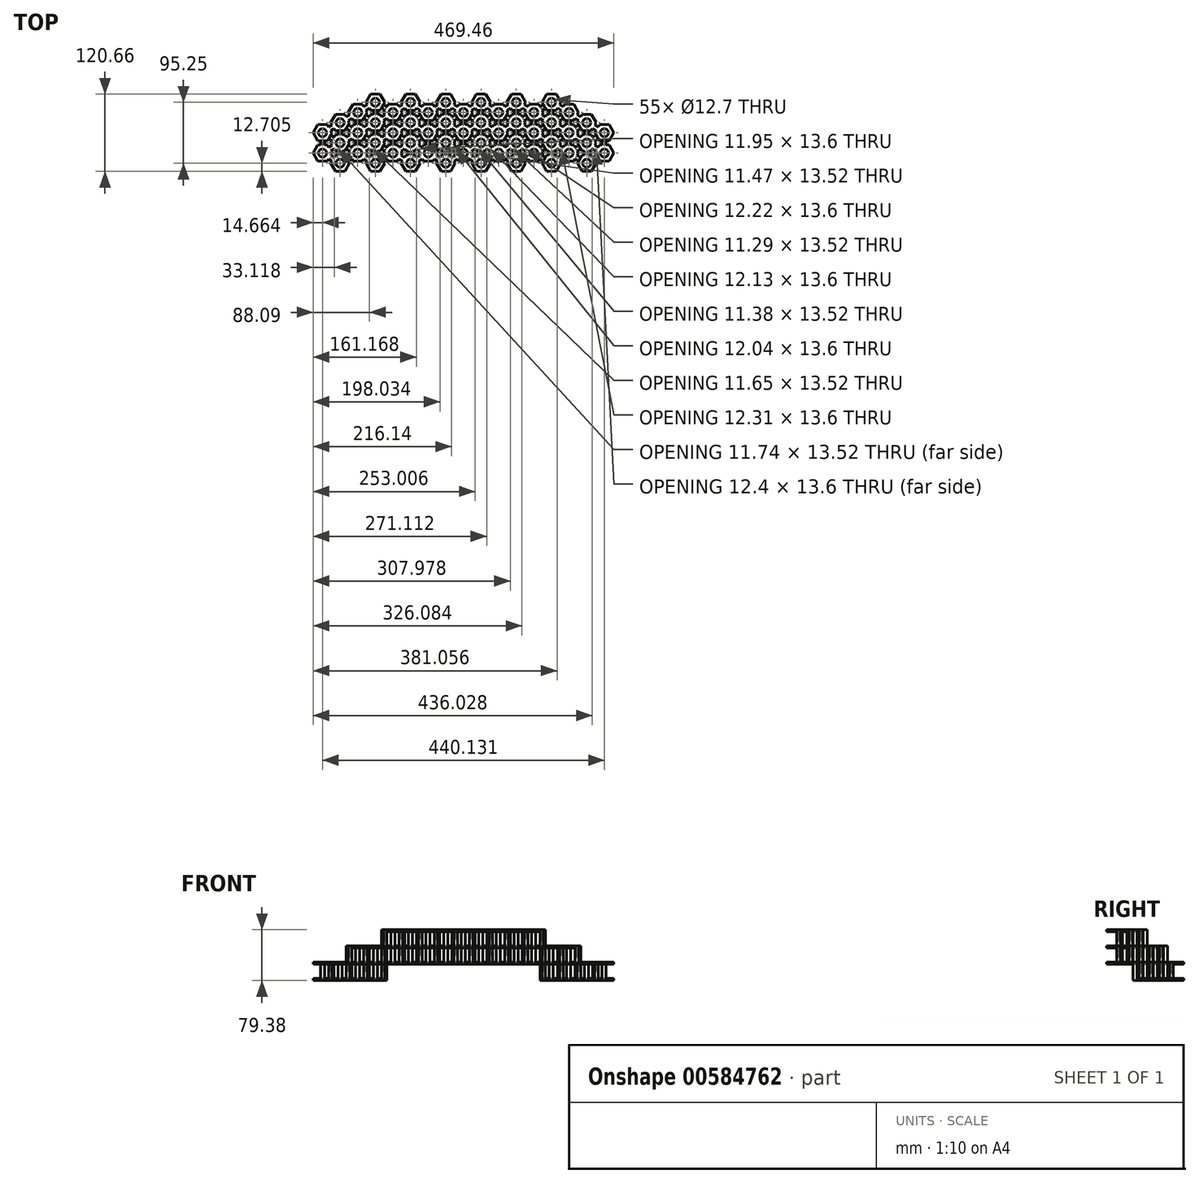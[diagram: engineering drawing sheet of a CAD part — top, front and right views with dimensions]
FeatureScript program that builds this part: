
annotation { "Feature Type Name" : "Feature", "Feature Type Description" : "" }
export const myFeature = defineFeature(function(context is Context, id is Id, definition is map)
    precondition{}
    {
        {
            var Q0;
            Q0=qCreatedBy(makeId("Top.planeOp"),FACE);
            var sketch = newSketch(context, id + "F0", { "sketchPlane" : qUnion([Q0])});
            skLineSegment(sketch, "E0", {"start": v(-220.07, 0) * mm, "end": v(-220.07, -12.7) * mm, "construction": true});
            skLineSegment(sketch, "E1", {"start": v(-234.73, 0) * mm, "end": v(-220.07, 0) * mm, "construction": true});
            skCircle(sketch, "E2.cCircle", {"center": v(-220.07, 0) * mm, "radius": 12.7 * mm, "construction": true});
            skLineSegment(sketch, "E2.0", {"start": v(-212.73, -12.7) * mm, "end": v(-227.4, -12.7) * mm});
            skLineSegment(sketch, "E2.1", {"start": v(-227.4, -12.7) * mm, "end": v(-234.73, 0) * mm});
            skLineSegment(sketch, "E2.2", {"start": v(-234.73, 0) * mm, "end": v(-227.4, 12.7) * mm});
            skLineSegment(sketch, "E2.3", {"start": v(-227.4, 12.7) * mm, "end": v(-212.73, 12.7) * mm});
            skLineSegment(sketch, "E2.4", {"start": v(-212.73, 12.7) * mm, "end": v(-205.4, 0) * mm});
            skLineSegment(sketch, "E2.5", {"start": v(-205.4, 0) * mm, "end": v(-212.73, -12.7) * mm});
            skPoint(sketch, "E2.0.midPoint", {"position": v(-220.07, -12.7) * mm});
            skCircle(sketch, "E3", {"center": v(-220.07, 0) * mm, "radius": 6.35 * mm});
            skLineSegment(sketch, "E4", {"start": v(-220.07, 0) * mm, "end": v(-192.57, -15.88) * mm, "construction": true});
            skCircle(sketch, "E5", {"center": v(-192.57, -15.88) * mm, "radius": 6.35 * mm});
            skCircle(sketch, "E6.cCircle", {"center": v(-192.57, -15.88) * mm, "radius": 12.7 * mm, "construction": true});
            skLineSegment(sketch, "E6.0", {"start": v(-199.9, -3.18) * mm, "end": v(-185.24, -3.18) * mm});
            skLineSegment(sketch, "E6.1", {"start": v(-185.24, -3.18) * mm, "end": v(-177.9, -15.88) * mm});
            skLineSegment(sketch, "E6.2", {"start": v(-177.9, -15.87) * mm, "end": v(-185.24, -28.57) * mm});
            skLineSegment(sketch, "E6.3", {"start": v(-185.24, -28.58) * mm, "end": v(-199.9, -28.58) * mm});
            skLineSegment(sketch, "E6.4", {"start": v(-199.9, -28.58) * mm, "end": v(-207.23, -15.88) * mm});
            skLineSegment(sketch, "E6.5", {"start": v(-207.23, -15.88) * mm, "end": v(-199.9, -3.18) * mm});
            skPoint(sketch, "E6.0.midPoint", {"position": v(-192.57, -3.18) * mm});
            skLineSegment(sketch, "E7", {"start": v(-192.57, -15.88) * mm, "end": v(-207.23, -15.88) * mm, "construction": true});
            skLineSegment(sketch, "E8", {"start": v(-192.57, -15.88) * mm, "end": v(-192.57, -28.58) * mm, "construction": true});
            skCircle(sketch, "E9.1.0.0", {"center": v(-137.55, -15.88) * mm, "radius": 6.35 * mm});
            skLineSegment(sketch, "E9.1.0.1", {"start": v(-172.38, 12.7) * mm, "end": v(-157.72, 12.7) * mm});
            skLineSegment(sketch, "E9.1.0.2", {"start": v(-144.89, -3.18) * mm, "end": v(-130.22, -3.18) * mm});
            skLineSegment(sketch, "E9.1.0.3", {"start": v(-152.22, -15.88) * mm, "end": v(-144.89, -3.18) * mm});
            skLineSegment(sketch, "E9.1.0.4", {"start": v(-179.71, 0) * mm, "end": v(-172.38, 12.7) * mm});
            skLineSegment(sketch, "E9.1.0.5", {"start": v(-144.89, -28.58) * mm, "end": v(-152.22, -15.88) * mm});
            skCircle(sketch, "E9.1.0.6", {"center": v(-165.05, 0) * mm, "radius": 6.35 * mm});
            skLineSegment(sketch, "E9.1.0.7", {"start": v(-172.38, -12.7) * mm, "end": v(-179.71, 0) * mm});
            skLineSegment(sketch, "E9.1.0.8", {"start": v(-130.22, -28.58) * mm, "end": v(-144.89, -28.58) * mm});
            skLineSegment(sketch, "E9.1.0.9", {"start": v(-157.72, -12.7) * mm, "end": v(-172.38, -12.7) * mm});
            skLineSegment(sketch, "E9.1.0.10", {"start": v(-150.38, 0) * mm, "end": v(-157.72, -12.7) * mm});
            skLineSegment(sketch, "E9.1.0.11", {"start": v(-122.89, -15.88) * mm, "end": v(-130.22, -28.58) * mm});
            skLineSegment(sketch, "E9.1.0.12", {"start": v(-157.72, 12.7) * mm, "end": v(-150.38, 0) * mm});
            skLineSegment(sketch, "E9.1.0.13", {"start": v(-130.22, -3.18) * mm, "end": v(-122.89, -15.88) * mm});
            skCircle(sketch, "E9.2.0.0", {"center": v(-82.54, -15.88) * mm, "radius": 6.35 * mm});
            skLineSegment(sketch, "E9.2.0.1", {"start": v(-117.37, 12.7) * mm, "end": v(-102.7, 12.7) * mm});
            skLineSegment(sketch, "E9.2.0.2", {"start": v(-89.87, -3.18) * mm, "end": v(-75.2, -3.18) * mm});
            skLineSegment(sketch, "E9.2.0.3", {"start": v(-97.2, -15.88) * mm, "end": v(-89.87, -3.18) * mm});
            skLineSegment(sketch, "E9.2.0.4", {"start": v(-124.7, 0) * mm, "end": v(-117.37, 12.7) * mm});
            skLineSegment(sketch, "E9.2.0.5", {"start": v(-89.87, -28.58) * mm, "end": v(-97.2, -15.88) * mm});
            skCircle(sketch, "E9.2.0.6", {"center": v(-110.03, 0) * mm, "radius": 6.35 * mm});
            skLineSegment(sketch, "E9.2.0.7", {"start": v(-117.37, -12.7) * mm, "end": v(-124.7, 0) * mm});
            skLineSegment(sketch, "E9.2.0.8", {"start": v(-75.2, -28.58) * mm, "end": v(-89.87, -28.58) * mm});
            skLineSegment(sketch, "E9.2.0.9", {"start": v(-102.7, -12.7) * mm, "end": v(-117.37, -12.7) * mm});
            skLineSegment(sketch, "E9.2.0.10", {"start": v(-95.37, 0) * mm, "end": v(-102.7, -12.7) * mm});
            skLineSegment(sketch, "E9.2.0.11", {"start": v(-67.87, -15.88) * mm, "end": v(-75.2, -28.58) * mm});
            skLineSegment(sketch, "E9.2.0.12", {"start": v(-102.7, 12.7) * mm, "end": v(-95.37, 0) * mm});
            skLineSegment(sketch, "E9.2.0.13", {"start": v(-75.2, -3.18) * mm, "end": v(-67.87, -15.88) * mm});
            skCircle(sketch, "E9.3.0.0", {"center": v(-27.52, -15.88) * mm, "radius": 6.35 * mm});
            skLineSegment(sketch, "E9.3.0.1", {"start": v(-62.35, 12.7) * mm, "end": v(-47.68, 12.7) * mm});
            skLineSegment(sketch, "E9.3.0.2", {"start": v(-34.85, -3.18) * mm, "end": v(-20.19, -3.18) * mm});
            skLineSegment(sketch, "E9.3.0.3", {"start": v(-42.18, -15.88) * mm, "end": v(-34.85, -3.18) * mm});
            skLineSegment(sketch, "E9.3.0.4", {"start": v(-69.68, 0) * mm, "end": v(-62.35, 12.7) * mm});
            skLineSegment(sketch, "E9.3.0.5", {"start": v(-34.85, -28.58) * mm, "end": v(-42.18, -15.88) * mm});
            skCircle(sketch, "E9.3.0.6", {"center": v(-55.02, 0) * mm, "radius": 6.35 * mm});
            skLineSegment(sketch, "E9.3.0.7", {"start": v(-62.35, -12.7) * mm, "end": v(-69.68, 0) * mm});
            skLineSegment(sketch, "E9.3.0.8", {"start": v(-20.19, -28.58) * mm, "end": v(-34.85, -28.58) * mm});
            skLineSegment(sketch, "E9.3.0.9", {"start": v(-47.68, -12.7) * mm, "end": v(-62.35, -12.7) * mm});
            skLineSegment(sketch, "E9.3.0.10", {"start": v(-40.35, 0) * mm, "end": v(-47.68, -12.7) * mm});
            skLineSegment(sketch, "E9.3.0.11", {"start": v(-12.86, -15.88) * mm, "end": v(-20.19, -28.58) * mm});
            skLineSegment(sketch, "E9.3.0.12", {"start": v(-47.68, 12.7) * mm, "end": v(-40.35, 0) * mm});
            skLineSegment(sketch, "E9.3.0.13", {"start": v(-20.19, -3.18) * mm, "end": v(-12.86, -15.88) * mm});
            skCircle(sketch, "E9.4.0.0", {"center": v(27.5, -15.88) * mm, "radius": 6.35 * mm});
            skLineSegment(sketch, "E9.4.0.1", {"start": v(-7.33, 12.7) * mm, "end": v(7.33, 12.7) * mm});
            skLineSegment(sketch, "E9.4.0.2", {"start": v(20.16, -3.18) * mm, "end": v(34.83, -3.18) * mm});
            skLineSegment(sketch, "E9.4.0.3", {"start": v(12.83, -15.88) * mm, "end": v(20.16, -3.18) * mm});
            skLineSegment(sketch, "E9.4.0.4", {"start": v(-14.66, 0) * mm, "end": v(-7.33, 12.7) * mm});
            skLineSegment(sketch, "E9.4.0.5", {"start": v(20.16, -28.58) * mm, "end": v(12.83, -15.88) * mm});
            skCircle(sketch, "E9.4.0.6", {"center": v(0, 0) * mm, "radius": 6.35 * mm});
            skLineSegment(sketch, "E9.4.0.7", {"start": v(-7.33, -12.7) * mm, "end": v(-14.66, 0) * mm});
            skLineSegment(sketch, "E9.4.0.8", {"start": v(34.83, -28.57) * mm, "end": v(20.16, -28.57) * mm});
            skLineSegment(sketch, "E9.4.0.9", {"start": v(7.33, -12.7) * mm, "end": v(-7.33, -12.7) * mm});
            skLineSegment(sketch, "E9.4.0.10", {"start": v(14.66, 0) * mm, "end": v(7.33, -12.7) * mm});
            skLineSegment(sketch, "E9.4.0.11", {"start": v(42.16, -15.87) * mm, "end": v(34.83, -28.57) * mm});
            skLineSegment(sketch, "E9.4.0.12", {"start": v(7.33, 12.7) * mm, "end": v(14.66, 0) * mm});
            skLineSegment(sketch, "E9.4.0.13", {"start": v(34.83, -3.18) * mm, "end": v(42.16, -15.88) * mm});
            skCircle(sketch, "E9.5.0.0", {"center": v(82.51, -15.87) * mm, "radius": 6.35 * mm});
            skLineSegment(sketch, "E9.5.0.1", {"start": v(47.68, 12.7) * mm, "end": v(62.35, 12.7) * mm});
            skLineSegment(sketch, "E9.5.0.2", {"start": v(75.18, -3.18) * mm, "end": v(89.85, -3.17) * mm});
            skLineSegment(sketch, "E9.5.0.3", {"start": v(67.85, -15.88) * mm, "end": v(75.18, -3.18) * mm});
            skLineSegment(sketch, "E9.5.0.4", {"start": v(40.35, 0) * mm, "end": v(47.68, 12.7) * mm});
            skLineSegment(sketch, "E9.5.0.5", {"start": v(75.18, -28.57) * mm, "end": v(67.85, -15.87) * mm});
            skCircle(sketch, "E9.5.0.6", {"center": v(55.02, 0) * mm, "radius": 6.35 * mm});
            skLineSegment(sketch, "E9.5.0.7", {"start": v(47.68, -12.7) * mm, "end": v(40.35, 0) * mm});
            skLineSegment(sketch, "E9.5.0.8", {"start": v(89.85, -28.57) * mm, "end": v(75.18, -28.57) * mm});
            skLineSegment(sketch, "E9.5.0.9", {"start": v(62.35, -12.7) * mm, "end": v(47.68, -12.7) * mm});
            skLineSegment(sketch, "E9.5.0.10", {"start": v(69.68, 0) * mm, "end": v(62.35, -12.7) * mm});
            skLineSegment(sketch, "E9.5.0.11", {"start": v(97.18, -15.87) * mm, "end": v(89.85, -28.57) * mm});
            skLineSegment(sketch, "E9.5.0.12", {"start": v(62.35, 12.7) * mm, "end": v(69.68, 0) * mm});
            skLineSegment(sketch, "E9.5.0.13", {"start": v(89.85, -3.17) * mm, "end": v(97.18, -15.87) * mm});
            skCircle(sketch, "E9.6.0.0", {"center": v(137.53, -15.87) * mm, "radius": 6.35 * mm});
            skLineSegment(sketch, "E9.6.0.1", {"start": v(102.7, 12.7) * mm, "end": v(117.37, 12.7) * mm});
            skLineSegment(sketch, "E9.6.0.2", {"start": v(130.2, -3.17) * mm, "end": v(144.86, -3.17) * mm});
            skLineSegment(sketch, "E9.6.0.3", {"start": v(122.86, -15.87) * mm, "end": v(130.2, -3.17) * mm});
            skLineSegment(sketch, "E9.6.0.4", {"start": v(95.37, 0) * mm, "end": v(102.7, 12.7) * mm});
            skLineSegment(sketch, "E9.6.0.5", {"start": v(130.2, -28.57) * mm, "end": v(122.86, -15.87) * mm});
            skCircle(sketch, "E9.6.0.6", {"center": v(110.03, 0) * mm, "radius": 6.35 * mm});
            skLineSegment(sketch, "E9.6.0.7", {"start": v(102.7, -12.7) * mm, "end": v(95.37, 0) * mm});
            skLineSegment(sketch, "E9.6.0.8", {"start": v(144.86, -28.57) * mm, "end": v(130.2, -28.57) * mm});
            skLineSegment(sketch, "E9.6.0.9", {"start": v(117.37, -12.7) * mm, "end": v(102.7, -12.7) * mm});
            skLineSegment(sketch, "E9.6.0.10", {"start": v(124.7, 0) * mm, "end": v(117.37, -12.7) * mm});
            skLineSegment(sketch, "E9.6.0.11", {"start": v(152.2, -15.87) * mm, "end": v(144.86, -28.57) * mm});
            skLineSegment(sketch, "E9.6.0.12", {"start": v(117.37, 12.7) * mm, "end": v(124.7, 0) * mm});
            skLineSegment(sketch, "E9.6.0.13", {"start": v(144.86, -3.17) * mm, "end": v(152.2, -15.87) * mm});
            skCircle(sketch, "E9.7.0.0", {"center": v(192.55, -15.87) * mm, "radius": 6.35 * mm});
            skLineSegment(sketch, "E9.7.0.1", {"start": v(157.72, 12.7) * mm, "end": v(172.38, 12.7) * mm});
            skLineSegment(sketch, "E9.7.0.2", {"start": v(185.21, -3.17) * mm, "end": v(199.88, -3.17) * mm});
            skLineSegment(sketch, "E9.7.0.3", {"start": v(177.88, -15.87) * mm, "end": v(185.21, -3.17) * mm});
            skLineSegment(sketch, "E9.7.0.4", {"start": v(150.38, 0) * mm, "end": v(157.72, 12.7) * mm});
            skLineSegment(sketch, "E9.7.0.5", {"start": v(185.21, -28.57) * mm, "end": v(177.88, -15.87) * mm});
            skCircle(sketch, "E9.7.0.6", {"center": v(165.05, 0) * mm, "radius": 6.35 * mm});
            skLineSegment(sketch, "E9.7.0.7", {"start": v(157.72, -12.7) * mm, "end": v(150.38, 0) * mm});
            skLineSegment(sketch, "E9.7.0.8", {"start": v(199.88, -28.57) * mm, "end": v(185.21, -28.57) * mm});
            skLineSegment(sketch, "E9.7.0.9", {"start": v(172.38, -12.7) * mm, "end": v(157.72, -12.7) * mm});
            skLineSegment(sketch, "E9.7.0.10", {"start": v(179.71, 0) * mm, "end": v(172.38, -12.7) * mm});
            skLineSegment(sketch, "E9.7.0.11", {"start": v(207.21, -15.87) * mm, "end": v(199.88, -28.57) * mm});
            skLineSegment(sketch, "E9.7.0.12", {"start": v(172.38, 12.7) * mm, "end": v(179.71, 0) * mm});
            skLineSegment(sketch, "E9.7.0.13", {"start": v(199.88, -3.17) * mm, "end": v(207.21, -15.87) * mm});
            skLineSegment(sketch, "E9.8.0.1", {"start": v(212.73, 12.7) * mm, "end": v(227.4, 12.7) * mm});
            skLineSegment(sketch, "E9.8.0.4", {"start": v(205.4, 0) * mm, "end": v(212.73, 12.7) * mm});
            skCircle(sketch, "E9.8.0.6", {"center": v(220.07, 0) * mm, "radius": 6.35 * mm});
            skLineSegment(sketch, "E9.8.0.7", {"start": v(212.73, -12.7) * mm, "end": v(205.4, 0) * mm});
            skLineSegment(sketch, "E9.8.0.9", {"start": v(227.4, -12.7) * mm, "end": v(212.73, -12.7) * mm});
            skLineSegment(sketch, "E9.8.0.10", {"start": v(234.73, 0) * mm, "end": v(227.4, -12.7) * mm});
            skLineSegment(sketch, "E9.8.0.12", {"start": v(227.4, 12.7) * mm, "end": v(234.73, 0) * mm});
            skLineSegment(sketch, "E9.direction1", {"start": v(-192.57, -15.88) * mm, "end": v(-137.55, -15.88) * mm, "construction": true});
            skLineSegment(sketch, "E10.0.1.0", {"start": v(14.66, 31.75) * mm, "end": v(7.33, 19.05) * mm});
            skLineSegment(sketch, "E10.0.1.1", {"start": v(40.35, 31.75) * mm, "end": v(47.68, 44.45) * mm});
            skCircle(sketch, "E10.0.1.2", {"center": v(165.05, 31.75) * mm, "radius": 6.35 * mm});
            skLineSegment(sketch, "E10.0.1.3", {"start": v(-172.38, 44.45) * mm, "end": v(-157.72, 44.45) * mm});
            skLineSegment(sketch, "E10.0.1.4", {"start": v(212.73, 44.45) * mm, "end": v(227.4, 44.45) * mm});
            skLineSegment(sketch, "E10.0.1.5", {"start": v(-75.2, 3.18) * mm, "end": v(-89.87, 3.18) * mm});
            skLineSegment(sketch, "E10.0.1.6", {"start": v(199.88, 28.57) * mm, "end": v(207.21, 15.88) * mm});
            skLineSegment(sketch, "E10.0.1.7", {"start": v(-42.18, 15.88) * mm, "end": v(-34.85, 28.57) * mm});
            skLineSegment(sketch, "E10.0.1.8", {"start": v(227.4, 44.45) * mm, "end": v(234.73, 31.75) * mm});
            skLineSegment(sketch, "E10.0.1.9", {"start": v(75.18, 3.18) * mm, "end": v(67.85, 15.88) * mm});
            skCircle(sketch, "E10.0.1.10", {"center": v(137.53, 15.88) * mm, "radius": 6.35 * mm});
            skLineSegment(sketch, "E10.0.1.11", {"start": v(157.72, 19.05) * mm, "end": v(150.38, 31.75) * mm});
            skLineSegment(sketch, "E10.0.1.12", {"start": v(-144.89, 28.57) * mm, "end": v(-130.22, 28.57) * mm});
            skLineSegment(sketch, "E10.0.1.13", {"start": v(-75.2, 28.57) * mm, "end": v(-67.87, 15.88) * mm});
            skLineSegment(sketch, "E10.0.1.14", {"start": v(-102.7, 19.05) * mm, "end": v(-117.37, 19.05) * mm});
            skCircle(sketch, "E10.0.1.15", {"center": v(-192.57, 15.88) * mm, "radius": 6.35 * mm});
            skLineSegment(sketch, "E10.0.1.16", {"start": v(-69.68, 31.75) * mm, "end": v(-62.35, 44.45) * mm});
            skLineSegment(sketch, "E10.0.1.17", {"start": v(-47.68, 44.45) * mm, "end": v(-40.35, 31.75) * mm});
            skLineSegment(sketch, "E10.0.1.18", {"start": v(42.16, 15.88) * mm, "end": v(34.83, 3.18) * mm});
            skCircle(sketch, "E10.0.1.19", {"center": v(55.02, 31.75) * mm, "radius": 6.35 * mm});
            skLineSegment(sketch, "E10.0.1.20", {"start": v(102.7, 44.45) * mm, "end": v(117.37, 44.45) * mm});
            skLineSegment(sketch, "E10.0.1.21", {"start": v(69.68, 31.75) * mm, "end": v(62.35, 19.05) * mm});
            skLineSegment(sketch, "E10.0.1.22", {"start": v(-152.22, 15.88) * mm, "end": v(-144.89, 28.57) * mm});
            skLineSegment(sketch, "E10.0.1.23", {"start": v(-234.73, 31.75) * mm, "end": v(-227.4, 44.45) * mm});
            skLineSegment(sketch, "E10.0.1.24", {"start": v(199.88, 3.18) * mm, "end": v(185.21, 3.18) * mm});
            skLineSegment(sketch, "E10.0.1.25", {"start": v(-199.9, 28.57) * mm, "end": v(-185.24, 28.57) * mm});
            skLineSegment(sketch, "E10.0.1.26", {"start": v(-34.85, 3.18) * mm, "end": v(-42.18, 15.88) * mm});
            skCircle(sketch, "E10.0.1.27", {"center": v(27.5, 15.88) * mm, "radius": 6.35 * mm});
            skLineSegment(sketch, "E10.0.1.28", {"start": v(-199.9, 3.18) * mm, "end": v(-207.23, 15.88) * mm});
            skLineSegment(sketch, "E10.0.1.29", {"start": v(47.68, 19.05) * mm, "end": v(40.35, 31.75) * mm});
            skLineSegment(sketch, "E10.0.1.30", {"start": v(130.2, 28.57) * mm, "end": v(144.86, 28.57) * mm});
            skLineSegment(sketch, "E10.0.1.31", {"start": v(172.38, 19.05) * mm, "end": v(157.72, 19.05) * mm});
            skLineSegment(sketch, "E10.0.1.32", {"start": v(-179.71, 31.75) * mm, "end": v(-172.38, 44.45) * mm});
            skLineSegment(sketch, "E10.0.1.33", {"start": v(205.4, 31.75) * mm, "end": v(212.73, 44.45) * mm});
            skLineSegment(sketch, "E10.0.1.34", {"start": v(-20.19, 28.57) * mm, "end": v(-12.86, 15.88) * mm});
            skCircle(sketch, "E10.0.1.35", {"center": v(-55.02, 31.75) * mm, "radius": 6.35 * mm});
            skLineSegment(sketch, "E10.0.1.36", {"start": v(-7.33, 44.45) * mm, "end": v(7.33, 44.45) * mm});
            skLineSegment(sketch, "E10.0.1.37", {"start": v(7.33, 44.45) * mm, "end": v(14.66, 31.75) * mm});
            skLineSegment(sketch, "E10.0.1.38", {"start": v(89.85, 3.18) * mm, "end": v(75.18, 3.18) * mm});
            skLineSegment(sketch, "E10.0.1.39", {"start": v(97.18, 15.88) * mm, "end": v(89.85, 3.18) * mm});
            skLineSegment(sketch, "E10.0.1.40", {"start": v(122.86, 15.88) * mm, "end": v(130.2, 28.57) * mm});
            skLineSegment(sketch, "E10.0.1.41", {"start": v(-144.89, 3.18) * mm, "end": v(-152.22, 15.88) * mm});
            skCircle(sketch, "E10.0.1.42", {"center": v(-220.07, 31.75) * mm, "radius": 6.35 * mm});
            skLineSegment(sketch, "E10.0.1.43", {"start": v(124.7, 31.75) * mm, "end": v(117.37, 19.05) * mm});
            skCircle(sketch, "E10.0.1.44", {"center": v(-82.54, 15.88) * mm, "radius": 6.35 * mm});
            skLineSegment(sketch, "E10.0.1.45", {"start": v(-62.35, 19.05) * mm, "end": v(-69.68, 31.75) * mm});
            skLineSegment(sketch, "E10.0.1.46", {"start": v(20.16, 28.57) * mm, "end": v(34.83, 28.57) * mm});
            skLineSegment(sketch, "E10.0.1.47", {"start": v(62.35, 19.05) * mm, "end": v(47.68, 19.05) * mm});
            skLineSegment(sketch, "E10.0.1.48", {"start": v(95.37, 31.75) * mm, "end": v(102.7, 44.45) * mm});
            skCircle(sketch, "E10.0.1.49", {"center": v(-165.05, 31.75) * mm, "radius": 6.35 * mm});
            skLineSegment(sketch, "E10.0.1.50", {"start": v(-150.38, 31.75) * mm, "end": v(-157.72, 19.05) * mm});
            skCircle(sketch, "E10.0.1.51", {"center": v(220.07, 31.75) * mm, "radius": 6.35 * mm});
            skLineSegment(sketch, "E10.0.1.52", {"start": v(-185.24, 28.57) * mm, "end": v(-177.9, 15.88) * mm});
            skLineSegment(sketch, "E10.0.1.53", {"start": v(-117.37, 44.45) * mm, "end": v(-102.7, 44.45) * mm});
            skLineSegment(sketch, "E10.0.1.54", {"start": v(-227.4, 44.45) * mm, "end": v(-212.73, 44.45) * mm});
            skLineSegment(sketch, "E10.0.1.55", {"start": v(-20.19, 3.18) * mm, "end": v(-34.85, 3.18) * mm});
            skLineSegment(sketch, "E10.0.1.56", {"start": v(12.83, 15.88) * mm, "end": v(20.16, 28.57) * mm});
            skLineSegment(sketch, "E10.0.1.57", {"start": v(34.83, 28.57) * mm, "end": v(42.16, 15.88) * mm});
            skLineSegment(sketch, "E10.0.1.58", {"start": v(-207.23, 15.88) * mm, "end": v(-199.9, 28.57) * mm});
            skLineSegment(sketch, "E10.0.1.59", {"start": v(62.35, 44.45) * mm, "end": v(69.68, 31.75) * mm});
            skLineSegment(sketch, "E10.0.1.60", {"start": v(130.2, 3.18) * mm, "end": v(122.86, 15.88) * mm});
            skCircle(sketch, "E10.0.1.61", {"center": v(192.55, 15.88) * mm, "radius": 6.35 * mm});
            skLineSegment(sketch, "E10.0.1.62", {"start": v(-172.38, 19.05) * mm, "end": v(-179.71, 31.75) * mm});
            skLineSegment(sketch, "E10.0.1.63", {"start": v(152.2, 15.88) * mm, "end": v(144.86, 3.18) * mm});
            skLineSegment(sketch, "E10.0.1.64", {"start": v(212.73, 19.05) * mm, "end": v(205.4, 31.75) * mm});
            skLineSegment(sketch, "E10.0.1.65", {"start": v(-89.87, 28.57) * mm, "end": v(-75.2, 28.57) * mm});
            skLineSegment(sketch, "E10.0.1.66", {"start": v(179.71, 31.75) * mm, "end": v(172.38, 19.05) * mm});
            skLineSegment(sketch, "E10.0.1.67", {"start": v(-47.68, 19.05) * mm, "end": v(-62.35, 19.05) * mm});
            skLineSegment(sketch, "E10.0.1.68", {"start": v(-14.66, 31.75) * mm, "end": v(-7.33, 44.45) * mm});
            skCircle(sketch, "E10.0.1.69", {"center": v(110.03, 31.75) * mm, "radius": 6.35 * mm});
            skLineSegment(sketch, "E10.0.1.70", {"start": v(157.72, 44.45) * mm, "end": v(172.38, 44.45) * mm});
            skLineSegment(sketch, "E10.0.1.71", {"start": v(-122.89, 15.88) * mm, "end": v(-130.22, 3.18) * mm});
            skLineSegment(sketch, "E10.0.1.72", {"start": v(-130.22, 3.18) * mm, "end": v(-144.89, 3.18) * mm});
            skLineSegment(sketch, "E10.0.1.73", {"start": v(-97.2, 15.88) * mm, "end": v(-89.87, 28.57) * mm});
            skLineSegment(sketch, "E10.0.1.74", {"start": v(-95.37, 31.75) * mm, "end": v(-102.7, 19.05) * mm});
            skLineSegment(sketch, "E10.0.1.75", {"start": v(20.16, 3.18) * mm, "end": v(12.83, 15.88) * mm});
            skCircle(sketch, "E10.0.1.76", {"center": v(82.51, 15.88) * mm, "radius": 6.35 * mm});
            skLineSegment(sketch, "E10.0.1.77", {"start": v(89.85, 28.57) * mm, "end": v(97.18, 15.88) * mm});
            skLineSegment(sketch, "E10.0.1.78", {"start": v(102.7, 19.05) * mm, "end": v(95.37, 31.75) * mm});
            skLineSegment(sketch, "E10.0.1.79", {"start": v(-212.73, 19.05) * mm, "end": v(-227.4, 19.05) * mm});
            skLineSegment(sketch, "E10.0.1.80", {"start": v(185.21, 28.57) * mm, "end": v(199.88, 28.57) * mm});
            skLineSegment(sketch, "E10.0.1.81", {"start": v(-157.72, 19.05) * mm, "end": v(-172.38, 19.05) * mm});
            skLineSegment(sketch, "E10.0.1.82", {"start": v(117.37, 44.45) * mm, "end": v(124.7, 31.75) * mm});
            skLineSegment(sketch, "E10.0.1.83", {"start": v(227.4, 19.05) * mm, "end": v(212.73, 19.05) * mm});
            skLineSegment(sketch, "E10.0.1.84", {"start": v(-124.7, 31.75) * mm, "end": v(-117.37, 44.45) * mm});
            skLineSegment(sketch, "E10.0.1.85", {"start": v(207.21, 15.88) * mm, "end": v(199.88, 3.18) * mm});
            skLineSegment(sketch, "E10.0.1.86", {"start": v(-177.9, 15.88) * mm, "end": v(-185.24, 3.18) * mm});
            skLineSegment(sketch, "E10.0.1.87", {"start": v(-212.73, 44.45) * mm, "end": v(-205.4, 31.75) * mm});
            skLineSegment(sketch, "E10.0.1.88", {"start": v(234.73, 31.75) * mm, "end": v(227.4, 19.05) * mm});
            skCircle(sketch, "E10.0.1.89", {"center": v(0, 31.75) * mm, "radius": 6.35 * mm});
            skLineSegment(sketch, "E10.0.1.90", {"start": v(47.68, 44.45) * mm, "end": v(62.35, 44.45) * mm});
            skLineSegment(sketch, "E10.0.1.91", {"start": v(144.86, 3.18) * mm, "end": v(130.2, 3.18) * mm});
            skLineSegment(sketch, "E10.0.1.92", {"start": v(177.88, 15.88) * mm, "end": v(185.21, 28.57) * mm});
            skLineSegment(sketch, "E10.0.1.93", {"start": v(-157.72, 44.45) * mm, "end": v(-150.38, 31.75) * mm});
            skLineSegment(sketch, "E10.0.1.94", {"start": v(-89.87, 3.18) * mm, "end": v(-97.2, 15.88) * mm});
            skLineSegment(sketch, "E10.0.1.95", {"start": v(-67.87, 15.88) * mm, "end": v(-75.2, 3.18) * mm});
            skCircle(sketch, "E10.0.1.96", {"center": v(-27.52, 15.88) * mm, "radius": 6.35 * mm});
            skLineSegment(sketch, "E10.0.1.97", {"start": v(-40.35, 31.75) * mm, "end": v(-47.68, 19.05) * mm});
            skLineSegment(sketch, "E10.0.1.98", {"start": v(-7.33, 19.05) * mm, "end": v(-14.66, 31.75) * mm});
            skLineSegment(sketch, "E10.0.1.99", {"start": v(75.18, 28.57) * mm, "end": v(89.85, 28.57) * mm});
            skLineSegment(sketch, "E10.0.1.100", {"start": v(117.37, 19.05) * mm, "end": v(102.7, 19.05) * mm});
            skLineSegment(sketch, "E10.0.1.101", {"start": v(144.86, 28.57) * mm, "end": v(152.2, 15.88) * mm});
            skLineSegment(sketch, "E10.0.1.102", {"start": v(150.38, 31.75) * mm, "end": v(157.72, 44.45) * mm});
            skLineSegment(sketch, "E10.0.1.103", {"start": v(172.38, 44.45) * mm, "end": v(179.71, 31.75) * mm});
            skCircle(sketch, "E10.0.1.104", {"center": v(-110.03, 31.75) * mm, "radius": 6.35 * mm});
            skLineSegment(sketch, "E10.0.1.105", {"start": v(-62.35, 44.45) * mm, "end": v(-47.68, 44.45) * mm});
            skLineSegment(sketch, "E10.0.1.106", {"start": v(34.83, 3.18) * mm, "end": v(20.16, 3.18) * mm});
            skLineSegment(sketch, "E10.0.1.107", {"start": v(67.85, 15.88) * mm, "end": v(75.18, 28.57) * mm});
            skLineSegment(sketch, "E10.0.1.108", {"start": v(-130.22, 28.57) * mm, "end": v(-122.89, 15.88) * mm});
            skLineSegment(sketch, "E10.0.1.109", {"start": v(-227.4, 19.05) * mm, "end": v(-234.73, 31.75) * mm});
            skLineSegment(sketch, "E10.0.1.110", {"start": v(185.21, 3.18) * mm, "end": v(177.88, 15.88) * mm});
            skCircle(sketch, "E10.0.1.111", {"center": v(-137.55, 15.88) * mm, "radius": 6.35 * mm});
            skLineSegment(sketch, "E10.0.1.112", {"start": v(-102.7, 44.45) * mm, "end": v(-95.37, 31.75) * mm});
            skLineSegment(sketch, "E10.0.1.113", {"start": v(-117.37, 19.05) * mm, "end": v(-124.7, 31.75) * mm});
            skLineSegment(sketch, "E10.0.1.114", {"start": v(-34.85, 28.57) * mm, "end": v(-20.19, 28.57) * mm});
            skLineSegment(sketch, "E10.0.1.115", {"start": v(-205.4, 31.75) * mm, "end": v(-212.73, 19.05) * mm});
            skLineSegment(sketch, "E10.0.1.116", {"start": v(-185.24, 3.18) * mm, "end": v(-199.9, 3.18) * mm});
            skLineSegment(sketch, "E10.0.1.117", {"start": v(-12.86, 15.88) * mm, "end": v(-20.19, 3.18) * mm});
            skLineSegment(sketch, "E10.0.1.118", {"start": v(7.33, 19.05) * mm, "end": v(-7.33, 19.05) * mm});
            skLineSegment(sketch, "E10.0.2.0", {"start": v(14.66, 63.5) * mm, "end": v(7.33, 50.8) * mm});
            skLineSegment(sketch, "E10.0.2.1", {"start": v(40.35, 63.5) * mm, "end": v(47.68, 76.2) * mm});
            skCircle(sketch, "E10.0.2.2", {"center": v(165.05, 63.5) * mm, "radius": 6.35 * mm});
            skLineSegment(sketch, "E10.0.2.3", {"start": v(-172.38, 76.2) * mm, "end": v(-157.72, 76.2) * mm});
            skLineSegment(sketch, "E10.0.2.4", {"start": v(212.73, 76.2) * mm, "end": v(227.4, 76.2) * mm});
            skLineSegment(sketch, "E10.0.2.5", {"start": v(-75.2, 34.93) * mm, "end": v(-89.87, 34.93) * mm});
            skLineSegment(sketch, "E10.0.2.6", {"start": v(199.88, 60.32) * mm, "end": v(207.21, 47.63) * mm});
            skLineSegment(sketch, "E10.0.2.7", {"start": v(-42.18, 47.63) * mm, "end": v(-34.85, 60.32) * mm});
            skLineSegment(sketch, "E10.0.2.8", {"start": v(227.4, 76.2) * mm, "end": v(234.73, 63.5) * mm});
            skLineSegment(sketch, "E10.0.2.9", {"start": v(75.18, 34.93) * mm, "end": v(67.85, 47.63) * mm});
            skCircle(sketch, "E10.0.2.10", {"center": v(137.53, 47.63) * mm, "radius": 6.35 * mm});
            skLineSegment(sketch, "E10.0.2.11", {"start": v(157.72, 50.8) * mm, "end": v(150.38, 63.5) * mm});
            skLineSegment(sketch, "E10.0.2.12", {"start": v(-144.89, 60.32) * mm, "end": v(-130.22, 60.32) * mm});
            skLineSegment(sketch, "E10.0.2.13", {"start": v(-75.2, 60.32) * mm, "end": v(-67.87, 47.63) * mm});
            skLineSegment(sketch, "E10.0.2.14", {"start": v(-102.7, 50.8) * mm, "end": v(-117.37, 50.8) * mm});
            skCircle(sketch, "E10.0.2.15", {"center": v(-192.57, 47.63) * mm, "radius": 6.35 * mm});
            skLineSegment(sketch, "E10.0.2.16", {"start": v(-69.68, 63.5) * mm, "end": v(-62.35, 76.2) * mm});
            skLineSegment(sketch, "E10.0.2.17", {"start": v(-47.68, 76.2) * mm, "end": v(-40.35, 63.5) * mm});
            skLineSegment(sketch, "E10.0.2.18", {"start": v(42.16, 47.63) * mm, "end": v(34.83, 34.93) * mm});
            skCircle(sketch, "E10.0.2.19", {"center": v(55.02, 63.5) * mm, "radius": 6.35 * mm});
            skLineSegment(sketch, "E10.0.2.20", {"start": v(102.7, 76.2) * mm, "end": v(117.37, 76.2) * mm});
            skLineSegment(sketch, "E10.0.2.21", {"start": v(69.68, 63.5) * mm, "end": v(62.35, 50.8) * mm});
            skLineSegment(sketch, "E10.0.2.22", {"start": v(-152.22, 47.63) * mm, "end": v(-144.89, 60.32) * mm});
            skLineSegment(sketch, "E10.0.2.23", {"start": v(-234.73, 63.5) * mm, "end": v(-227.4, 76.2) * mm});
            skLineSegment(sketch, "E10.0.2.24", {"start": v(199.88, 34.93) * mm, "end": v(185.21, 34.93) * mm});
            skLineSegment(sketch, "E10.0.2.25", {"start": v(-199.9, 60.32) * mm, "end": v(-185.24, 60.32) * mm});
            skLineSegment(sketch, "E10.0.2.26", {"start": v(-34.85, 34.93) * mm, "end": v(-42.18, 47.63) * mm});
            skCircle(sketch, "E10.0.2.27", {"center": v(27.5, 47.63) * mm, "radius": 6.35 * mm});
            skLineSegment(sketch, "E10.0.2.28", {"start": v(-199.9, 34.93) * mm, "end": v(-207.23, 47.63) * mm});
            skLineSegment(sketch, "E10.0.2.29", {"start": v(47.68, 50.8) * mm, "end": v(40.35, 63.5) * mm});
            skLineSegment(sketch, "E10.0.2.30", {"start": v(130.2, 60.32) * mm, "end": v(144.86, 60.32) * mm});
            skLineSegment(sketch, "E10.0.2.31", {"start": v(172.38, 50.8) * mm, "end": v(157.72, 50.8) * mm});
            skLineSegment(sketch, "E10.0.2.32", {"start": v(-179.71, 63.5) * mm, "end": v(-172.38, 76.2) * mm});
            skLineSegment(sketch, "E10.0.2.33", {"start": v(205.4, 63.5) * mm, "end": v(212.73, 76.2) * mm});
            skLineSegment(sketch, "E10.0.2.34", {"start": v(-20.19, 60.32) * mm, "end": v(-12.86, 47.63) * mm});
            skCircle(sketch, "E10.0.2.35", {"center": v(-55.02, 63.5) * mm, "radius": 6.35 * mm});
            skLineSegment(sketch, "E10.0.2.36", {"start": v(-7.33, 76.2) * mm, "end": v(7.33, 76.2) * mm});
            skLineSegment(sketch, "E10.0.2.37", {"start": v(7.33, 76.2) * mm, "end": v(14.66, 63.5) * mm});
            skLineSegment(sketch, "E10.0.2.38", {"start": v(89.85, 34.93) * mm, "end": v(75.18, 34.93) * mm});
            skLineSegment(sketch, "E10.0.2.39", {"start": v(97.18, 47.63) * mm, "end": v(89.85, 34.93) * mm});
            skLineSegment(sketch, "E10.0.2.40", {"start": v(122.86, 47.63) * mm, "end": v(130.2, 60.32) * mm});
            skLineSegment(sketch, "E10.0.2.41", {"start": v(-144.89, 34.93) * mm, "end": v(-152.22, 47.63) * mm});
            skCircle(sketch, "E10.0.2.42", {"center": v(-220.07, 63.5) * mm, "radius": 6.35 * mm});
            skLineSegment(sketch, "E10.0.2.43", {"start": v(124.7, 63.5) * mm, "end": v(117.37, 50.8) * mm});
            skCircle(sketch, "E10.0.2.44", {"center": v(-82.54, 47.63) * mm, "radius": 6.35 * mm});
            skLineSegment(sketch, "E10.0.2.45", {"start": v(-62.35, 50.8) * mm, "end": v(-69.68, 63.5) * mm});
            skLineSegment(sketch, "E10.0.2.46", {"start": v(20.16, 60.32) * mm, "end": v(34.83, 60.32) * mm});
            skLineSegment(sketch, "E10.0.2.47", {"start": v(62.35, 50.8) * mm, "end": v(47.68, 50.8) * mm});
            skLineSegment(sketch, "E10.0.2.48", {"start": v(95.37, 63.5) * mm, "end": v(102.7, 76.2) * mm});
            skCircle(sketch, "E10.0.2.49", {"center": v(-165.05, 63.5) * mm, "radius": 6.35 * mm});
            skLineSegment(sketch, "E10.0.2.50", {"start": v(-150.38, 63.5) * mm, "end": v(-157.72, 50.8) * mm});
            skCircle(sketch, "E10.0.2.51", {"center": v(220.07, 63.5) * mm, "radius": 6.35 * mm});
            skLineSegment(sketch, "E10.0.2.52", {"start": v(-185.24, 60.32) * mm, "end": v(-177.9, 47.63) * mm});
            skLineSegment(sketch, "E10.0.2.53", {"start": v(-117.37, 76.2) * mm, "end": v(-102.7, 76.2) * mm});
            skLineSegment(sketch, "E10.0.2.54", {"start": v(-227.4, 76.2) * mm, "end": v(-212.73, 76.2) * mm});
            skLineSegment(sketch, "E10.0.2.55", {"start": v(-20.19, 34.93) * mm, "end": v(-34.85, 34.93) * mm});
            skLineSegment(sketch, "E10.0.2.56", {"start": v(12.83, 47.63) * mm, "end": v(20.16, 60.32) * mm});
            skLineSegment(sketch, "E10.0.2.57", {"start": v(34.83, 60.32) * mm, "end": v(42.16, 47.63) * mm});
            skLineSegment(sketch, "E10.0.2.58", {"start": v(-207.23, 47.63) * mm, "end": v(-199.9, 60.32) * mm});
            skLineSegment(sketch, "E10.0.2.59", {"start": v(62.35, 76.2) * mm, "end": v(69.68, 63.5) * mm});
            skLineSegment(sketch, "E10.0.2.60", {"start": v(130.2, 34.93) * mm, "end": v(122.86, 47.63) * mm});
            skCircle(sketch, "E10.0.2.61", {"center": v(192.55, 47.63) * mm, "radius": 6.35 * mm});
            skLineSegment(sketch, "E10.0.2.62", {"start": v(-172.38, 50.8) * mm, "end": v(-179.71, 63.5) * mm});
            skLineSegment(sketch, "E10.0.2.63", {"start": v(152.2, 47.63) * mm, "end": v(144.86, 34.93) * mm});
            skLineSegment(sketch, "E10.0.2.64", {"start": v(212.73, 50.8) * mm, "end": v(205.4, 63.5) * mm});
            skLineSegment(sketch, "E10.0.2.65", {"start": v(-89.87, 60.32) * mm, "end": v(-75.2, 60.32) * mm});
            skLineSegment(sketch, "E10.0.2.66", {"start": v(179.71, 63.5) * mm, "end": v(172.38, 50.8) * mm});
            skLineSegment(sketch, "E10.0.2.67", {"start": v(-47.68, 50.8) * mm, "end": v(-62.35, 50.8) * mm});
            skLineSegment(sketch, "E10.0.2.68", {"start": v(-14.66, 63.5) * mm, "end": v(-7.33, 76.2) * mm});
            skCircle(sketch, "E10.0.2.69", {"center": v(110.03, 63.5) * mm, "radius": 6.35 * mm});
            skLineSegment(sketch, "E10.0.2.70", {"start": v(157.72, 76.2) * mm, "end": v(172.38, 76.2) * mm});
            skLineSegment(sketch, "E10.0.2.71", {"start": v(-122.89, 47.63) * mm, "end": v(-130.22, 34.93) * mm});
            skLineSegment(sketch, "E10.0.2.72", {"start": v(-130.22, 34.93) * mm, "end": v(-144.89, 34.93) * mm});
            skLineSegment(sketch, "E10.0.2.73", {"start": v(-97.2, 47.63) * mm, "end": v(-89.87, 60.32) * mm});
            skLineSegment(sketch, "E10.0.2.74", {"start": v(-95.37, 63.5) * mm, "end": v(-102.7, 50.8) * mm});
            skLineSegment(sketch, "E10.0.2.75", {"start": v(20.16, 34.93) * mm, "end": v(12.83, 47.63) * mm});
            skCircle(sketch, "E10.0.2.76", {"center": v(82.51, 47.63) * mm, "radius": 6.35 * mm});
            skLineSegment(sketch, "E10.0.2.77", {"start": v(89.85, 60.32) * mm, "end": v(97.18, 47.63) * mm});
            skLineSegment(sketch, "E10.0.2.78", {"start": v(102.7, 50.8) * mm, "end": v(95.37, 63.5) * mm});
            skLineSegment(sketch, "E10.0.2.79", {"start": v(-212.73, 50.8) * mm, "end": v(-227.4, 50.8) * mm});
            skLineSegment(sketch, "E10.0.2.80", {"start": v(185.21, 60.32) * mm, "end": v(199.88, 60.32) * mm});
            skLineSegment(sketch, "E10.0.2.81", {"start": v(-157.72, 50.8) * mm, "end": v(-172.38, 50.8) * mm});
            skLineSegment(sketch, "E10.0.2.82", {"start": v(117.37, 76.2) * mm, "end": v(124.7, 63.5) * mm});
            skLineSegment(sketch, "E10.0.2.83", {"start": v(227.4, 50.8) * mm, "end": v(212.73, 50.8) * mm});
            skLineSegment(sketch, "E10.0.2.84", {"start": v(-124.7, 63.5) * mm, "end": v(-117.37, 76.2) * mm});
            skLineSegment(sketch, "E10.0.2.85", {"start": v(207.21, 47.63) * mm, "end": v(199.88, 34.93) * mm});
            skLineSegment(sketch, "E10.0.2.86", {"start": v(-177.9, 47.63) * mm, "end": v(-185.24, 34.93) * mm});
            skLineSegment(sketch, "E10.0.2.87", {"start": v(-212.73, 76.2) * mm, "end": v(-205.4, 63.5) * mm});
            skLineSegment(sketch, "E10.0.2.88", {"start": v(234.73, 63.5) * mm, "end": v(227.4, 50.8) * mm});
            skCircle(sketch, "E10.0.2.89", {"center": v(0, 63.5) * mm, "radius": 6.35 * mm});
            skLineSegment(sketch, "E10.0.2.90", {"start": v(47.68, 76.2) * mm, "end": v(62.35, 76.2) * mm});
            skLineSegment(sketch, "E10.0.2.91", {"start": v(144.86, 34.93) * mm, "end": v(130.2, 34.93) * mm});
            skLineSegment(sketch, "E10.0.2.92", {"start": v(177.88, 47.63) * mm, "end": v(185.21, 60.32) * mm});
            skLineSegment(sketch, "E10.0.2.93", {"start": v(-157.72, 76.2) * mm, "end": v(-150.38, 63.5) * mm});
            skLineSegment(sketch, "E10.0.2.94", {"start": v(-89.87, 34.93) * mm, "end": v(-97.2, 47.63) * mm});
            skLineSegment(sketch, "E10.0.2.95", {"start": v(-67.87, 47.63) * mm, "end": v(-75.2, 34.93) * mm});
            skCircle(sketch, "E10.0.2.96", {"center": v(-27.52, 47.63) * mm, "radius": 6.35 * mm});
            skLineSegment(sketch, "E10.0.2.97", {"start": v(-40.35, 63.5) * mm, "end": v(-47.68, 50.8) * mm});
            skLineSegment(sketch, "E10.0.2.98", {"start": v(-7.33, 50.8) * mm, "end": v(-14.66, 63.5) * mm});
            skLineSegment(sketch, "E10.0.2.99", {"start": v(75.18, 60.32) * mm, "end": v(89.85, 60.32) * mm});
            skLineSegment(sketch, "E10.0.2.100", {"start": v(117.37, 50.8) * mm, "end": v(102.7, 50.8) * mm});
            skLineSegment(sketch, "E10.0.2.101", {"start": v(144.86, 60.32) * mm, "end": v(152.2, 47.63) * mm});
            skLineSegment(sketch, "E10.0.2.102", {"start": v(150.38, 63.5) * mm, "end": v(157.72, 76.2) * mm});
            skLineSegment(sketch, "E10.0.2.103", {"start": v(172.38, 76.2) * mm, "end": v(179.71, 63.5) * mm});
            skCircle(sketch, "E10.0.2.104", {"center": v(-110.03, 63.5) * mm, "radius": 6.35 * mm});
            skLineSegment(sketch, "E10.0.2.105", {"start": v(-62.35, 76.2) * mm, "end": v(-47.68, 76.2) * mm});
            skLineSegment(sketch, "E10.0.2.106", {"start": v(34.83, 34.93) * mm, "end": v(20.16, 34.93) * mm});
            skLineSegment(sketch, "E10.0.2.107", {"start": v(67.85, 47.63) * mm, "end": v(75.18, 60.32) * mm});
            skLineSegment(sketch, "E10.0.2.108", {"start": v(-130.22, 60.32) * mm, "end": v(-122.89, 47.63) * mm});
            skLineSegment(sketch, "E10.0.2.109", {"start": v(-227.4, 50.8) * mm, "end": v(-234.73, 63.5) * mm});
            skLineSegment(sketch, "E10.0.2.110", {"start": v(185.21, 34.93) * mm, "end": v(177.88, 47.63) * mm});
            skCircle(sketch, "E10.0.2.111", {"center": v(-137.55, 47.63) * mm, "radius": 6.35 * mm});
            skLineSegment(sketch, "E10.0.2.112", {"start": v(-102.7, 76.2) * mm, "end": v(-95.37, 63.5) * mm});
            skLineSegment(sketch, "E10.0.2.113", {"start": v(-117.37, 50.8) * mm, "end": v(-124.7, 63.5) * mm});
            skLineSegment(sketch, "E10.0.2.114", {"start": v(-34.85, 60.32) * mm, "end": v(-20.19, 60.32) * mm});
            skLineSegment(sketch, "E10.0.2.115", {"start": v(-205.4, 63.5) * mm, "end": v(-212.73, 50.8) * mm});
            skLineSegment(sketch, "E10.0.2.116", {"start": v(-185.24, 34.93) * mm, "end": v(-199.9, 34.93) * mm});
            skLineSegment(sketch, "E10.0.2.117", {"start": v(-12.86, 47.63) * mm, "end": v(-20.19, 34.93) * mm});
            skLineSegment(sketch, "E10.0.2.118", {"start": v(7.33, 50.8) * mm, "end": v(-7.33, 50.8) * mm});
            skLineSegment(sketch, "E10.0.3.0", {"start": v(14.66, 95.25) * mm, "end": v(7.33, 82.55) * mm});
            skLineSegment(sketch, "E10.0.3.1", {"start": v(40.35, 95.25) * mm, "end": v(47.68, 107.95) * mm});
            skCircle(sketch, "E10.0.3.2", {"center": v(165.05, 95.25) * mm, "radius": 6.35 * mm});
            skLineSegment(sketch, "E10.0.3.3", {"start": v(-172.38, 107.95) * mm, "end": v(-157.72, 107.95) * mm});
            skLineSegment(sketch, "E10.0.3.4", {"start": v(212.73, 107.95) * mm, "end": v(227.4, 107.95) * mm});
            skLineSegment(sketch, "E10.0.3.5", {"start": v(-75.2, 66.68) * mm, "end": v(-89.87, 66.68) * mm});
            skLineSegment(sketch, "E10.0.3.6", {"start": v(199.88, 92.07) * mm, "end": v(207.21, 79.38) * mm});
            skLineSegment(sketch, "E10.0.3.7", {"start": v(-42.18, 79.38) * mm, "end": v(-34.85, 92.07) * mm});
            skLineSegment(sketch, "E10.0.3.8", {"start": v(227.4, 107.95) * mm, "end": v(234.73, 95.25) * mm});
            skLineSegment(sketch, "E10.0.3.9", {"start": v(75.18, 66.68) * mm, "end": v(67.85, 79.38) * mm});
            skCircle(sketch, "E10.0.3.10", {"center": v(137.53, 79.38) * mm, "radius": 6.35 * mm});
            skLineSegment(sketch, "E10.0.3.11", {"start": v(157.72, 82.55) * mm, "end": v(150.38, 95.25) * mm});
            skLineSegment(sketch, "E10.0.3.12", {"start": v(-144.89, 92.07) * mm, "end": v(-130.22, 92.07) * mm});
            skLineSegment(sketch, "E10.0.3.13", {"start": v(-75.2, 92.07) * mm, "end": v(-67.87, 79.38) * mm});
            skLineSegment(sketch, "E10.0.3.14", {"start": v(-102.7, 82.55) * mm, "end": v(-117.37, 82.55) * mm});
            skCircle(sketch, "E10.0.3.15", {"center": v(-192.57, 79.38) * mm, "radius": 6.35 * mm});
            skLineSegment(sketch, "E10.0.3.16", {"start": v(-69.68, 95.25) * mm, "end": v(-62.35, 107.95) * mm});
            skLineSegment(sketch, "E10.0.3.17", {"start": v(-47.68, 107.95) * mm, "end": v(-40.35, 95.25) * mm});
            skLineSegment(sketch, "E10.0.3.18", {"start": v(42.16, 79.38) * mm, "end": v(34.83, 66.68) * mm});
            skCircle(sketch, "E10.0.3.19", {"center": v(55.02, 95.25) * mm, "radius": 6.35 * mm});
            skLineSegment(sketch, "E10.0.3.20", {"start": v(102.7, 107.95) * mm, "end": v(117.37, 107.95) * mm});
            skLineSegment(sketch, "E10.0.3.21", {"start": v(69.68, 95.25) * mm, "end": v(62.35, 82.55) * mm});
            skLineSegment(sketch, "E10.0.3.22", {"start": v(-152.22, 79.38) * mm, "end": v(-144.89, 92.07) * mm});
            skLineSegment(sketch, "E10.0.3.23", {"start": v(-234.73, 95.25) * mm, "end": v(-227.4, 107.95) * mm});
            skLineSegment(sketch, "E10.0.3.24", {"start": v(199.88, 66.68) * mm, "end": v(185.21, 66.68) * mm});
            skLineSegment(sketch, "E10.0.3.25", {"start": v(-199.9, 92.07) * mm, "end": v(-185.24, 92.07) * mm});
            skLineSegment(sketch, "E10.0.3.26", {"start": v(-34.85, 66.68) * mm, "end": v(-42.18, 79.38) * mm});
            skCircle(sketch, "E10.0.3.27", {"center": v(27.5, 79.38) * mm, "radius": 6.35 * mm});
            skLineSegment(sketch, "E10.0.3.28", {"start": v(-199.9, 66.68) * mm, "end": v(-207.23, 79.38) * mm});
            skLineSegment(sketch, "E10.0.3.29", {"start": v(47.68, 82.55) * mm, "end": v(40.35, 95.25) * mm});
            skLineSegment(sketch, "E10.0.3.30", {"start": v(130.2, 92.07) * mm, "end": v(144.86, 92.07) * mm});
            skLineSegment(sketch, "E10.0.3.31", {"start": v(172.38, 82.55) * mm, "end": v(157.72, 82.55) * mm});
            skLineSegment(sketch, "E10.0.3.32", {"start": v(-179.71, 95.25) * mm, "end": v(-172.38, 107.95) * mm});
            skLineSegment(sketch, "E10.0.3.33", {"start": v(205.4, 95.25) * mm, "end": v(212.73, 107.95) * mm});
            skLineSegment(sketch, "E10.0.3.34", {"start": v(-20.19, 92.07) * mm, "end": v(-12.86, 79.38) * mm});
            skCircle(sketch, "E10.0.3.35", {"center": v(-55.02, 95.25) * mm, "radius": 6.35 * mm});
            skLineSegment(sketch, "E10.0.3.36", {"start": v(-7.33, 107.95) * mm, "end": v(7.33, 107.95) * mm});
            skLineSegment(sketch, "E10.0.3.37", {"start": v(7.33, 107.95) * mm, "end": v(14.66, 95.25) * mm});
            skLineSegment(sketch, "E10.0.3.38", {"start": v(89.85, 66.68) * mm, "end": v(75.18, 66.68) * mm});
            skLineSegment(sketch, "E10.0.3.39", {"start": v(97.18, 79.38) * mm, "end": v(89.85, 66.68) * mm});
            skLineSegment(sketch, "E10.0.3.40", {"start": v(122.86, 79.38) * mm, "end": v(130.2, 92.07) * mm});
            skLineSegment(sketch, "E10.0.3.41", {"start": v(-144.89, 66.68) * mm, "end": v(-152.22, 79.38) * mm});
            skCircle(sketch, "E10.0.3.42", {"center": v(-220.07, 95.25) * mm, "radius": 6.35 * mm});
            skLineSegment(sketch, "E10.0.3.43", {"start": v(124.7, 95.25) * mm, "end": v(117.37, 82.55) * mm});
            skCircle(sketch, "E10.0.3.44", {"center": v(-82.54, 79.38) * mm, "radius": 6.35 * mm});
            skLineSegment(sketch, "E10.0.3.45", {"start": v(-62.35, 82.55) * mm, "end": v(-69.68, 95.25) * mm});
            skLineSegment(sketch, "E10.0.3.46", {"start": v(20.16, 92.07) * mm, "end": v(34.83, 92.07) * mm});
            skLineSegment(sketch, "E10.0.3.47", {"start": v(62.35, 82.55) * mm, "end": v(47.68, 82.55) * mm});
            skLineSegment(sketch, "E10.0.3.48", {"start": v(95.37, 95.25) * mm, "end": v(102.7, 107.95) * mm});
            skCircle(sketch, "E10.0.3.49", {"center": v(-165.05, 95.25) * mm, "radius": 6.35 * mm});
            skLineSegment(sketch, "E10.0.3.50", {"start": v(-150.38, 95.25) * mm, "end": v(-157.72, 82.55) * mm});
            skCircle(sketch, "E10.0.3.51", {"center": v(220.07, 95.25) * mm, "radius": 6.35 * mm});
            skLineSegment(sketch, "E10.0.3.52", {"start": v(-185.24, 92.07) * mm, "end": v(-177.9, 79.38) * mm});
            skLineSegment(sketch, "E10.0.3.53", {"start": v(-117.37, 107.95) * mm, "end": v(-102.7, 107.95) * mm});
            skLineSegment(sketch, "E10.0.3.54", {"start": v(-227.4, 107.95) * mm, "end": v(-212.73, 107.95) * mm});
            skLineSegment(sketch, "E10.0.3.55", {"start": v(-20.19, 66.68) * mm, "end": v(-34.85, 66.68) * mm});
            skLineSegment(sketch, "E10.0.3.56", {"start": v(12.83, 79.38) * mm, "end": v(20.16, 92.07) * mm});
            skLineSegment(sketch, "E10.0.3.57", {"start": v(34.83, 92.07) * mm, "end": v(42.16, 79.38) * mm});
            skLineSegment(sketch, "E10.0.3.58", {"start": v(-207.23, 79.38) * mm, "end": v(-199.9, 92.07) * mm});
            skLineSegment(sketch, "E10.0.3.59", {"start": v(62.35, 107.95) * mm, "end": v(69.68, 95.25) * mm});
            skLineSegment(sketch, "E10.0.3.60", {"start": v(130.2, 66.68) * mm, "end": v(122.86, 79.38) * mm});
            skCircle(sketch, "E10.0.3.61", {"center": v(192.55, 79.38) * mm, "radius": 6.35 * mm});
            skLineSegment(sketch, "E10.0.3.62", {"start": v(-172.38, 82.55) * mm, "end": v(-179.71, 95.25) * mm});
            skLineSegment(sketch, "E10.0.3.63", {"start": v(152.2, 79.38) * mm, "end": v(144.86, 66.68) * mm});
            skLineSegment(sketch, "E10.0.3.64", {"start": v(212.73, 82.55) * mm, "end": v(205.4, 95.25) * mm});
            skLineSegment(sketch, "E10.0.3.65", {"start": v(-89.87, 92.07) * mm, "end": v(-75.2, 92.07) * mm});
            skLineSegment(sketch, "E10.0.3.66", {"start": v(179.71, 95.25) * mm, "end": v(172.38, 82.55) * mm});
            skLineSegment(sketch, "E10.0.3.67", {"start": v(-47.68, 82.55) * mm, "end": v(-62.35, 82.55) * mm});
            skLineSegment(sketch, "E10.0.3.68", {"start": v(-14.66, 95.25) * mm, "end": v(-7.33, 107.95) * mm});
            skCircle(sketch, "E10.0.3.69", {"center": v(110.03, 95.25) * mm, "radius": 6.35 * mm});
            skLineSegment(sketch, "E10.0.3.70", {"start": v(157.72, 107.95) * mm, "end": v(172.38, 107.95) * mm});
            skLineSegment(sketch, "E10.0.3.71", {"start": v(-122.89, 79.38) * mm, "end": v(-130.22, 66.68) * mm});
            skLineSegment(sketch, "E10.0.3.72", {"start": v(-130.22, 66.68) * mm, "end": v(-144.89, 66.68) * mm});
            skLineSegment(sketch, "E10.0.3.73", {"start": v(-97.2, 79.38) * mm, "end": v(-89.87, 92.07) * mm});
            skLineSegment(sketch, "E10.0.3.74", {"start": v(-95.37, 95.25) * mm, "end": v(-102.7, 82.55) * mm});
            skLineSegment(sketch, "E10.0.3.75", {"start": v(20.16, 66.68) * mm, "end": v(12.83, 79.38) * mm});
            skCircle(sketch, "E10.0.3.76", {"center": v(82.51, 79.38) * mm, "radius": 6.35 * mm});
            skLineSegment(sketch, "E10.0.3.77", {"start": v(89.85, 92.07) * mm, "end": v(97.18, 79.38) * mm});
            skLineSegment(sketch, "E10.0.3.78", {"start": v(102.7, 82.55) * mm, "end": v(95.37, 95.25) * mm});
            skLineSegment(sketch, "E10.0.3.79", {"start": v(-212.73, 82.55) * mm, "end": v(-227.4, 82.55) * mm});
            skLineSegment(sketch, "E10.0.3.80", {"start": v(185.21, 92.07) * mm, "end": v(199.88, 92.07) * mm});
            skLineSegment(sketch, "E10.0.3.81", {"start": v(-157.72, 82.55) * mm, "end": v(-172.38, 82.55) * mm});
            skLineSegment(sketch, "E10.0.3.82", {"start": v(117.37, 107.95) * mm, "end": v(124.7, 95.25) * mm});
            skLineSegment(sketch, "E10.0.3.83", {"start": v(227.4, 82.55) * mm, "end": v(212.73, 82.55) * mm});
            skLineSegment(sketch, "E10.0.3.84", {"start": v(-124.7, 95.25) * mm, "end": v(-117.37, 107.95) * mm});
            skLineSegment(sketch, "E10.0.3.85", {"start": v(207.21, 79.38) * mm, "end": v(199.88, 66.68) * mm});
            skLineSegment(sketch, "E10.0.3.86", {"start": v(-177.9, 79.38) * mm, "end": v(-185.24, 66.68) * mm});
            skLineSegment(sketch, "E10.0.3.87", {"start": v(-212.73, 107.95) * mm, "end": v(-205.4, 95.25) * mm});
            skLineSegment(sketch, "E10.0.3.88", {"start": v(234.73, 95.25) * mm, "end": v(227.4, 82.55) * mm});
            skCircle(sketch, "E10.0.3.89", {"center": v(0, 95.25) * mm, "radius": 6.35 * mm});
            skLineSegment(sketch, "E10.0.3.90", {"start": v(47.68, 107.95) * mm, "end": v(62.35, 107.95) * mm});
            skLineSegment(sketch, "E10.0.3.91", {"start": v(144.86, 66.68) * mm, "end": v(130.2, 66.68) * mm});
            skLineSegment(sketch, "E10.0.3.92", {"start": v(177.88, 79.38) * mm, "end": v(185.21, 92.07) * mm});
            skLineSegment(sketch, "E10.0.3.93", {"start": v(-157.72, 107.95) * mm, "end": v(-150.38, 95.25) * mm});
            skLineSegment(sketch, "E10.0.3.94", {"start": v(-89.87, 66.68) * mm, "end": v(-97.2, 79.38) * mm});
            skLineSegment(sketch, "E10.0.3.95", {"start": v(-67.87, 79.38) * mm, "end": v(-75.2, 66.68) * mm});
            skCircle(sketch, "E10.0.3.96", {"center": v(-27.52, 79.38) * mm, "radius": 6.35 * mm});
            skLineSegment(sketch, "E10.0.3.97", {"start": v(-40.35, 95.25) * mm, "end": v(-47.68, 82.55) * mm});
            skLineSegment(sketch, "E10.0.3.98", {"start": v(-7.33, 82.55) * mm, "end": v(-14.66, 95.25) * mm});
            skLineSegment(sketch, "E10.0.3.99", {"start": v(75.18, 92.07) * mm, "end": v(89.85, 92.07) * mm});
            skLineSegment(sketch, "E10.0.3.100", {"start": v(117.37, 82.55) * mm, "end": v(102.7, 82.55) * mm});
            skLineSegment(sketch, "E10.0.3.101", {"start": v(144.86, 92.07) * mm, "end": v(152.2, 79.38) * mm});
            skLineSegment(sketch, "E10.0.3.102", {"start": v(150.38, 95.25) * mm, "end": v(157.72, 107.95) * mm});
            skLineSegment(sketch, "E10.0.3.103", {"start": v(172.38, 107.95) * mm, "end": v(179.71, 95.25) * mm});
            skCircle(sketch, "E10.0.3.104", {"center": v(-110.03, 95.25) * mm, "radius": 6.35 * mm});
            skLineSegment(sketch, "E10.0.3.105", {"start": v(-62.35, 107.95) * mm, "end": v(-47.68, 107.95) * mm});
            skLineSegment(sketch, "E10.0.3.106", {"start": v(34.83, 66.68) * mm, "end": v(20.16, 66.68) * mm});
            skLineSegment(sketch, "E10.0.3.107", {"start": v(67.85, 79.38) * mm, "end": v(75.18, 92.07) * mm});
            skLineSegment(sketch, "E10.0.3.108", {"start": v(-130.22, 92.07) * mm, "end": v(-122.89, 79.38) * mm});
            skLineSegment(sketch, "E10.0.3.109", {"start": v(-227.4, 82.55) * mm, "end": v(-234.73, 95.25) * mm});
            skLineSegment(sketch, "E10.0.3.110", {"start": v(185.21, 66.68) * mm, "end": v(177.88, 79.38) * mm});
            skCircle(sketch, "E10.0.3.111", {"center": v(-137.55, 79.38) * mm, "radius": 6.35 * mm});
            skLineSegment(sketch, "E10.0.3.112", {"start": v(-102.7, 107.95) * mm, "end": v(-95.37, 95.25) * mm});
            skLineSegment(sketch, "E10.0.3.113", {"start": v(-117.37, 82.55) * mm, "end": v(-124.7, 95.25) * mm});
            skLineSegment(sketch, "E10.0.3.114", {"start": v(-34.85, 92.07) * mm, "end": v(-20.19, 92.07) * mm});
            skLineSegment(sketch, "E10.0.3.115", {"start": v(-205.4, 95.25) * mm, "end": v(-212.73, 82.55) * mm});
            skLineSegment(sketch, "E10.0.3.116", {"start": v(-185.24, 66.68) * mm, "end": v(-199.9, 66.68) * mm});
            skLineSegment(sketch, "E10.0.3.117", {"start": v(-12.86, 79.38) * mm, "end": v(-20.19, 66.68) * mm});
            skLineSegment(sketch, "E10.0.3.118", {"start": v(7.33, 82.55) * mm, "end": v(-7.33, 82.55) * mm});
            skLineSegment(sketch, "E10.direction1", {"start": v(-220.07, 0) * mm, "end": v(-205.4, 0) * mm, "construction": true});
            skLineSegment(sketch, "E10.direction2", {"start": v(-220.07, 0) * mm, "end": v(-220.07, 31.75) * mm, "construction": true});
            skLineSegment(sketch, "E11", {"start": v(-223.24, 12.7) * mm, "end": v(-223.24, 19.05) * mm});
            skLineSegment(sketch, "E12", {"start": v(-216.9, 82.55) * mm, "end": v(-216.9, 76.2) * mm});
            skLineSegment(sketch, "E13.trimOffspring", {"start": v(-223.24, 76.2) * mm, "end": v(-223.24, 82.55) * mm});
            skLineSegment(sketch, "E14.trimOffspring", {"start": v(-216.9, 50.8) * mm, "end": v(-216.9, 44.45) * mm});
            skLineSegment(sketch, "E15.trimOffspring", {"start": v(-223.24, 44.45) * mm, "end": v(-223.24, 50.8) * mm});
            skLineSegment(sketch, "E16.trimOffspring", {"start": v(-216.9, 19.05) * mm, "end": v(-216.9, 12.7) * mm});
            skLineSegment(sketch, "E17", {"start": v(-210.64, 86.18) * mm, "end": v(-205.14, 83) * mm});
            skLineSegment(sketch, "E18.trimOffspring", {"start": v(-36.93, -6.78) * mm, "end": v(-42.43, -3.6) * mm});
            skLineSegment(sketch, "E19.trimOffspring", {"start": v(-201.96, 88.5) * mm, "end": v(-207.46, 91.68) * mm});
            skLineSegment(sketch, "E20.trimOffspring", {"start": v(-183.14, 70.3) * mm, "end": v(-177.62, 67.12) * mm});
            skLineSegment(sketch, "E21.trimOffspring", {"start": v(-174.45, 72.62) * mm, "end": v(-179.97, 75.8) * mm});
            skLineSegment(sketch, "E22.trimOffspring", {"start": v(-155.63, 54.42) * mm, "end": v(-150.13, 51.25) * mm});
            skLineSegment(sketch, "E23.trimOffspring", {"start": v(-146.95, 56.75) * mm, "end": v(-152.45, 59.92) * mm});
            skLineSegment(sketch, "E24.trimOffspring", {"start": v(-128.13, 38.55) * mm, "end": v(-122.61, 35.36) * mm});
            skLineSegment(sketch, "E25.trimOffspring", {"start": v(-119.44, 40.86) * mm, "end": v(-124.95, 44.05) * mm});
            skLineSegment(sketch, "E26.trimOffspring", {"start": v(-100.62, 22.66) * mm, "end": v(-95.12, 19.49) * mm});
            skLineSegment(sketch, "E27.trimOffspring", {"start": v(-91.94, 24.98) * mm, "end": v(-97.44, 28.16) * mm});
            skLineSegment(sketch, "E28.trimOffspring", {"start": v(-73.12, 6.79) * mm, "end": v(-67.6, 3.6) * mm});
            skLineSegment(sketch, "E29.trimOffspring", {"start": v(-64.43, 9.1) * mm, "end": v(-69.94, 12.28) * mm});
            skLineSegment(sketch, "E30.trimOffspring", {"start": v(-45.6, -9.1) * mm, "end": v(-40.1, -12.27) * mm});
            skLineSegment(sketch, "E31.1.0.0", {"start": v(-161.96, 82.55) * mm, "end": v(-161.96, 76.2) * mm});
            skLineSegment(sketch, "E31.1.0.1", {"start": v(-168.31, 76.2) * mm, "end": v(-168.31, 82.55) * mm});
            skLineSegment(sketch, "E31.1.0.2", {"start": v(-161.96, 50.8) * mm, "end": v(-161.96, 44.45) * mm});
            skLineSegment(sketch, "E31.1.0.3", {"start": v(-168.31, 44.45) * mm, "end": v(-168.31, 50.8) * mm});
            skLineSegment(sketch, "E31.1.0.4", {"start": v(-168.31, 12.7) * mm, "end": v(-168.31, 19.05) * mm});
            skLineSegment(sketch, "E31.1.0.5", {"start": v(-161.96, 19.05) * mm, "end": v(-161.96, 12.7) * mm});
            skLineSegment(sketch, "E31.2.0.0", {"start": v(-107.04, 82.55) * mm, "end": v(-107.04, 76.2) * mm});
            skLineSegment(sketch, "E31.2.0.1", {"start": v(-113.39, 76.2) * mm, "end": v(-113.39, 82.55) * mm});
            skLineSegment(sketch, "E31.2.0.2", {"start": v(-107.04, 50.8) * mm, "end": v(-107.04, 44.45) * mm});
            skLineSegment(sketch, "E31.2.0.3", {"start": v(-113.39, 44.45) * mm, "end": v(-113.39, 50.8) * mm});
            skLineSegment(sketch, "E31.2.0.4", {"start": v(-113.39, 12.7) * mm, "end": v(-113.39, 19.05) * mm});
            skLineSegment(sketch, "E31.2.0.5", {"start": v(-107.04, 19.05) * mm, "end": v(-107.04, 12.7) * mm});
            skLineSegment(sketch, "E31.3.0.0", {"start": v(-52.1, 82.55) * mm, "end": v(-52.1, 76.2) * mm});
            skLineSegment(sketch, "E31.3.0.1", {"start": v(-58.46, 76.2) * mm, "end": v(-58.46, 82.55) * mm});
            skLineSegment(sketch, "E31.3.0.2", {"start": v(-52.1, 50.8) * mm, "end": v(-52.1, 44.45) * mm});
            skLineSegment(sketch, "E31.3.0.3", {"start": v(-58.46, 44.45) * mm, "end": v(-58.46, 50.8) * mm});
            skLineSegment(sketch, "E31.3.0.4", {"start": v(-58.46, 12.7) * mm, "end": v(-58.46, 19.05) * mm});
            skLineSegment(sketch, "E31.3.0.5", {"start": v(-52.1, 19.05) * mm, "end": v(-52.1, 12.7) * mm});
            skLineSegment(sketch, "E31.4.0.0", {"start": v(2.82, 82.55) * mm, "end": v(2.82, 76.2) * mm});
            skLineSegment(sketch, "E31.4.0.1", {"start": v(-3.53, 76.2) * mm, "end": v(-3.53, 82.55) * mm});
            skLineSegment(sketch, "E31.4.0.2", {"start": v(2.82, 50.8) * mm, "end": v(2.82, 44.45) * mm});
            skLineSegment(sketch, "E31.4.0.3", {"start": v(-3.53, 44.45) * mm, "end": v(-3.53, 50.8) * mm});
            skLineSegment(sketch, "E31.4.0.4", {"start": v(-3.53, 12.7) * mm, "end": v(-3.53, 19.05) * mm});
            skLineSegment(sketch, "E31.4.0.5", {"start": v(2.82, 19.05) * mm, "end": v(2.82, 12.7) * mm});
            skLineSegment(sketch, "E31.5.0.0", {"start": v(57.75, 82.55) * mm, "end": v(57.75, 76.2) * mm});
            skLineSegment(sketch, "E31.5.0.1", {"start": v(51.4, 76.2) * mm, "end": v(51.4, 82.55) * mm});
            skLineSegment(sketch, "E31.5.0.2", {"start": v(57.75, 50.8) * mm, "end": v(57.75, 44.45) * mm});
            skLineSegment(sketch, "E31.5.0.3", {"start": v(51.4, 44.45) * mm, "end": v(51.4, 50.8) * mm});
            skLineSegment(sketch, "E31.5.0.4", {"start": v(51.4, 12.7) * mm, "end": v(51.4, 19.05) * mm});
            skLineSegment(sketch, "E31.5.0.5", {"start": v(57.75, 19.05) * mm, "end": v(57.75, 12.7) * mm});
            skLineSegment(sketch, "E31.6.0.0", {"start": v(112.67, 82.55) * mm, "end": v(112.67, 76.2) * mm});
            skLineSegment(sketch, "E31.6.0.1", {"start": v(106.32, 76.2) * mm, "end": v(106.32, 82.55) * mm});
            skLineSegment(sketch, "E31.6.0.2", {"start": v(112.67, 50.8) * mm, "end": v(112.67, 44.45) * mm});
            skLineSegment(sketch, "E31.6.0.3", {"start": v(106.32, 44.45) * mm, "end": v(106.32, 50.8) * mm});
            skLineSegment(sketch, "E31.6.0.4", {"start": v(106.32, 12.7) * mm, "end": v(106.32, 19.05) * mm});
            skLineSegment(sketch, "E31.6.0.5", {"start": v(112.67, 19.05) * mm, "end": v(112.67, 12.7) * mm});
            skLineSegment(sketch, "E31.7.0.0", {"start": v(167.6, 82.55) * mm, "end": v(167.6, 76.2) * mm});
            skLineSegment(sketch, "E31.7.0.1", {"start": v(161.25, 76.2) * mm, "end": v(161.25, 82.55) * mm});
            skLineSegment(sketch, "E31.7.0.2", {"start": v(167.6, 50.8) * mm, "end": v(167.6, 44.45) * mm});
            skLineSegment(sketch, "E31.7.0.3", {"start": v(161.25, 44.45) * mm, "end": v(161.25, 50.8) * mm});
            skLineSegment(sketch, "E31.7.0.4", {"start": v(161.25, 12.7) * mm, "end": v(161.25, 19.05) * mm});
            skLineSegment(sketch, "E31.7.0.5", {"start": v(167.6, 19.05) * mm, "end": v(167.6, 12.7) * mm});
            skLineSegment(sketch, "E31.8.0.0", {"start": v(222.53, 82.55) * mm, "end": v(222.53, 76.2) * mm});
            skLineSegment(sketch, "E31.8.0.1", {"start": v(216.18, 76.2) * mm, "end": v(216.18, 82.55) * mm});
            skLineSegment(sketch, "E31.8.0.2", {"start": v(222.53, 50.8) * mm, "end": v(222.53, 44.45) * mm});
            skLineSegment(sketch, "E31.8.0.3", {"start": v(216.18, 44.45) * mm, "end": v(216.18, 50.8) * mm});
            skLineSegment(sketch, "E31.8.0.4", {"start": v(216.18, 12.7) * mm, "end": v(216.18, 19.05) * mm});
            skLineSegment(sketch, "E31.8.0.5", {"start": v(222.53, 19.05) * mm, "end": v(222.53, 12.7) * mm});
            skLineSegment(sketch, "E31.direction1", {"start": v(-223.24, 12.7) * mm, "end": v(-168.31, 12.7) * mm, "construction": true});
            skLineSegment(sketch, "E32", {"start": v(-195.74, 66.68) * mm, "end": v(-195.74, 60.32) * mm});
            skLineSegment(sketch, "E33", {"start": v(-189.4, 66.68) * mm, "end": v(-189.4, 60.32) * mm});
            skLineSegment(sketch, "E34.trimOffspring", {"start": v(-195.74, 34.93) * mm, "end": v(-195.74, 28.57) * mm});
            skLineSegment(sketch, "E35.trimOffspring", {"start": v(-195.74, 3.18) * mm, "end": v(-195.74, -3.18) * mm});
            skLineSegment(sketch, "E36.trimOffspring", {"start": v(-189.4, 34.93) * mm, "end": v(-189.4, 28.57) * mm});
            skLineSegment(sketch, "E37.trimOffspring", {"start": v(-189.4, 3.18) * mm, "end": v(-189.4, -3.18) * mm});
            skLineSegment(sketch, "E38.1.0.0", {"start": v(-134.47, 34.93) * mm, "end": v(-134.47, 28.57) * mm});
            skLineSegment(sketch, "E38.1.0.1", {"start": v(-140.82, 66.68) * mm, "end": v(-140.82, 60.32) * mm});
            skLineSegment(sketch, "E38.1.0.2", {"start": v(-140.82, 3.18) * mm, "end": v(-140.82, -3.18) * mm});
            skLineSegment(sketch, "E38.1.0.3", {"start": v(-134.47, 3.18) * mm, "end": v(-134.47, -3.18) * mm});
            skLineSegment(sketch, "E38.1.0.4", {"start": v(-140.82, 34.93) * mm, "end": v(-140.82, 28.57) * mm});
            skLineSegment(sketch, "E38.1.0.5", {"start": v(-134.47, 66.68) * mm, "end": v(-134.47, 60.32) * mm});
            skLineSegment(sketch, "E38.2.0.0", {"start": v(-79.54, 34.93) * mm, "end": v(-79.54, 28.57) * mm});
            skLineSegment(sketch, "E38.2.0.1", {"start": v(-85.89, 66.68) * mm, "end": v(-85.89, 60.32) * mm});
            skLineSegment(sketch, "E38.2.0.2", {"start": v(-85.89, 3.18) * mm, "end": v(-85.89, -3.18) * mm});
            skLineSegment(sketch, "E38.2.0.3", {"start": v(-79.54, 3.18) * mm, "end": v(-79.54, -3.18) * mm});
            skLineSegment(sketch, "E38.2.0.4", {"start": v(-85.89, 34.93) * mm, "end": v(-85.89, 28.57) * mm});
            skLineSegment(sketch, "E38.2.0.5", {"start": v(-79.54, 66.68) * mm, "end": v(-79.54, 60.32) * mm});
            skLineSegment(sketch, "E38.3.0.0", {"start": v(-24.61, 34.93) * mm, "end": v(-24.61, 28.57) * mm});
            skLineSegment(sketch, "E38.3.0.1", {"start": v(-30.96, 66.68) * mm, "end": v(-30.96, 60.32) * mm});
            skLineSegment(sketch, "E38.3.0.2", {"start": v(-30.96, 3.18) * mm, "end": v(-30.96, -3.18) * mm});
            skLineSegment(sketch, "E38.3.0.3", {"start": v(-24.61, 3.18) * mm, "end": v(-24.61, -3.18) * mm});
            skLineSegment(sketch, "E38.3.0.4", {"start": v(-30.96, 34.93) * mm, "end": v(-30.96, 28.57) * mm});
            skLineSegment(sketch, "E38.3.0.5", {"start": v(-24.61, 66.68) * mm, "end": v(-24.61, 60.32) * mm});
            skLineSegment(sketch, "E38.4.0.0", {"start": v(30.32, 34.93) * mm, "end": v(30.32, 28.57) * mm});
            skLineSegment(sketch, "E38.4.0.1", {"start": v(23.97, 66.68) * mm, "end": v(23.97, 60.32) * mm});
            skLineSegment(sketch, "E38.4.0.2", {"start": v(23.97, 3.18) * mm, "end": v(23.97, -3.18) * mm});
            skLineSegment(sketch, "E38.4.0.3", {"start": v(30.32, 3.18) * mm, "end": v(30.32, -3.18) * mm});
            skLineSegment(sketch, "E38.4.0.4", {"start": v(23.97, 34.93) * mm, "end": v(23.97, 28.57) * mm});
            skLineSegment(sketch, "E38.4.0.5", {"start": v(30.32, 66.68) * mm, "end": v(30.32, 60.32) * mm});
            skLineSegment(sketch, "E38.5.0.0", {"start": v(85.24, 34.93) * mm, "end": v(85.24, 28.57) * mm});
            skLineSegment(sketch, "E38.5.0.1", {"start": v(78.9, 66.68) * mm, "end": v(78.9, 60.32) * mm});
            skLineSegment(sketch, "E38.5.0.2", {"start": v(78.9, 3.18) * mm, "end": v(78.9, -3.18) * mm});
            skLineSegment(sketch, "E38.5.0.3", {"start": v(85.24, 3.18) * mm, "end": v(85.24, -3.18) * mm});
            skLineSegment(sketch, "E38.5.0.4", {"start": v(78.9, 34.93) * mm, "end": v(78.9, 28.57) * mm});
            skLineSegment(sketch, "E38.5.0.5", {"start": v(85.24, 66.68) * mm, "end": v(85.24, 60.32) * mm});
            skLineSegment(sketch, "E38.6.0.0", {"start": v(140.17, 34.93) * mm, "end": v(140.17, 28.57) * mm});
            skLineSegment(sketch, "E38.6.0.1", {"start": v(133.82, 66.68) * mm, "end": v(133.82, 60.32) * mm});
            skLineSegment(sketch, "E38.6.0.2", {"start": v(133.82, 3.18) * mm, "end": v(133.82, -3.18) * mm});
            skLineSegment(sketch, "E38.6.0.3", {"start": v(140.17, 3.18) * mm, "end": v(140.17, -3.18) * mm});
            skLineSegment(sketch, "E38.6.0.4", {"start": v(133.82, 34.93) * mm, "end": v(133.82, 28.57) * mm});
            skLineSegment(sketch, "E38.6.0.5", {"start": v(140.17, 66.68) * mm, "end": v(140.17, 60.32) * mm});
            skLineSegment(sketch, "E38.7.0.0", {"start": v(195.1, 34.93) * mm, "end": v(195.1, 28.57) * mm});
            skLineSegment(sketch, "E38.7.0.1", {"start": v(188.75, 66.68) * mm, "end": v(188.75, 60.32) * mm});
            skLineSegment(sketch, "E38.7.0.2", {"start": v(188.75, 3.18) * mm, "end": v(188.75, -3.18) * mm});
            skLineSegment(sketch, "E38.7.0.3", {"start": v(195.1, 3.18) * mm, "end": v(195.1, -3.18) * mm});
            skLineSegment(sketch, "E38.7.0.4", {"start": v(188.75, 34.93) * mm, "end": v(188.75, 28.57) * mm});
            skLineSegment(sketch, "E38.7.0.5", {"start": v(195.1, 66.68) * mm, "end": v(195.1, 60.32) * mm});
            skLineSegment(sketch, "E38.direction1", {"start": v(-195.74, -3.18) * mm, "end": v(-140.82, -3.18) * mm, "construction": true});
            skLineSegment(sketch, "E39.1.0.0", {"start": v(-64.42, 40.86) * mm, "end": v(-69.94, 44.05) * mm});
            skLineSegment(sketch, "E39.1.0.1", {"start": v(-18.1, 6.79) * mm, "end": v(-12.59, 3.6) * mm});
            skLineSegment(sketch, "E39.1.0.2", {"start": v(-100.6, 54.42) * mm, "end": v(-95.11, 51.25) * mm});
            skLineSegment(sketch, "E39.1.0.3", {"start": v(-36.93, 24.98) * mm, "end": v(-42.42, 28.16) * mm});
            skLineSegment(sketch, "E39.1.0.4", {"start": v(-9.41, 9.1) * mm, "end": v(-14.93, 12.28) * mm});
            skLineSegment(sketch, "E39.1.0.5", {"start": v(-73.11, 38.55) * mm, "end": v(-67.6, 35.36) * mm});
            skLineSegment(sketch, "E39.1.0.6", {"start": v(-45.6, 22.66) * mm, "end": v(-40.1, 19.49) * mm});
            skLineSegment(sketch, "E39.1.0.7", {"start": v(-91.94, 56.75) * mm, "end": v(-97.43, 59.92) * mm});
            skLineSegment(sketch, "E39.1.0.8", {"start": v(-155.62, 86.18) * mm, "end": v(-150.12, 83) * mm});
            skLineSegment(sketch, "E39.1.0.9", {"start": v(-146.95, 88.5) * mm, "end": v(-152.45, 91.68) * mm});
            skLineSegment(sketch, "E39.1.0.10", {"start": v(18.09, -6.78) * mm, "end": v(12.59, -3.6) * mm});
            skLineSegment(sketch, "E39.1.0.11", {"start": v(-128.12, 70.3) * mm, "end": v(-122.6, 67.12) * mm});
            skLineSegment(sketch, "E39.1.0.12", {"start": v(9.41, -9.1) * mm, "end": v(14.91, -12.27) * mm});
            skLineSegment(sketch, "E39.1.0.13", {"start": v(-119.43, 72.62) * mm, "end": v(-124.95, 75.8) * mm});
            skLineSegment(sketch, "E39.2.0.0", {"start": v(-9.4, 40.86) * mm, "end": v(-14.92, 44.05) * mm});
            skLineSegment(sketch, "E39.2.0.1", {"start": v(36.91, 6.79) * mm, "end": v(42.43, 3.6) * mm});
            skLineSegment(sketch, "E39.2.0.2", {"start": v(-45.6, 54.42) * mm, "end": v(-40.1, 51.25) * mm});
            skLineSegment(sketch, "E39.2.0.3", {"start": v(18.1, 24.98) * mm, "end": v(12.6, 28.16) * mm});
            skLineSegment(sketch, "E39.2.0.4", {"start": v(45.6, 9.1) * mm, "end": v(40.09, 12.28) * mm});
            skLineSegment(sketch, "E39.2.0.5", {"start": v(-18.1, 38.55) * mm, "end": v(-12.58, 35.36) * mm});
            skLineSegment(sketch, "E39.2.0.6", {"start": v(9.42, 22.66) * mm, "end": v(14.92, 19.49) * mm});
            skLineSegment(sketch, "E39.2.0.7", {"start": v(-36.92, 56.75) * mm, "end": v(-42.42, 59.92) * mm});
            skLineSegment(sketch, "E39.2.0.8", {"start": v(-100.6, 86.18) * mm, "end": v(-95.1, 83) * mm});
            skLineSegment(sketch, "E39.2.0.9", {"start": v(-91.93, 88.5) * mm, "end": v(-97.43, 91.68) * mm});
            skLineSegment(sketch, "E39.2.0.10", {"start": v(73.1, -6.78) * mm, "end": v(67.6, -3.6) * mm});
            skLineSegment(sketch, "E39.2.0.11", {"start": v(-73.1, 70.3) * mm, "end": v(-67.6, 67.12) * mm});
            skLineSegment(sketch, "E39.2.0.12", {"start": v(64.43, -9.1) * mm, "end": v(69.93, -12.27) * mm});
            skLineSegment(sketch, "E39.2.0.13", {"start": v(-64.42, 72.62) * mm, "end": v(-69.93, 75.8) * mm});
            skLineSegment(sketch, "E39.3.0.0", {"start": v(45.61, 40.86) * mm, "end": v(40.1, 44.05) * mm});
            skLineSegment(sketch, "E39.3.0.1", {"start": v(91.93, 6.79) * mm, "end": v(97.45, 3.6) * mm});
            skLineSegment(sketch, "E39.3.0.2", {"start": v(9.42, 54.42) * mm, "end": v(14.92, 51.25) * mm});
            skLineSegment(sketch, "E39.3.0.3", {"start": v(73.1, 24.98) * mm, "end": v(67.6, 28.16) * mm});
            skLineSegment(sketch, "E39.3.0.4", {"start": v(100.62, 9.1) * mm, "end": v(95.1, 12.28) * mm});
            skLineSegment(sketch, "E39.3.0.5", {"start": v(36.92, 38.55) * mm, "end": v(42.44, 35.36) * mm});
            skLineSegment(sketch, "E39.3.0.6", {"start": v(64.43, 22.66) * mm, "end": v(69.93, 19.49) * mm});
            skLineSegment(sketch, "E39.3.0.7", {"start": v(18.1, 56.75) * mm, "end": v(12.6, 59.92) * mm});
            skLineSegment(sketch, "E39.3.0.8", {"start": v(-45.59, 86.18) * mm, "end": v(-40.09, 83) * mm});
            skLineSegment(sketch, "E39.3.0.9", {"start": v(-36.91, 88.5) * mm, "end": v(-42.41, 91.68) * mm});
            skLineSegment(sketch, "E39.3.0.10", {"start": v(128.12, -6.78) * mm, "end": v(122.62, -3.6) * mm});
            skLineSegment(sketch, "E39.3.0.11", {"start": v(-18.1, 70.3) * mm, "end": v(-12.57, 67.12) * mm});
            skLineSegment(sketch, "E39.3.0.12", {"start": v(119.44, -9.1) * mm, "end": v(124.94, -12.27) * mm});
            skLineSegment(sketch, "E39.3.0.13", {"start": v(-9.4, 72.62) * mm, "end": v(-14.92, 75.8) * mm});
            skLineSegment(sketch, "E39.4.0.0", {"start": v(100.63, 40.86) * mm, "end": v(95.11, 44.05) * mm});
            skLineSegment(sketch, "E39.4.0.1", {"start": v(146.95, 6.79) * mm, "end": v(152.46, 3.6) * mm});
            skLineSegment(sketch, "E39.4.0.2", {"start": v(64.44, 54.42) * mm, "end": v(69.94, 51.25) * mm});
            skLineSegment(sketch, "E39.4.0.3", {"start": v(128.12, 24.98) * mm, "end": v(122.62, 28.16) * mm});
            skLineSegment(sketch, "E39.4.0.4", {"start": v(155.64, 9.1) * mm, "end": v(150.12, 12.28) * mm});
            skLineSegment(sketch, "E39.4.0.5", {"start": v(91.94, 38.55) * mm, "end": v(97.45, 35.36) * mm});
            skLineSegment(sketch, "E39.4.0.6", {"start": v(119.45, 22.66) * mm, "end": v(124.95, 19.49) * mm});
            skLineSegment(sketch, "E39.4.0.7", {"start": v(73.11, 56.75) * mm, "end": v(67.61, 59.92) * mm});
            skLineSegment(sketch, "E39.4.0.8", {"start": v(9.43, 86.18) * mm, "end": v(14.93, 83) * mm});
            skLineSegment(sketch, "E39.4.0.9", {"start": v(18.1, 88.5) * mm, "end": v(12.6, 91.68) * mm});
            skLineSegment(sketch, "E39.4.0.10", {"start": v(183.13, -6.78) * mm, "end": v(177.64, -3.6) * mm});
            skLineSegment(sketch, "E39.4.0.11", {"start": v(36.93, 70.3) * mm, "end": v(42.44, 67.12) * mm});
            skLineSegment(sketch, "E39.4.0.12", {"start": v(174.46, -9.1) * mm, "end": v(179.96, -12.27) * mm});
            skLineSegment(sketch, "E39.4.0.13", {"start": v(45.62, 72.62) * mm, "end": v(40.1, 75.8) * mm});
            skLineSegment(sketch, "E39.direction1", {"start": v(-36.93, -6.78) * mm, "end": v(18.09, -6.78) * mm, "construction": true});
            skLineSegment(sketch, "E40", {"start": v(-183.13, -6.82) * mm, "end": v(-177.62, -3.63) * mm});
            skLineSegment(sketch, "E41", {"start": v(-179.96, -12.32) * mm, "end": v(-174.44, -9.13) * mm});
            skLineSegment(sketch, "E42.trimOffspring", {"start": v(-155.62, 9.07) * mm, "end": v(-150.12, 12.24) * mm});
            skLineSegment(sketch, "E43.trimOffspring", {"start": v(-152.45, 3.57) * mm, "end": v(-146.95, 6.74) * mm});
            skLineSegment(sketch, "E44.trimOffspring", {"start": v(-124.95, 19.44) * mm, "end": v(-119.43, 22.63) * mm});
            skLineSegment(sketch, "E45.trimOffspring", {"start": v(-128.12, 24.94) * mm, "end": v(-122.6, 28.13) * mm});
            skLineSegment(sketch, "E46.trimOffspring", {"start": v(-100.6, 40.83) * mm, "end": v(-95.11, 44) * mm});
            skLineSegment(sketch, "E47.trimOffspring", {"start": v(-97.43, 35.33) * mm, "end": v(-91.94, 38.5) * mm});
            skLineSegment(sketch, "E48.trimOffspring", {"start": v(-69.94, 51.2) * mm, "end": v(-64.42, 54.4) * mm});
            skLineSegment(sketch, "E49.trimOffspring", {"start": v(-73.11, 56.7) * mm, "end": v(-67.6, 59.89) * mm});
            skLineSegment(sketch, "E50.trimOffspring", {"start": v(-42.42, 67.1) * mm, "end": v(-36.93, 70.27) * mm});
            skLineSegment(sketch, "E51.trimOffspring", {"start": v(-45.6, 72.59) * mm, "end": v(-40.1, 75.76) * mm});
            skLineSegment(sketch, "E52.trimOffspring", {"start": v(-14.93, 82.97) * mm, "end": v(-9.41, 86.15) * mm});
            skLineSegment(sketch, "E53.trimOffspring", {"start": v(-18.1, 88.46) * mm, "end": v(-12.59, 91.65) * mm});
            skLineSegment(sketch, "E54.1.0.0", {"start": v(-69.93, 19.44) * mm, "end": v(-64.42, 22.63) * mm});
            skLineSegment(sketch, "E54.1.0.1", {"start": v(-97.43, 3.57) * mm, "end": v(-91.93, 6.74) * mm});
            skLineSegment(sketch, "E54.1.0.2", {"start": v(-73.1, 24.94) * mm, "end": v(-67.6, 28.13) * mm});
            skLineSegment(sketch, "E54.1.0.3", {"start": v(12.6, 67.1) * mm, "end": v(18.1, 70.27) * mm});
            skLineSegment(sketch, "E54.1.0.4", {"start": v(40.09, 82.97) * mm, "end": v(45.6, 86.15) * mm});
            skLineSegment(sketch, "E54.1.0.5", {"start": v(-14.92, 51.2) * mm, "end": v(-9.4, 54.4) * mm});
            skLineSegment(sketch, "E54.1.0.6", {"start": v(-124.94, -12.32) * mm, "end": v(-119.43, -9.13) * mm});
            skLineSegment(sketch, "E54.1.0.7", {"start": v(-100.6, 9.07) * mm, "end": v(-95.1, 12.24) * mm});
            skLineSegment(sketch, "E54.1.0.8", {"start": v(-42.42, 35.33) * mm, "end": v(-36.92, 38.5) * mm});
            skLineSegment(sketch, "E54.1.0.9", {"start": v(-128.12, -6.82) * mm, "end": v(-122.6, -3.63) * mm});
            skLineSegment(sketch, "E54.1.0.10", {"start": v(-18.1, 56.7) * mm, "end": v(-12.58, 59.89) * mm});
            skLineSegment(sketch, "E54.1.0.11", {"start": v(9.42, 72.59) * mm, "end": v(14.92, 75.76) * mm});
            skLineSegment(sketch, "E54.1.0.12", {"start": v(-45.6, 40.83) * mm, "end": v(-40.1, 44) * mm});
            skLineSegment(sketch, "E54.1.0.13", {"start": v(36.91, 88.46) * mm, "end": v(42.43, 91.65) * mm});
            skLineSegment(sketch, "E54.2.0.0", {"start": v(-14.92, 19.44) * mm, "end": v(-9.4, 22.63) * mm});
            skLineSegment(sketch, "E54.2.0.1", {"start": v(-42.41, 3.57) * mm, "end": v(-36.91, 6.74) * mm});
            skLineSegment(sketch, "E54.2.0.2", {"start": v(-18.1, 24.94) * mm, "end": v(-12.57, 28.13) * mm});
            skLineSegment(sketch, "E54.2.0.3", {"start": v(67.6, 67.1) * mm, "end": v(73.1, 70.27) * mm});
            skLineSegment(sketch, "E54.2.0.4", {"start": v(95.1, 82.97) * mm, "end": v(100.62, 86.15) * mm});
            skLineSegment(sketch, "E54.2.0.5", {"start": v(40.1, 51.2) * mm, "end": v(45.61, 54.4) * mm});
            skLineSegment(sketch, "E54.2.0.6", {"start": v(-69.93, -12.32) * mm, "end": v(-64.4, -9.13) * mm});
            skLineSegment(sketch, "E54.2.0.7", {"start": v(-45.59, 9.07) * mm, "end": v(-40.09, 12.24) * mm});
            skLineSegment(sketch, "E54.2.0.8", {"start": v(12.6, 35.33) * mm, "end": v(18.1, 38.5) * mm});
            skLineSegment(sketch, "E54.2.0.9", {"start": v(-73.1, -6.82) * mm, "end": v(-67.58, -3.63) * mm});
            skLineSegment(sketch, "E54.2.0.10", {"start": v(36.92, 56.7) * mm, "end": v(42.44, 59.89) * mm});
            skLineSegment(sketch, "E54.2.0.11", {"start": v(64.43, 72.59) * mm, "end": v(69.93, 75.76) * mm});
            skLineSegment(sketch, "E54.2.0.12", {"start": v(9.42, 40.83) * mm, "end": v(14.92, 44) * mm});
            skLineSegment(sketch, "E54.2.0.13", {"start": v(91.93, 88.46) * mm, "end": v(97.45, 91.65) * mm});
            skLineSegment(sketch, "E54.3.0.0", {"start": v(40.1, 19.44) * mm, "end": v(45.62, 22.63) * mm});
            skLineSegment(sketch, "E54.3.0.1", {"start": v(12.6, 3.57) * mm, "end": v(18.1, 6.74) * mm});
            skLineSegment(sketch, "E54.3.0.2", {"start": v(36.93, 24.94) * mm, "end": v(42.44, 28.13) * mm});
            skLineSegment(sketch, "E54.3.0.3", {"start": v(122.62, 67.1) * mm, "end": v(128.12, 70.27) * mm});
            skLineSegment(sketch, "E54.3.0.4", {"start": v(150.12, 82.97) * mm, "end": v(155.64, 86.15) * mm});
            skLineSegment(sketch, "E54.3.0.5", {"start": v(95.11, 51.2) * mm, "end": v(100.63, 54.4) * mm});
            skLineSegment(sketch, "E54.3.0.6", {"start": v(-14.91, -12.32) * mm, "end": v(-9.4, -9.13) * mm});
            skLineSegment(sketch, "E54.3.0.7", {"start": v(9.43, 9.07) * mm, "end": v(14.93, 12.24) * mm});
            skLineSegment(sketch, "E54.3.0.8", {"start": v(67.61, 35.33) * mm, "end": v(73.11, 38.5) * mm});
            skLineSegment(sketch, "E54.3.0.9", {"start": v(-18.09, -6.82) * mm, "end": v(-12.57, -3.63) * mm});
            skLineSegment(sketch, "E54.3.0.10", {"start": v(91.94, 56.7) * mm, "end": v(97.45, 59.89) * mm});
            skLineSegment(sketch, "E54.3.0.11", {"start": v(119.45, 72.59) * mm, "end": v(124.95, 75.76) * mm});
            skLineSegment(sketch, "E54.3.0.12", {"start": v(64.44, 40.83) * mm, "end": v(69.94, 44) * mm});
            skLineSegment(sketch, "E54.3.0.13", {"start": v(146.95, 88.46) * mm, "end": v(152.46, 91.65) * mm});
            skLineSegment(sketch, "E54.4.0.0", {"start": v(95.12, 19.44) * mm, "end": v(100.63, 22.63) * mm});
            skLineSegment(sketch, "E54.4.0.1", {"start": v(67.62, 3.57) * mm, "end": v(73.12, 6.74) * mm});
            skLineSegment(sketch, "E54.4.0.2", {"start": v(91.94, 24.94) * mm, "end": v(97.46, 28.13) * mm});
            skLineSegment(sketch, "E54.4.0.3", {"start": v(177.64, 67.1) * mm, "end": v(183.14, 70.27) * mm});
            skLineSegment(sketch, "E54.4.0.4", {"start": v(205.14, 82.97) * mm, "end": v(210.65, 86.15) * mm});
            skLineSegment(sketch, "E54.4.0.5", {"start": v(150.13, 51.2) * mm, "end": v(155.64, 54.4) * mm});
            skLineSegment(sketch, "E54.4.0.6", {"start": v(40.1, -12.32) * mm, "end": v(45.62, -9.13) * mm});
            skLineSegment(sketch, "E54.4.0.7", {"start": v(64.45, 9.07) * mm, "end": v(69.94, 12.24) * mm});
            skLineSegment(sketch, "E54.4.0.8", {"start": v(122.63, 35.33) * mm, "end": v(128.13, 38.5) * mm});
            skLineSegment(sketch, "E54.4.0.9", {"start": v(36.93, -6.82) * mm, "end": v(42.45, -3.63) * mm});
            skLineSegment(sketch, "E54.4.0.10", {"start": v(146.95, 56.7) * mm, "end": v(152.47, 59.89) * mm});
            skLineSegment(sketch, "E54.4.0.11", {"start": v(174.47, 72.59) * mm, "end": v(179.97, 75.76) * mm});
            skLineSegment(sketch, "E54.4.0.12", {"start": v(119.46, 40.83) * mm, "end": v(124.95, 44) * mm});
            skLineSegment(sketch, "E54.4.0.13", {"start": v(201.96, 88.46) * mm, "end": v(207.48, 91.65) * mm});
            skLineSegment(sketch, "E54.direction1", {"start": v(-183.13, -6.82) * mm, "end": v(-128.12, -6.82) * mm, "construction": true});
            skLineSegment(sketch, "E55.1.0.0", {"start": v(201.96, 6.79) * mm, "end": v(207.48, 3.6) * mm});
            skLineSegment(sketch, "E55.1.0.1", {"start": v(91.94, 70.3) * mm, "end": v(97.46, 67.12) * mm});
            skLineSegment(sketch, "E55.1.0.2", {"start": v(183.14, 24.98) * mm, "end": v(177.64, 28.16) * mm});
            skLineSegment(sketch, "E55.1.0.3", {"start": v(100.63, 72.62) * mm, "end": v(95.12, 75.8) * mm});
            skLineSegment(sketch, "E55.1.0.4", {"start": v(146.95, 38.55) * mm, "end": v(152.47, 35.36) * mm});
            skLineSegment(sketch, "E55.1.0.5", {"start": v(128.13, 56.75) * mm, "end": v(122.63, 59.92) * mm});
            skLineSegment(sketch, "E55.1.0.6", {"start": v(155.64, 40.86) * mm, "end": v(150.13, 44.05) * mm});
            skLineSegment(sketch, "E55.1.0.7", {"start": v(73.12, 88.5) * mm, "end": v(67.62, 91.68) * mm});
            skLineSegment(sketch, "E55.1.0.8", {"start": v(119.46, 54.42) * mm, "end": v(124.95, 51.25) * mm});
            skLineSegment(sketch, "E55.1.0.9", {"start": v(210.65, 9.1) * mm, "end": v(205.14, 12.28) * mm});
            skLineSegment(sketch, "E55.1.0.10", {"start": v(174.47, 22.66) * mm, "end": v(179.97, 19.49) * mm});
            skLineSegment(sketch, "E55.1.0.11", {"start": v(64.45, 86.18) * mm, "end": v(69.94, 83) * mm});
            skLineSegment(sketch, "E55.direction1", {"start": v(150.12, 12.28) * mm, "end": v(205.14, 12.28) * mm, "construction": true});
            skLineSegment(sketch, "E56.1.0.0", {"start": v(119.46, 86.18) * mm, "end": v(124.96, 83) * mm});
            skLineSegment(sketch, "E56.1.0.1", {"start": v(174.47, 54.42) * mm, "end": v(179.97, 51.25) * mm});
            skLineSegment(sketch, "E56.1.0.2", {"start": v(146.96, 70.3) * mm, "end": v(152.48, 67.12) * mm});
            skLineSegment(sketch, "E56.1.0.3", {"start": v(128.14, 88.5) * mm, "end": v(122.64, 91.68) * mm});
            skLineSegment(sketch, "E56.1.0.4", {"start": v(210.66, 40.86) * mm, "end": v(205.14, 44.05) * mm});
            skLineSegment(sketch, "E56.1.0.5", {"start": v(183.15, 56.75) * mm, "end": v(177.65, 59.92) * mm});
            skLineSegment(sketch, "E56.1.0.6", {"start": v(201.97, 38.55) * mm, "end": v(207.49, 35.36) * mm});
            skLineSegment(sketch, "E56.1.0.7", {"start": v(155.65, 72.62) * mm, "end": v(150.13, 75.8) * mm});
            skLineSegment(sketch, "E56.direction1", {"start": v(155.64, 40.86) * mm, "end": v(210.66, 40.86) * mm, "construction": true});
            skLineSegment(sketch, "E57.1.0.0", {"start": v(210.67, 72.62) * mm, "end": v(205.15, 75.8) * mm});
            skLineSegment(sketch, "E57.1.0.1", {"start": v(183.15, 88.5) * mm, "end": v(177.65, 91.68) * mm});
            skLineSegment(sketch, "E57.1.0.2", {"start": v(201.97, 70.3) * mm, "end": v(207.5, 67.12) * mm});
            skLineSegment(sketch, "E57.1.0.3", {"start": v(174.48, 86.18) * mm, "end": v(179.98, 83) * mm});
            skLineSegment(sketch, "E57.direction1", {"start": v(122.64, 91.68) * mm, "end": v(177.65, 91.68) * mm, "construction": true});
            skLineSegment(sketch, "E58.1.0.0", {"start": v(205.14, 51.2) * mm, "end": v(210.66, 54.4) * mm});
            skLineSegment(sketch, "E58.1.0.1", {"start": v(201.97, 56.7) * mm, "end": v(207.49, 59.89) * mm});
            skLineSegment(sketch, "E58.1.0.2", {"start": v(91.95, -6.82) * mm, "end": v(97.46, -3.63) * mm});
            skLineSegment(sketch, "E58.1.0.3", {"start": v(146.96, 24.94) * mm, "end": v(152.48, 28.13) * mm});
            skLineSegment(sketch, "E58.1.0.4", {"start": v(177.65, 35.33) * mm, "end": v(183.15, 38.5) * mm});
            skLineSegment(sketch, "E58.1.0.5", {"start": v(122.64, 3.57) * mm, "end": v(128.14, 6.74) * mm});
            skLineSegment(sketch, "E58.1.0.6", {"start": v(119.46, 9.07) * mm, "end": v(124.96, 12.24) * mm});
            skLineSegment(sketch, "E58.1.0.7", {"start": v(174.47, 40.83) * mm, "end": v(179.97, 44) * mm});
            skLineSegment(sketch, "E58.1.0.8", {"start": v(95.12, -12.32) * mm, "end": v(100.64, -9.13) * mm});
            skLineSegment(sketch, "E58.1.0.9", {"start": v(150.13, 19.44) * mm, "end": v(155.65, 22.63) * mm});
            skLineSegment(sketch, "E58.direction1", {"start": v(36.93, -6.82) * mm, "end": v(91.95, -6.82) * mm, "construction": true});
            skLineSegment(sketch, "E59.1.0.0", {"start": v(146.96, -6.82) * mm, "end": v(152.48, -3.63) * mm});
            skLineSegment(sketch, "E59.1.0.1", {"start": v(205.15, 19.44) * mm, "end": v(210.67, 22.63) * mm});
            skLineSegment(sketch, "E59.1.0.2", {"start": v(177.65, 3.57) * mm, "end": v(183.15, 6.74) * mm});
            skLineSegment(sketch, "E59.1.0.3", {"start": v(201.97, 24.94) * mm, "end": v(207.5, 28.13) * mm});
            skLineSegment(sketch, "E59.1.0.4", {"start": v(150.14, -12.32) * mm, "end": v(155.66, -9.13) * mm});
            skLineSegment(sketch, "E59.1.0.5", {"start": v(174.48, 9.07) * mm, "end": v(179.98, 12.24) * mm});
            skLineSegment(sketch, "E59.direction1", {"start": v(91.95, -6.82) * mm, "end": v(146.96, -6.82) * mm, "construction": true});
            skLineSegment(sketch, "E60.1.0.0", {"start": v(205.16, -12.32) * mm, "end": v(210.67, -9.13) * mm});
            skLineSegment(sketch, "E60.1.0.1", {"start": v(201.98, -6.82) * mm, "end": v(207.5, -3.63) * mm});
            skLineSegment(sketch, "E60.direction1", {"start": v(150.14, -12.32) * mm, "end": v(205.16, -12.32) * mm, "construction": true});
            skLineSegment(sketch, "E61.1.0.0", {"start": v(-179.97, 19.44) * mm, "end": v(-174.45, 22.63) * mm});
            skLineSegment(sketch, "E61.1.0.1", {"start": v(-207.46, 3.57) * mm, "end": v(-201.96, 6.74) * mm});
            skLineSegment(sketch, "E61.1.0.2", {"start": v(-183.14, 24.94) * mm, "end": v(-177.62, 28.13) * mm});
            skLineSegment(sketch, "E61.1.0.3", {"start": v(-97.44, 67.1) * mm, "end": v(-91.94, 70.27) * mm});
            skLineSegment(sketch, "E61.1.0.4", {"start": v(-69.94, 82.97) * mm, "end": v(-64.43, 86.15) * mm});
            skLineSegment(sketch, "E61.1.0.5", {"start": v(-124.95, 51.2) * mm, "end": v(-119.44, 54.4) * mm});
            skLineSegment(sketch, "E61.1.0.6", {"start": v(-210.64, 9.07) * mm, "end": v(-205.14, 12.24) * mm});
            skLineSegment(sketch, "E61.1.0.7", {"start": v(-152.45, 35.33) * mm, "end": v(-146.95, 38.5) * mm});
            skLineSegment(sketch, "E61.1.0.8", {"start": v(-128.13, 56.7) * mm, "end": v(-122.61, 59.89) * mm});
            skLineSegment(sketch, "E61.1.0.9", {"start": v(-100.62, 72.59) * mm, "end": v(-95.12, 75.76) * mm});
            skLineSegment(sketch, "E61.1.0.10", {"start": v(-155.63, 40.83) * mm, "end": v(-150.13, 44) * mm});
            skLineSegment(sketch, "E61.1.0.11", {"start": v(-73.12, 88.46) * mm, "end": v(-67.6, 91.65) * mm});
            skLineSegment(sketch, "E61.direction1", {"start": v(-155.62, 9.07) * mm, "end": v(-210.64, 9.07) * mm, "construction": true});
            skLineSegment(sketch, "E62.1.0.0", {"start": v(-152.46, 67.1) * mm, "end": v(-146.96, 70.27) * mm});
            skLineSegment(sketch, "E62.1.0.1", {"start": v(-155.63, 72.59) * mm, "end": v(-150.13, 75.76) * mm});
            skLineSegment(sketch, "E62.1.0.2", {"start": v(-128.14, 88.46) * mm, "end": v(-122.62, 91.65) * mm});
            skLineSegment(sketch, "E62.1.0.3", {"start": v(-183.15, 56.7) * mm, "end": v(-177.63, 59.89) * mm});
            skLineSegment(sketch, "E62.1.0.4", {"start": v(-207.47, 35.33) * mm, "end": v(-201.97, 38.5) * mm});
            skLineSegment(sketch, "E62.1.0.5", {"start": v(-210.64, 40.83) * mm, "end": v(-205.14, 44) * mm});
            skLineSegment(sketch, "E62.1.0.6", {"start": v(-179.97, 51.2) * mm, "end": v(-174.45, 54.4) * mm});
            skLineSegment(sketch, "E62.1.0.7", {"start": v(-124.96, 82.97) * mm, "end": v(-119.44, 86.15) * mm});
            skLineSegment(sketch, "E62.direction1", {"start": v(-155.63, 40.83) * mm, "end": v(-210.64, 40.83) * mm, "construction": true});
            skLineSegment(sketch, "E63.1.0.0", {"start": v(-183.15, 88.46) * mm, "end": v(-177.64, 91.65) * mm});
            skLineSegment(sketch, "E63.1.0.1", {"start": v(-207.47, 67.1) * mm, "end": v(-201.97, 70.27) * mm});
            skLineSegment(sketch, "E63.1.0.2", {"start": v(-179.98, 82.97) * mm, "end": v(-174.46, 86.15) * mm});
            skLineSegment(sketch, "E63.1.0.3", {"start": v(-210.65, 72.59) * mm, "end": v(-205.15, 75.76) * mm});
            skLineSegment(sketch, "E63.direction1", {"start": v(-155.63, 72.59) * mm, "end": v(-210.65, 72.59) * mm, "construction": true});
            skLineSegment(sketch, "E64.1.0.0", {"start": v(-91.95, -6.78) * mm, "end": v(-97.45, -3.6) * mm});
            skLineSegment(sketch, "E64.1.0.1", {"start": v(-174.45, 40.86) * mm, "end": v(-179.97, 44.05) * mm});
            skLineSegment(sketch, "E64.1.0.2", {"start": v(-155.63, 22.66) * mm, "end": v(-150.13, 19.49) * mm});
            skLineSegment(sketch, "E64.1.0.3", {"start": v(-201.97, 56.75) * mm, "end": v(-207.47, 59.92) * mm});
            skLineSegment(sketch, "E64.1.0.4", {"start": v(-210.64, 54.42) * mm, "end": v(-205.14, 51.25) * mm});
            skLineSegment(sketch, "E64.1.0.5", {"start": v(-146.96, 24.98) * mm, "end": v(-152.46, 28.16) * mm});
            skLineSegment(sketch, "E64.1.0.6", {"start": v(-183.15, 38.55) * mm, "end": v(-177.63, 35.36) * mm});
            skLineSegment(sketch, "E64.1.0.7", {"start": v(-119.44, 9.1) * mm, "end": v(-124.96, 12.28) * mm});
            skLineSegment(sketch, "E64.1.0.8", {"start": v(-128.14, 6.79) * mm, "end": v(-122.62, 3.6) * mm});
            skLineSegment(sketch, "E64.1.0.9", {"start": v(-100.62, -9.1) * mm, "end": v(-95.12, -12.27) * mm});
            skLineSegment(sketch, "E64.direction1", {"start": v(-155.63, 54.42) * mm, "end": v(-210.64, 54.42) * mm, "construction": true});
            skLineSegment(sketch, "E65.1.0.0", {"start": v(-155.64, -9.1) * mm, "end": v(-150.14, -12.27) * mm});
            skLineSegment(sketch, "E65.1.0.1", {"start": v(-146.96, -6.78) * mm, "end": v(-152.46, -3.6) * mm});
            skLineSegment(sketch, "E65.1.0.2", {"start": v(-210.65, 22.66) * mm, "end": v(-205.15, 19.49) * mm});
            skLineSegment(sketch, "E65.1.0.3", {"start": v(-174.46, 9.1) * mm, "end": v(-179.98, 12.28) * mm});
            skLineSegment(sketch, "E65.1.0.4", {"start": v(-183.15, 6.79) * mm, "end": v(-177.64, 3.6) * mm});
            skLineSegment(sketch, "E65.1.0.5", {"start": v(-201.97, 24.98) * mm, "end": v(-207.47, 28.16) * mm});
            skLineSegment(sketch, "E65.direction1", {"start": v(-155.63, 22.66) * mm, "end": v(-210.65, 22.66) * mm, "construction": true});
            skLineSegment(sketch, "E66.1.0.0", {"start": v(-201.98, -6.78) * mm, "end": v(-207.48, -3.6) * mm});
            skLineSegment(sketch, "E66.1.0.1", {"start": v(-210.65, -9.1) * mm, "end": v(-205.16, -12.27) * mm});
            skLineSegment(sketch, "E66.direction1", {"start": v(-155.64, -9.1) * mm, "end": v(-210.65, -9.1) * mm, "construction": true});
            skSolve(sketch);
        }
        {
            var Q0;
            Q0=makeQuery(id+"F0.imprint","IMPRINT",FACE,{"disambiguationData":[TD([[makeQuery(id+"F0.imprint","IMPRINT",EDGE,{"derivedFrom":sQuery(id+"F0.wireOp",EDGE,"E9.4.0.6")}),-1.0]])]});
            var Q1;
            {var subQ0=sQuery(id+"F0.wireOp",EDGE,"E54.3.0.6");Q1=makeQuery(id+"F0.imprint","IMPRINT",FACE,{"disambiguationData":[TD([[makeQuery(id+"F0.imprint","IMPRINT",EDGE,{"derivedFrom":subQ0}),1.0]])]});}
            var Q2;
            {var subQ0=sQuery(id+"F0.wireOp",EDGE,"E39.1.0.10");Q2=makeQuery(id+"F0.imprint","IMPRINT",FACE,{"disambiguationData":[TD([[makeQuery(id+"F0.imprint","IMPRINT",EDGE,{"derivedFrom":subQ0}),1.0]])]});}
            var Q3;
            Q3=makeQuery(id+"F0.imprint","IMPRINT",FACE,{"disambiguationData":[TD([[makeQuery(id+"F0.imprint","IMPRINT",EDGE,{"derivedFrom":sQuery(id+"F0.wireOp",EDGE,"E9.3.0.0")}),-1.0]])]});
            var Q4;
            Q4=makeQuery(id+"F0.imprint","IMPRINT",FACE,{"disambiguationData":[TD([[makeQuery(id+"F0.imprint","IMPRINT",EDGE,{"derivedFrom":sQuery(id+"F0.wireOp",EDGE,"E9.4.0.0")}),-1.0]])]});
            var Q5;
            {var subQ0=sQuery(id+"F0.wireOp",EDGE,"E18.trimOffspring");Q5=makeQuery(id+"F0.imprint","IMPRINT",FACE,{"disambiguationData":[TD([[makeQuery(id+"F0.imprint","IMPRINT",EDGE,{"derivedFrom":subQ0}),1.0]])]});}
            var Q6;
            {var subQ0=sQuery(id+"F0.wireOp",EDGE,"E54.4.0.6");Q6=makeQuery(id+"F0.imprint","IMPRINT",FACE,{"disambiguationData":[TD([[makeQuery(id+"F0.imprint","IMPRINT",EDGE,{"derivedFrom":subQ0}),1.0]])]});}
            var Q7;
            Q7=makeQuery(id+"F0.imprint","IMPRINT",FACE,{"disambiguationData":[TD([[makeQuery(id+"F0.imprint","IMPRINT",EDGE,{"derivedFrom":sQuery(id+"F0.wireOp",EDGE,"E9.5.0.6")}),-1.0]])]});
            var Q8;
            Q8=makeQuery(id+"F0.imprint","IMPRINT",FACE,{"disambiguationData":[TD([[makeQuery(id+"F0.imprint","IMPRINT",EDGE,{"derivedFrom":sQuery(id+"F0.wireOp",EDGE,"E9.3.0.6")}),-1.0]])]});
            var Q9;
            {var subQ0=sQuery(id+"F0.wireOp",EDGE,"E54.2.0.6");Q9=makeQuery(id+"F0.imprint","IMPRINT",FACE,{"disambiguationData":[TD([[makeQuery(id+"F0.imprint","IMPRINT",EDGE,{"derivedFrom":subQ0}),1.0]])]});}
            var Q10;
            {var subQ0=sQuery(id+"F0.wireOp",EDGE,"E39.2.0.10");Q10=makeQuery(id+"F0.imprint","IMPRINT",FACE,{"disambiguationData":[TD([[makeQuery(id+"F0.imprint","IMPRINT",EDGE,{"derivedFrom":subQ0}),1.0]])]});}
            var Q11;
            Q11=makeQuery(id+"F0.imprint","IMPRINT",FACE,{"disambiguationData":[TD([[makeQuery(id+"F0.imprint","IMPRINT",EDGE,{"derivedFrom":sQuery(id+"F0.wireOp",EDGE,"E9.5.0.0")}),-1.0]])]});
            var Q12;
            Q12=makeQuery(id+"F0.imprint","IMPRINT",FACE,{"disambiguationData":[TD([[makeQuery(id+"F0.imprint","IMPRINT",EDGE,{"derivedFrom":sQuery(id+"F0.wireOp",EDGE,"E9.2.0.0")}),-1.0]])]});
            var Q13;
            {var subQ0=sQuery(id+"F0.wireOp",EDGE,"E64.1.0.0");Q13=makeQuery(id+"F0.imprint","IMPRINT",FACE,{"disambiguationData":[TD([[makeQuery(id+"F0.imprint","IMPRINT",EDGE,{"derivedFrom":subQ0}),1.0]])]});}
            var Q14;
            {var subQ0=sQuery(id+"F0.wireOp",EDGE,"E58.1.0.2");Q14=makeQuery(id+"F0.imprint","IMPRINT",FACE,{"disambiguationData":[TD([[makeQuery(id+"F0.imprint","IMPRINT",EDGE,{"derivedFrom":subQ0}),-1.0]])]});}
            var Q15;
            Q15=makeQuery(id+"F0.imprint","IMPRINT",FACE,{"disambiguationData":[TD([[makeQuery(id+"F0.imprint","IMPRINT",EDGE,{"derivedFrom":sQuery(id+"F0.wireOp",EDGE,"E9.2.0.6")}),-1.0]])]});
            var Q16;
            Q16=makeQuery(id+"F0.imprint","IMPRINT",FACE,{"disambiguationData":[TD([[makeQuery(id+"F0.imprint","IMPRINT",EDGE,{"derivedFrom":sQuery(id+"F0.wireOp",EDGE,"E9.6.0.6")}),-1.0]])]});
            var Q17;
            {var subQ0=sQuery(id+"F0.wireOp",EDGE,"E54.1.0.1");Q17=makeQuery(id+"F0.imprint","IMPRINT",FACE,{"disambiguationData":[TD([[makeQuery(id+"F0.imprint","IMPRINT",EDGE,{"derivedFrom":subQ0}),1.0]])]});}
            var Q18;
            Q18=makeQuery(id+"F0.imprint","IMPRINT",FACE,{"disambiguationData":[TD([[makeQuery(id+"F0.imprint","IMPRINT",EDGE,{"derivedFrom":sQuery(id+"F0.wireOp",EDGE,"E10.0.1.44")}),-1.0]])]});
            var Q19;
            {var subQ0=sQuery(id+"F0.wireOp",EDGE,"E28.trimOffspring");Q19=makeQuery(id+"F0.imprint","IMPRINT",FACE,{"disambiguationData":[TD([[makeQuery(id+"F0.imprint","IMPRINT",EDGE,{"derivedFrom":subQ0}),1.0]])]});}
            var Q20;
            {var subQ0=sQuery(id+"F0.wireOp",EDGE,"E54.2.0.1");Q20=makeQuery(id+"F0.imprint","IMPRINT",FACE,{"disambiguationData":[TD([[makeQuery(id+"F0.imprint","IMPRINT",EDGE,{"derivedFrom":subQ0}),1.0]])]});}
            var Q21;
            Q21=makeQuery(id+"F0.imprint","IMPRINT",FACE,{"disambiguationData":[TD([[makeQuery(id+"F0.imprint","IMPRINT",EDGE,{"derivedFrom":sQuery(id+"F0.wireOp",EDGE,"E10.0.1.96")}),-1.0]])]});
            var Q22;
            {var subQ0=sQuery(id+"F0.wireOp",EDGE,"E39.1.0.1");Q22=makeQuery(id+"F0.imprint","IMPRINT",FACE,{"disambiguationData":[TD([[makeQuery(id+"F0.imprint","IMPRINT",EDGE,{"derivedFrom":subQ0}),1.0]])]});}
            var Q23;
            {var subQ0=sQuery(id+"F0.wireOp",EDGE,"E54.3.0.1");Q23=makeQuery(id+"F0.imprint","IMPRINT",FACE,{"disambiguationData":[TD([[makeQuery(id+"F0.imprint","IMPRINT",EDGE,{"derivedFrom":subQ0}),1.0]])]});}
            var Q24;
            Q24=makeQuery(id+"F0.imprint","IMPRINT",FACE,{"disambiguationData":[TD([[makeQuery(id+"F0.imprint","IMPRINT",EDGE,{"derivedFrom":sQuery(id+"F0.wireOp",EDGE,"E10.0.1.27")}),-1.0]])]});
            var Q25;
            {var subQ0=sQuery(id+"F0.wireOp",EDGE,"E39.2.0.1");Q25=makeQuery(id+"F0.imprint","IMPRINT",FACE,{"disambiguationData":[TD([[makeQuery(id+"F0.imprint","IMPRINT",EDGE,{"derivedFrom":subQ0}),1.0]])]});}
            var Q26;
            {var subQ0=sQuery(id+"F0.wireOp",EDGE,"E54.4.0.1");Q26=makeQuery(id+"F0.imprint","IMPRINT",FACE,{"disambiguationData":[TD([[makeQuery(id+"F0.imprint","IMPRINT",EDGE,{"derivedFrom":subQ0}),1.0]])]});}
            var Q27;
            Q27=makeQuery(id+"F0.imprint","IMPRINT",FACE,{"disambiguationData":[TD([[makeQuery(id+"F0.imprint","IMPRINT",EDGE,{"derivedFrom":sQuery(id+"F0.wireOp",EDGE,"E10.0.1.76")}),-1.0]])]});
            var Q28;
            {var subQ0=sQuery(id+"F0.wireOp",EDGE,"E39.3.0.1");Q28=makeQuery(id+"F0.imprint","IMPRINT",FACE,{"disambiguationData":[TD([[makeQuery(id+"F0.imprint","IMPRINT",EDGE,{"derivedFrom":subQ0}),1.0]])]});}
            var Q29;
            {var subQ0=sQuery(id+"F0.wireOp",EDGE,"E54.1.0.6");Q29=makeQuery(id+"F0.imprint","IMPRINT",FACE,{"disambiguationData":[TD([[makeQuery(id+"F0.imprint","IMPRINT",EDGE,{"derivedFrom":subQ0}),1.0]])]});}
            var Q30;
            {var subQ0=sQuery(id+"F0.wireOp",EDGE,"E39.3.0.10");Q30=makeQuery(id+"F0.imprint","IMPRINT",FACE,{"disambiguationData":[TD([[makeQuery(id+"F0.imprint","IMPRINT",EDGE,{"derivedFrom":subQ0}),1.0]])]});}
            var Q31;
            {var subQ0=sQuery(id+"F0.wireOp",EDGE,"E58.1.0.5");Q31=makeQuery(id+"F0.imprint","IMPRINT",FACE,{"disambiguationData":[TD([[makeQuery(id+"F0.imprint","IMPRINT",EDGE,{"derivedFrom":subQ0}),1.0]])]});}
            var Q32;
            {var subQ0=sQuery(id+"F0.wireOp",EDGE,"E31.6.0.4");Q32=makeQuery(id+"F0.imprint","IMPRINT",FACE,{"disambiguationData":[TD([[makeQuery(id+"F0.imprint","IMPRINT",EDGE,{"derivedFrom":subQ0}),-1.0]])]});}
            var Q33;
            {var subQ0=sQuery(id+"F0.wireOp",EDGE,"E54.4.0.0");Q33=makeQuery(id+"F0.imprint","IMPRINT",FACE,{"disambiguationData":[TD([[makeQuery(id+"F0.imprint","IMPRINT",EDGE,{"derivedFrom":subQ0}),1.0]])]});}
            var Q34;
            {var subQ0=sQuery(id+"F0.wireOp",EDGE,"E38.5.0.0");Q34=makeQuery(id+"F0.imprint","IMPRINT",FACE,{"disambiguationData":[TD([[makeQuery(id+"F0.imprint","IMPRINT",EDGE,{"derivedFrom":subQ0}),-1.0]])]});}
            var Q35;
            {var subQ0=sQuery(id+"F0.wireOp",EDGE,"E39.3.0.3");Q35=makeQuery(id+"F0.imprint","IMPRINT",FACE,{"disambiguationData":[TD([[makeQuery(id+"F0.imprint","IMPRINT",EDGE,{"derivedFrom":subQ0}),1.0]])]});}
            var Q36;
            {var subQ0=sQuery(id+"F0.wireOp",EDGE,"E31.5.0.4");Q36=makeQuery(id+"F0.imprint","IMPRINT",FACE,{"disambiguationData":[TD([[makeQuery(id+"F0.imprint","IMPRINT",EDGE,{"derivedFrom":subQ0}),-1.0]])]});}
            var Q37;
            {var subQ0=sQuery(id+"F0.wireOp",EDGE,"E54.3.0.0");Q37=makeQuery(id+"F0.imprint","IMPRINT",FACE,{"disambiguationData":[TD([[makeQuery(id+"F0.imprint","IMPRINT",EDGE,{"derivedFrom":subQ0}),1.0]])]});}
            var Q38;
            {var subQ0=sQuery(id+"F0.wireOp",EDGE,"E38.4.0.0");Q38=makeQuery(id+"F0.imprint","IMPRINT",FACE,{"disambiguationData":[TD([[makeQuery(id+"F0.imprint","IMPRINT",EDGE,{"derivedFrom":subQ0}),-1.0]])]});}
            var Q39;
            {var subQ0=sQuery(id+"F0.wireOp",EDGE,"E39.2.0.3");Q39=makeQuery(id+"F0.imprint","IMPRINT",FACE,{"disambiguationData":[TD([[makeQuery(id+"F0.imprint","IMPRINT",EDGE,{"derivedFrom":subQ0}),1.0]])]});}
            var Q40;
            {var subQ0=sQuery(id+"F0.wireOp",EDGE,"E31.4.0.4");Q40=makeQuery(id+"F0.imprint","IMPRINT",FACE,{"disambiguationData":[TD([[makeQuery(id+"F0.imprint","IMPRINT",EDGE,{"derivedFrom":subQ0}),-1.0]])]});}
            var Q41;
            {var subQ0=sQuery(id+"F0.wireOp",EDGE,"E54.2.0.0");Q41=makeQuery(id+"F0.imprint","IMPRINT",FACE,{"disambiguationData":[TD([[makeQuery(id+"F0.imprint","IMPRINT",EDGE,{"derivedFrom":subQ0}),1.0]])]});}
            var Q42;
            {var subQ0=sQuery(id+"F0.wireOp",EDGE,"E38.3.0.0");Q42=makeQuery(id+"F0.imprint","IMPRINT",FACE,{"disambiguationData":[TD([[makeQuery(id+"F0.imprint","IMPRINT",EDGE,{"derivedFrom":subQ0}),-1.0]])]});}
            var Q43;
            {var subQ0=sQuery(id+"F0.wireOp",EDGE,"E39.1.0.3");Q43=makeQuery(id+"F0.imprint","IMPRINT",FACE,{"disambiguationData":[TD([[makeQuery(id+"F0.imprint","IMPRINT",EDGE,{"derivedFrom":subQ0}),1.0]])]});}
            var Q44;
            {var subQ0=sQuery(id+"F0.wireOp",EDGE,"E31.3.0.4");Q44=makeQuery(id+"F0.imprint","IMPRINT",FACE,{"disambiguationData":[TD([[makeQuery(id+"F0.imprint","IMPRINT",EDGE,{"derivedFrom":subQ0}),-1.0]])]});}
            var Q45;
            {var subQ0=sQuery(id+"F0.wireOp",EDGE,"E54.1.0.0");Q45=makeQuery(id+"F0.imprint","IMPRINT",FACE,{"disambiguationData":[TD([[makeQuery(id+"F0.imprint","IMPRINT",EDGE,{"derivedFrom":subQ0}),1.0]])]});}
            var Q46;
            {var subQ0=sQuery(id+"F0.wireOp",EDGE,"E38.2.0.0");Q46=makeQuery(id+"F0.imprint","IMPRINT",FACE,{"disambiguationData":[TD([[makeQuery(id+"F0.imprint","IMPRINT",EDGE,{"derivedFrom":subQ0}),-1.0]])]});}
            var Q47;
            {var subQ0=sQuery(id+"F0.wireOp",EDGE,"E26.trimOffspring");Q47=makeQuery(id+"F0.imprint","IMPRINT",FACE,{"disambiguationData":[TD([[makeQuery(id+"F0.imprint","IMPRINT",EDGE,{"derivedFrom":subQ0}),1.0]])]});}
            var Q48;
            {var subQ0=sQuery(id+"F0.wireOp",EDGE,"E31.2.0.4");Q48=makeQuery(id+"F0.imprint","IMPRINT",FACE,{"disambiguationData":[TD([[makeQuery(id+"F0.imprint","IMPRINT",EDGE,{"derivedFrom":subQ0}),-1.0]])]});}
            var Q49;
            {var subQ0=sQuery(id+"F0.wireOp",EDGE,"E64.1.0.7");Q49=makeQuery(id+"F0.imprint","IMPRINT",FACE,{"disambiguationData":[TD([[makeQuery(id+"F0.imprint","IMPRINT",EDGE,{"derivedFrom":subQ0}),1.0]])]});}
            var Q50;
            {var subQ0=sQuery(id+"F0.wireOp",EDGE,"E38.2.0.2");Q50=makeQuery(id+"F0.imprint","IMPRINT",FACE,{"disambiguationData":[TD([[makeQuery(id+"F0.imprint","IMPRINT",EDGE,{"derivedFrom":subQ0}),1.0]])]});}
            var Q51;
            {var subQ0=sQuery(id+"F0.wireOp",EDGE,"E38.3.0.2");Q51=makeQuery(id+"F0.imprint","IMPRINT",FACE,{"disambiguationData":[TD([[makeQuery(id+"F0.imprint","IMPRINT",EDGE,{"derivedFrom":subQ0}),1.0]])]});}
            var Q52;
            {var subQ0=sQuery(id+"F0.wireOp",EDGE,"E38.4.0.2");Q52=makeQuery(id+"F0.imprint","IMPRINT",FACE,{"disambiguationData":[TD([[makeQuery(id+"F0.imprint","IMPRINT",EDGE,{"derivedFrom":subQ0}),1.0]])]});}
            var Q53;
            {var subQ0=sQuery(id+"F0.wireOp",EDGE,"E38.5.0.2");Q53=makeQuery(id+"F0.imprint","IMPRINT",FACE,{"disambiguationData":[TD([[makeQuery(id+"F0.imprint","IMPRINT",EDGE,{"derivedFrom":subQ0}),1.0]])]});}
            extrude(context, id + "F1", {"entities" : qUnion([Q0, Q1, Q2, Q3, Q4, Q5, Q6, Q7, Q8, Q9, Q10, Q11, Q12, Q13, Q14, Q15, Q16, Q17, Q18, Q19, Q20, Q21, Q22, Q23, Q24, Q25, Q26, Q27, Q28, Q29, Q30, Q31, Q32, Q33, Q34, Q35, Q36, Q37, Q38, Q39, Q40, Q41, Q42, Q43, Q44, Q45, Q46, Q47, Q48, Q49, Q50, Q51, Q52, Q53]), "depth" : 104.77 * mm, "offsetDistance" : 25.4 * mm, "hasSecondDirection" : true, "secondDirectionOppositeDirection" : false, "secondDirectionDepth" : 101.6 * mm});
        }
        {
            var Q0;
            Q0=makeQuery(id+"F0.imprint","IMPRINT",FACE,{"disambiguationData":[TD([[makeQuery(id+"F0.imprint","IMPRINT",EDGE,{"derivedFrom":sQuery(id+"F0.wireOp",EDGE,"E9.1.0.0")}),-1.0]])]});
            var Q1;
            Q1=makeQuery(id+"F0.imprint","IMPRINT",FACE,{"disambiguationData":[TD([[makeQuery(id+"F0.imprint","IMPRINT",EDGE,{"derivedFrom":sQuery(id+"F0.wireOp",EDGE,"E9.1.0.6")}),-1.0]])]});
            var Q2;
            {var subQ0=sQuery(id+"F0.wireOp",EDGE,"E65.1.0.0");Q2=makeQuery(id+"F0.imprint","IMPRINT",FACE,{"disambiguationData":[TD([[makeQuery(id+"F0.imprint","IMPRINT",EDGE,{"derivedFrom":subQ0}),1.0]])]});}
            var Q3;
            {var subQ0=sQuery(id+"F0.wireOp",EDGE,"E40");Q3=makeQuery(id+"F0.imprint","IMPRINT",FACE,{"disambiguationData":[TD([[makeQuery(id+"F0.imprint","IMPRINT",EDGE,{"derivedFrom":subQ0}),-1.0]])]});}
            var Q4;
            {var subQ0=sQuery(id+"F0.wireOp",EDGE,"E65.1.0.3");Q4=makeQuery(id+"F0.imprint","IMPRINT",FACE,{"disambiguationData":[TD([[makeQuery(id+"F0.imprint","IMPRINT",EDGE,{"derivedFrom":subQ0}),1.0]])]});}
            var Q5;
            {var subQ0=sQuery(id+"F0.wireOp",EDGE,"E31.1.0.4");Q5=makeQuery(id+"F0.imprint","IMPRINT",FACE,{"disambiguationData":[TD([[makeQuery(id+"F0.imprint","IMPRINT",EDGE,{"derivedFrom":subQ0}),-1.0]])]});}
            var Q6;
            {var subQ0=sQuery(id+"F0.wireOp",EDGE,"E42.trimOffspring");Q6=makeQuery(id+"F0.imprint","IMPRINT",FACE,{"disambiguationData":[TD([[makeQuery(id+"F0.imprint","IMPRINT",EDGE,{"derivedFrom":subQ0}),-1.0]])]});}
            var Q7;
            {var subQ0=sQuery(id+"F0.wireOp",EDGE,"E38.1.0.2");Q7=makeQuery(id+"F0.imprint","IMPRINT",FACE,{"disambiguationData":[TD([[makeQuery(id+"F0.imprint","IMPRINT",EDGE,{"derivedFrom":subQ0}),1.0]])]});}
            var Q8;
            Q8=makeQuery(id+"F0.imprint","IMPRINT",FACE,{"disambiguationData":[TD([[makeQuery(id+"F0.imprint","IMPRINT",EDGE,{"derivedFrom":sQuery(id+"F0.wireOp",EDGE,"E10.0.1.111")}),-1.0]])]});
            var Q9;
            {var subQ0=sQuery(id+"F0.wireOp",EDGE,"E64.1.0.2");Q9=makeQuery(id+"F0.imprint","IMPRINT",FACE,{"disambiguationData":[TD([[makeQuery(id+"F0.imprint","IMPRINT",EDGE,{"derivedFrom":subQ0}),1.0]])]});}
            var Q10;
            {var subQ0=sQuery(id+"F0.wireOp",EDGE,"E38.1.0.0");Q10=makeQuery(id+"F0.imprint","IMPRINT",FACE,{"disambiguationData":[TD([[makeQuery(id+"F0.imprint","IMPRINT",EDGE,{"derivedFrom":subQ0}),-1.0]])]});}
            var Q11;
            {var subQ0=sQuery(id+"F0.wireOp",EDGE,"E44.trimOffspring");Q11=makeQuery(id+"F0.imprint","IMPRINT",FACE,{"disambiguationData":[TD([[makeQuery(id+"F0.imprint","IMPRINT",EDGE,{"derivedFrom":subQ0}),1.0]])]});}
            var Q12;
            Q12=makeQuery(id+"F0.imprint","IMPRINT",FACE,{"disambiguationData":[TD([[makeQuery(id+"F0.imprint","IMPRINT",EDGE,{"derivedFrom":sQuery(id+"F0.wireOp",EDGE,"E10.0.1.104")}),-1.0]])]});
            var Q13;
            {var subQ0=sQuery(id+"F0.wireOp",EDGE,"E24.trimOffspring");Q13=makeQuery(id+"F0.imprint","IMPRINT",FACE,{"disambiguationData":[TD([[makeQuery(id+"F0.imprint","IMPRINT",EDGE,{"derivedFrom":subQ0}),1.0]])]});}
            var Q14;
            {var subQ0=sQuery(id+"F0.wireOp",EDGE,"E31.2.0.2");Q14=makeQuery(id+"F0.imprint","IMPRINT",FACE,{"disambiguationData":[TD([[makeQuery(id+"F0.imprint","IMPRINT",EDGE,{"derivedFrom":subQ0}),-1.0]])]});}
            var Q15;
            {var subQ0=sQuery(id+"F0.wireOp",EDGE,"E46.trimOffspring");Q15=makeQuery(id+"F0.imprint","IMPRINT",FACE,{"disambiguationData":[TD([[makeQuery(id+"F0.imprint","IMPRINT",EDGE,{"derivedFrom":subQ0}),-1.0]])]});}
            var Q16;
            Q16=makeQuery(id+"F0.imprint","IMPRINT",FACE,{"disambiguationData":[TD([[makeQuery(id+"F0.imprint","IMPRINT",EDGE,{"derivedFrom":sQuery(id+"F0.wireOp",EDGE,"E10.0.2.44")}),-1.0]])]});
            var Q17;
            {var subQ0=sQuery(id+"F0.wireOp",EDGE,"E39.1.0.2");Q17=makeQuery(id+"F0.imprint","IMPRINT",FACE,{"disambiguationData":[TD([[makeQuery(id+"F0.imprint","IMPRINT",EDGE,{"derivedFrom":subQ0}),1.0]])]});}
            var Q18;
            {var subQ0=sQuery(id+"F0.wireOp",EDGE,"E38.2.0.1");Q18=makeQuery(id+"F0.imprint","IMPRINT",FACE,{"disambiguationData":[TD([[makeQuery(id+"F0.imprint","IMPRINT",EDGE,{"derivedFrom":subQ0}),1.0]])]});}
            var Q19;
            {var subQ0=sQuery(id+"F0.wireOp",EDGE,"E48.trimOffspring");Q19=makeQuery(id+"F0.imprint","IMPRINT",FACE,{"disambiguationData":[TD([[makeQuery(id+"F0.imprint","IMPRINT",EDGE,{"derivedFrom":subQ0}),1.0]])]});}
            var Q20;
            {var subQ0=sQuery(id+"F0.wireOp",EDGE,"E39.1.0.0");Q20=makeQuery(id+"F0.imprint","IMPRINT",FACE,{"disambiguationData":[TD([[makeQuery(id+"F0.imprint","IMPRINT",EDGE,{"derivedFrom":subQ0}),1.0]])]});}
            var Q21;
            Q21=makeQuery(id+"F0.imprint","IMPRINT",FACE,{"disambiguationData":[TD([[makeQuery(id+"F0.imprint","IMPRINT",EDGE,{"derivedFrom":sQuery(id+"F0.wireOp",EDGE,"E10.0.1.35")}),-1.0]])]});
            var Q22;
            {var subQ0=sQuery(id+"F0.wireOp",EDGE,"E31.3.0.2");Q22=makeQuery(id+"F0.imprint","IMPRINT",FACE,{"disambiguationData":[TD([[makeQuery(id+"F0.imprint","IMPRINT",EDGE,{"derivedFrom":subQ0}),-1.0]])]});}
            var Q23;
            {var subQ0=sQuery(id+"F0.wireOp",EDGE,"E54.1.0.8");Q23=makeQuery(id+"F0.imprint","IMPRINT",FACE,{"disambiguationData":[TD([[makeQuery(id+"F0.imprint","IMPRINT",EDGE,{"derivedFrom":subQ0}),1.0]])]});}
            var Q24;
            Q24=makeQuery(id+"F0.imprint","IMPRINT",FACE,{"disambiguationData":[TD([[makeQuery(id+"F0.imprint","IMPRINT",EDGE,{"derivedFrom":sQuery(id+"F0.wireOp",EDGE,"E10.0.2.96")}),-1.0]])]});
            var Q25;
            {var subQ0=sQuery(id+"F0.wireOp",EDGE,"E39.2.0.2");Q25=makeQuery(id+"F0.imprint","IMPRINT",FACE,{"disambiguationData":[TD([[makeQuery(id+"F0.imprint","IMPRINT",EDGE,{"derivedFrom":subQ0}),1.0]])]});}
            var Q26;
            {var subQ0=sQuery(id+"F0.wireOp",EDGE,"E38.3.0.1");Q26=makeQuery(id+"F0.imprint","IMPRINT",FACE,{"disambiguationData":[TD([[makeQuery(id+"F0.imprint","IMPRINT",EDGE,{"derivedFrom":subQ0}),1.0]])]});}
            var Q27;
            {var subQ0=sQuery(id+"F0.wireOp",EDGE,"E54.1.0.5");Q27=makeQuery(id+"F0.imprint","IMPRINT",FACE,{"disambiguationData":[TD([[makeQuery(id+"F0.imprint","IMPRINT",EDGE,{"derivedFrom":subQ0}),1.0]])]});}
            var Q28;
            {var subQ0=sQuery(id+"F0.wireOp",EDGE,"E39.2.0.0");Q28=makeQuery(id+"F0.imprint","IMPRINT",FACE,{"disambiguationData":[TD([[makeQuery(id+"F0.imprint","IMPRINT",EDGE,{"derivedFrom":subQ0}),1.0]])]});}
            var Q29;
            Q29=makeQuery(id+"F0.imprint","IMPRINT",FACE,{"disambiguationData":[TD([[makeQuery(id+"F0.imprint","IMPRINT",EDGE,{"derivedFrom":sQuery(id+"F0.wireOp",EDGE,"E10.0.1.89")}),-1.0]])]});
            var Q30;
            {var subQ0=sQuery(id+"F0.wireOp",EDGE,"E31.4.0.2");Q30=makeQuery(id+"F0.imprint","IMPRINT",FACE,{"disambiguationData":[TD([[makeQuery(id+"F0.imprint","IMPRINT",EDGE,{"derivedFrom":subQ0}),-1.0]])]});}
            var Q31;
            {var subQ0=sQuery(id+"F0.wireOp",EDGE,"E54.2.0.8");Q31=makeQuery(id+"F0.imprint","IMPRINT",FACE,{"disambiguationData":[TD([[makeQuery(id+"F0.imprint","IMPRINT",EDGE,{"derivedFrom":subQ0}),1.0]])]});}
            var Q32;
            Q32=makeQuery(id+"F0.imprint","IMPRINT",FACE,{"disambiguationData":[TD([[makeQuery(id+"F0.imprint","IMPRINT",EDGE,{"derivedFrom":sQuery(id+"F0.wireOp",EDGE,"E10.0.2.27")}),-1.0]])]});
            var Q33;
            {var subQ0=sQuery(id+"F0.wireOp",EDGE,"E39.3.0.2");Q33=makeQuery(id+"F0.imprint","IMPRINT",FACE,{"disambiguationData":[TD([[makeQuery(id+"F0.imprint","IMPRINT",EDGE,{"derivedFrom":subQ0}),1.0]])]});}
            var Q34;
            {var subQ0=sQuery(id+"F0.wireOp",EDGE,"E38.4.0.1");Q34=makeQuery(id+"F0.imprint","IMPRINT",FACE,{"disambiguationData":[TD([[makeQuery(id+"F0.imprint","IMPRINT",EDGE,{"derivedFrom":subQ0}),1.0]])]});}
            var Q35;
            {var subQ0=sQuery(id+"F0.wireOp",EDGE,"E54.2.0.5");Q35=makeQuery(id+"F0.imprint","IMPRINT",FACE,{"disambiguationData":[TD([[makeQuery(id+"F0.imprint","IMPRINT",EDGE,{"derivedFrom":subQ0}),1.0]])]});}
            var Q36;
            {var subQ0=sQuery(id+"F0.wireOp",EDGE,"E39.3.0.0");Q36=makeQuery(id+"F0.imprint","IMPRINT",FACE,{"disambiguationData":[TD([[makeQuery(id+"F0.imprint","IMPRINT",EDGE,{"derivedFrom":subQ0}),1.0]])]});}
            var Q37;
            Q37=makeQuery(id+"F0.imprint","IMPRINT",FACE,{"disambiguationData":[TD([[makeQuery(id+"F0.imprint","IMPRINT",EDGE,{"derivedFrom":sQuery(id+"F0.wireOp",EDGE,"E10.0.1.19")}),-1.0]])]});
            var Q38;
            {var subQ0=sQuery(id+"F0.wireOp",EDGE,"E31.5.0.2");Q38=makeQuery(id+"F0.imprint","IMPRINT",FACE,{"disambiguationData":[TD([[makeQuery(id+"F0.imprint","IMPRINT",EDGE,{"derivedFrom":subQ0}),-1.0]])]});}
            var Q39;
            {var subQ0=sQuery(id+"F0.wireOp",EDGE,"E54.3.0.8");Q39=makeQuery(id+"F0.imprint","IMPRINT",FACE,{"disambiguationData":[TD([[makeQuery(id+"F0.imprint","IMPRINT",EDGE,{"derivedFrom":subQ0}),1.0]])]});}
            var Q40;
            Q40=makeQuery(id+"F0.imprint","IMPRINT",FACE,{"disambiguationData":[TD([[makeQuery(id+"F0.imprint","IMPRINT",EDGE,{"derivedFrom":sQuery(id+"F0.wireOp",EDGE,"E10.0.2.76")}),-1.0]])]});
            var Q41;
            {var subQ0=sQuery(id+"F0.wireOp",EDGE,"E39.4.0.2");Q41=makeQuery(id+"F0.imprint","IMPRINT",FACE,{"disambiguationData":[TD([[makeQuery(id+"F0.imprint","IMPRINT",EDGE,{"derivedFrom":subQ0}),1.0]])]});}
            var Q42;
            {var subQ0=sQuery(id+"F0.wireOp",EDGE,"E38.5.0.1");Q42=makeQuery(id+"F0.imprint","IMPRINT",FACE,{"disambiguationData":[TD([[makeQuery(id+"F0.imprint","IMPRINT",EDGE,{"derivedFrom":subQ0}),1.0]])]});}
            var Q43;
            {var subQ0=sQuery(id+"F0.wireOp",EDGE,"E54.3.0.5");Q43=makeQuery(id+"F0.imprint","IMPRINT",FACE,{"disambiguationData":[TD([[makeQuery(id+"F0.imprint","IMPRINT",EDGE,{"derivedFrom":subQ0}),1.0]])]});}
            var Q44;
            {var subQ0=sQuery(id+"F0.wireOp",EDGE,"E39.4.0.0");Q44=makeQuery(id+"F0.imprint","IMPRINT",FACE,{"disambiguationData":[TD([[makeQuery(id+"F0.imprint","IMPRINT",EDGE,{"derivedFrom":subQ0}),1.0]])]});}
            var Q45;
            Q45=makeQuery(id+"F0.imprint","IMPRINT",FACE,{"disambiguationData":[TD([[makeQuery(id+"F0.imprint","IMPRINT",EDGE,{"derivedFrom":sQuery(id+"F0.wireOp",EDGE,"E10.0.1.69")}),-1.0]])]});
            var Q46;
            {var subQ0=sQuery(id+"F0.wireOp",EDGE,"E39.4.0.3");Q46=makeQuery(id+"F0.imprint","IMPRINT",FACE,{"disambiguationData":[TD([[makeQuery(id+"F0.imprint","IMPRINT",EDGE,{"derivedFrom":subQ0}),1.0]])]});}
            var Q47;
            {var subQ0=sQuery(id+"F0.wireOp",EDGE,"E31.6.0.2");Q47=makeQuery(id+"F0.imprint","IMPRINT",FACE,{"disambiguationData":[TD([[makeQuery(id+"F0.imprint","IMPRINT",EDGE,{"derivedFrom":subQ0}),-1.0]])]});}
            var Q48;
            {var subQ0=sQuery(id+"F0.wireOp",EDGE,"E54.4.0.8");Q48=makeQuery(id+"F0.imprint","IMPRINT",FACE,{"disambiguationData":[TD([[makeQuery(id+"F0.imprint","IMPRINT",EDGE,{"derivedFrom":subQ0}),1.0]])]});}
            var Q49;
            Q49=makeQuery(id+"F0.imprint","IMPRINT",FACE,{"disambiguationData":[TD([[makeQuery(id+"F0.imprint","IMPRINT",EDGE,{"derivedFrom":sQuery(id+"F0.wireOp",EDGE,"E10.0.1.10")}),-1.0]])]});
            var Q50;
            {var subQ0=sQuery(id+"F0.wireOp",EDGE,"E38.6.0.0");Q50=makeQuery(id+"F0.imprint","IMPRINT",FACE,{"disambiguationData":[TD([[makeQuery(id+"F0.imprint","IMPRINT",EDGE,{"derivedFrom":subQ0}),-1.0]])]});}
            var Q51;
            {var subQ0=sQuery(id+"F0.wireOp",EDGE,"E58.1.0.3");Q51=makeQuery(id+"F0.imprint","IMPRINT",FACE,{"disambiguationData":[TD([[makeQuery(id+"F0.imprint","IMPRINT",EDGE,{"derivedFrom":subQ0}),-1.0]])]});}
            var Q52;
            {var subQ0=sQuery(id+"F0.wireOp",EDGE,"E39.4.0.1");Q52=makeQuery(id+"F0.imprint","IMPRINT",FACE,{"disambiguationData":[TD([[makeQuery(id+"F0.imprint","IMPRINT",EDGE,{"derivedFrom":subQ0}),1.0]])]});}
            var Q53;
            {var subQ0=sQuery(id+"F0.wireOp",EDGE,"E38.6.0.2");Q53=makeQuery(id+"F0.imprint","IMPRINT",FACE,{"disambiguationData":[TD([[makeQuery(id+"F0.imprint","IMPRINT",EDGE,{"derivedFrom":subQ0}),1.0]])]});}
            var Q54;
            Q54=makeQuery(id+"F0.imprint","IMPRINT",FACE,{"disambiguationData":[TD([[makeQuery(id+"F0.imprint","IMPRINT",EDGE,{"derivedFrom":sQuery(id+"F0.wireOp",EDGE,"E9.6.0.0")}),-1.0]])]});
            var Q55;
            {var subQ0=sQuery(id+"F0.wireOp",EDGE,"E59.1.0.0");Q55=makeQuery(id+"F0.imprint","IMPRINT",FACE,{"disambiguationData":[TD([[makeQuery(id+"F0.imprint","IMPRINT",EDGE,{"derivedFrom":subQ0}),-1.0]])]});}
            var Q56;
            Q56=makeQuery(id+"F0.imprint","IMPRINT",FACE,{"disambiguationData":[TD([[makeQuery(id+"F0.imprint","IMPRINT",EDGE,{"derivedFrom":sQuery(id+"F0.wireOp",EDGE,"E9.7.0.6")}),-1.0]])]});
            var Q57;
            {var subQ0=sQuery(id+"F0.wireOp",EDGE,"E31.7.0.4");Q57=makeQuery(id+"F0.imprint","IMPRINT",FACE,{"disambiguationData":[TD([[makeQuery(id+"F0.imprint","IMPRINT",EDGE,{"derivedFrom":subQ0}),-1.0]])]});}
            var Q58;
            {var subQ0=sQuery(id+"F0.wireOp",EDGE,"E59.1.0.2");Q58=makeQuery(id+"F0.imprint","IMPRINT",FACE,{"disambiguationData":[TD([[makeQuery(id+"F0.imprint","IMPRINT",EDGE,{"derivedFrom":subQ0}),1.0]])]});}
            var Q59;
            {var subQ0=sQuery(id+"F0.wireOp",EDGE,"E39.4.0.10");Q59=makeQuery(id+"F0.imprint","IMPRINT",FACE,{"disambiguationData":[TD([[makeQuery(id+"F0.imprint","IMPRINT",EDGE,{"derivedFrom":subQ0}),1.0]])]});}
            var Q60;
            {var subQ0=sQuery(id+"F0.wireOp",EDGE,"E54.1.0.6");Q60=makeQuery(id+"F0.imprint","IMPRINT",FACE,{"disambiguationData":[TD([[makeQuery(id+"F0.imprint","IMPRINT",EDGE,{"derivedFrom":subQ0}),1.0]])]});}
            var Q61;
            {var subQ0=sQuery(id+"F0.wireOp",EDGE,"E64.1.0.7");Q61=makeQuery(id+"F0.imprint","IMPRINT",FACE,{"disambiguationData":[TD([[makeQuery(id+"F0.imprint","IMPRINT",EDGE,{"derivedFrom":subQ0}),1.0]])]});}
            var Q62;
            {var subQ0=sQuery(id+"F0.wireOp",EDGE,"E31.2.0.4");Q62=makeQuery(id+"F0.imprint","IMPRINT",FACE,{"disambiguationData":[TD([[makeQuery(id+"F0.imprint","IMPRINT",EDGE,{"derivedFrom":subQ0}),-1.0]])]});}
            var Q63;
            {var subQ0=sQuery(id+"F0.wireOp",EDGE,"E26.trimOffspring");Q63=makeQuery(id+"F0.imprint","IMPRINT",FACE,{"disambiguationData":[TD([[makeQuery(id+"F0.imprint","IMPRINT",EDGE,{"derivedFrom":subQ0}),1.0]])]});}
            var Q64;
            {var subQ0=sQuery(id+"F0.wireOp",EDGE,"E38.2.0.0");Q64=makeQuery(id+"F0.imprint","IMPRINT",FACE,{"disambiguationData":[TD([[makeQuery(id+"F0.imprint","IMPRINT",EDGE,{"derivedFrom":subQ0}),-1.0]])]});}
            var Q65;
            {var subQ0=sQuery(id+"F0.wireOp",EDGE,"E54.1.0.0");Q65=makeQuery(id+"F0.imprint","IMPRINT",FACE,{"disambiguationData":[TD([[makeQuery(id+"F0.imprint","IMPRINT",EDGE,{"derivedFrom":subQ0}),1.0]])]});}
            var Q66;
            {var subQ0=sQuery(id+"F0.wireOp",EDGE,"E31.3.0.4");Q66=makeQuery(id+"F0.imprint","IMPRINT",FACE,{"disambiguationData":[TD([[makeQuery(id+"F0.imprint","IMPRINT",EDGE,{"derivedFrom":subQ0}),-1.0]])]});}
            var Q67;
            {var subQ0=sQuery(id+"F0.wireOp",EDGE,"E39.1.0.3");Q67=makeQuery(id+"F0.imprint","IMPRINT",FACE,{"disambiguationData":[TD([[makeQuery(id+"F0.imprint","IMPRINT",EDGE,{"derivedFrom":subQ0}),1.0]])]});}
            var Q68;
            {var subQ0=sQuery(id+"F0.wireOp",EDGE,"E38.3.0.0");Q68=makeQuery(id+"F0.imprint","IMPRINT",FACE,{"disambiguationData":[TD([[makeQuery(id+"F0.imprint","IMPRINT",EDGE,{"derivedFrom":subQ0}),-1.0]])]});}
            var Q69;
            {var subQ0=sQuery(id+"F0.wireOp",EDGE,"E54.2.0.0");Q69=makeQuery(id+"F0.imprint","IMPRINT",FACE,{"disambiguationData":[TD([[makeQuery(id+"F0.imprint","IMPRINT",EDGE,{"derivedFrom":subQ0}),1.0]])]});}
            var Q70;
            {var subQ0=sQuery(id+"F0.wireOp",EDGE,"E31.4.0.4");Q70=makeQuery(id+"F0.imprint","IMPRINT",FACE,{"disambiguationData":[TD([[makeQuery(id+"F0.imprint","IMPRINT",EDGE,{"derivedFrom":subQ0}),-1.0]])]});}
            var Q71;
            {var subQ0=sQuery(id+"F0.wireOp",EDGE,"E39.2.0.3");Q71=makeQuery(id+"F0.imprint","IMPRINT",FACE,{"disambiguationData":[TD([[makeQuery(id+"F0.imprint","IMPRINT",EDGE,{"derivedFrom":subQ0}),1.0]])]});}
            var Q72;
            {var subQ0=sQuery(id+"F0.wireOp",EDGE,"E38.4.0.0");Q72=makeQuery(id+"F0.imprint","IMPRINT",FACE,{"disambiguationData":[TD([[makeQuery(id+"F0.imprint","IMPRINT",EDGE,{"derivedFrom":subQ0}),-1.0]])]});}
            var Q73;
            {var subQ0=sQuery(id+"F0.wireOp",EDGE,"E54.3.0.0");Q73=makeQuery(id+"F0.imprint","IMPRINT",FACE,{"disambiguationData":[TD([[makeQuery(id+"F0.imprint","IMPRINT",EDGE,{"derivedFrom":subQ0}),1.0]])]});}
            var Q74;
            {var subQ0=sQuery(id+"F0.wireOp",EDGE,"E31.5.0.4");Q74=makeQuery(id+"F0.imprint","IMPRINT",FACE,{"disambiguationData":[TD([[makeQuery(id+"F0.imprint","IMPRINT",EDGE,{"derivedFrom":subQ0}),-1.0]])]});}
            var Q75;
            {var subQ0=sQuery(id+"F0.wireOp",EDGE,"E39.3.0.3");Q75=makeQuery(id+"F0.imprint","IMPRINT",FACE,{"disambiguationData":[TD([[makeQuery(id+"F0.imprint","IMPRINT",EDGE,{"derivedFrom":subQ0}),1.0]])]});}
            var Q76;
            {var subQ0=sQuery(id+"F0.wireOp",EDGE,"E38.5.0.0");Q76=makeQuery(id+"F0.imprint","IMPRINT",FACE,{"disambiguationData":[TD([[makeQuery(id+"F0.imprint","IMPRINT",EDGE,{"derivedFrom":subQ0}),-1.0]])]});}
            var Q77;
            {var subQ0=sQuery(id+"F0.wireOp",EDGE,"E54.4.0.0");Q77=makeQuery(id+"F0.imprint","IMPRINT",FACE,{"disambiguationData":[TD([[makeQuery(id+"F0.imprint","IMPRINT",EDGE,{"derivedFrom":subQ0}),1.0]])]});}
            var Q78;
            {var subQ0=sQuery(id+"F0.wireOp",EDGE,"E31.6.0.4");Q78=makeQuery(id+"F0.imprint","IMPRINT",FACE,{"disambiguationData":[TD([[makeQuery(id+"F0.imprint","IMPRINT",EDGE,{"derivedFrom":subQ0}),-1.0]])]});}
            var Q79;
            {var subQ0=sQuery(id+"F0.wireOp",EDGE,"E58.1.0.5");Q79=makeQuery(id+"F0.imprint","IMPRINT",FACE,{"disambiguationData":[TD([[makeQuery(id+"F0.imprint","IMPRINT",EDGE,{"derivedFrom":subQ0}),1.0]])]});}
            var Q80;
            {var subQ0=sQuery(id+"F0.wireOp",EDGE,"E39.3.0.10");Q80=makeQuery(id+"F0.imprint","IMPRINT",FACE,{"disambiguationData":[TD([[makeQuery(id+"F0.imprint","IMPRINT",EDGE,{"derivedFrom":subQ0}),1.0]])]});}
            extrude(context, id + "F2", {"entities" : qUnion([Q0, Q1, Q2, Q3, Q4, Q5, Q6, Q7, Q8, Q9, Q10, Q11, Q12, Q13, Q14, Q15, Q16, Q17, Q18, Q19, Q20, Q21, Q22, Q23, Q24, Q25, Q26, Q27, Q28, Q29, Q30, Q31, Q32, Q33, Q34, Q35, Q36, Q37, Q38, Q39, Q40, Q41, Q42, Q43, Q44, Q45, Q46, Q47, Q48, Q49, Q50, Q51, Q52, Q53, Q54, Q55, Q56, Q57, Q58, Q59, Q60, Q61, Q62, Q63, Q64, Q65, Q66, Q67, Q68, Q69, Q70, Q71, Q72, Q73, Q74, Q75, Q76, Q77, Q78, Q79, Q80]), "depth" : 79.38 * mm, "offsetDistance" : 25.4 * mm, "hasSecondDirection" : true, "secondDirectionOppositeDirection" : false, "secondDirectionDepth" : 76.2 * mm});
        }
        {
            var Q0;
            Q0=makeQuery(id+"F0.imprint","IMPRINT",FACE,{"disambiguationData":[TD([[makeQuery(id+"F0.imprint","IMPRINT",EDGE,{"derivedFrom":sQuery(id+"F0.wireOp",EDGE,"E5")}),-1.0]])]});
            var Q1;
            {var subQ10=sQuery(id+"F0.wireOp",EDGE,"E2.0");Q1=makeQuery(id+"F0.imprint","IMPRINT",FACE,{"disambiguationData":[TD([[makeQuery(id+"F0.imprint","IMPRINT",EDGE,{"derivedFrom":subQ10}),-1.0]])]});}
            var Q2;
            Q2=makeQuery(id+"F0.imprint","IMPRINT",FACE,{"disambiguationData":[TD([[makeQuery(id+"F0.imprint","IMPRINT",EDGE,{"derivedFrom":sQuery(id+"F0.wireOp",EDGE,"E10.0.1.15")}),-1.0]])]});
            var Q3;
            {var subQ0=sQuery(id+"F0.wireOp",EDGE,"E66.1.0.0");Q3=makeQuery(id+"F0.imprint","IMPRINT",FACE,{"disambiguationData":[TD([[makeQuery(id+"F0.imprint","IMPRINT",EDGE,{"derivedFrom":subQ0}),1.0]])]});}
            var Q4;
            {var subQ0=sQuery(id+"F0.wireOp",EDGE,"E61.1.0.1");Q4=makeQuery(id+"F0.imprint","IMPRINT",FACE,{"disambiguationData":[TD([[makeQuery(id+"F0.imprint","IMPRINT",EDGE,{"derivedFrom":subQ0}),1.0]])]});}
            var Q5;
            {var subQ0=sQuery(id+"F0.wireOp",EDGE,"E61.1.0.0");Q5=makeQuery(id+"F0.imprint","IMPRINT",FACE,{"disambiguationData":[TD([[makeQuery(id+"F0.imprint","IMPRINT",EDGE,{"derivedFrom":subQ0}),1.0]])]});}
            var Q6;
            Q6=makeQuery(id+"F0.imprint","IMPRINT",FACE,{"disambiguationData":[TD([[makeQuery(id+"F0.imprint","IMPRINT",EDGE,{"derivedFrom":sQuery(id+"F0.wireOp",EDGE,"E10.0.1.49")}),-1.0]])]});
            var Q7;
            {var subQ0=sQuery(id+"F0.wireOp",EDGE,"E61.1.0.7");Q7=makeQuery(id+"F0.imprint","IMPRINT",FACE,{"disambiguationData":[TD([[makeQuery(id+"F0.imprint","IMPRINT",EDGE,{"derivedFrom":subQ0}),1.0]])]});}
            var Q8;
            Q8=makeQuery(id+"F0.imprint","IMPRINT",FACE,{"disambiguationData":[TD([[makeQuery(id+"F0.imprint","IMPRINT",EDGE,{"derivedFrom":sQuery(id+"F0.wireOp",EDGE,"E10.0.2.111")}),-1.0]])]});
            var Q9;
            {var subQ0=sQuery(id+"F0.wireOp",EDGE,"E61.1.0.5");Q9=makeQuery(id+"F0.imprint","IMPRINT",FACE,{"disambiguationData":[TD([[makeQuery(id+"F0.imprint","IMPRINT",EDGE,{"derivedFrom":subQ0}),1.0]])]});}
            var Q10;
            Q10=makeQuery(id+"F0.imprint","IMPRINT",FACE,{"disambiguationData":[TD([[makeQuery(id+"F0.imprint","IMPRINT",EDGE,{"derivedFrom":sQuery(id+"F0.wireOp",EDGE,"E10.0.2.104")}),-1.0]])]});
            var Q11;
            {var subQ0=sQuery(id+"F0.wireOp",EDGE,"E61.1.0.3");Q11=makeQuery(id+"F0.imprint","IMPRINT",FACE,{"disambiguationData":[TD([[makeQuery(id+"F0.imprint","IMPRINT",EDGE,{"derivedFrom":subQ0}),1.0]])]});}
            var Q12;
            Q12=makeQuery(id+"F0.imprint","IMPRINT",FACE,{"disambiguationData":[TD([[makeQuery(id+"F0.imprint","IMPRINT",EDGE,{"derivedFrom":sQuery(id+"F0.wireOp",EDGE,"E10.0.3.44")}),-1.0]])]});
            var Q13;
            {var subQ0=sQuery(id+"F0.wireOp",EDGE,"E39.2.0.11");Q13=makeQuery(id+"F0.imprint","IMPRINT",FACE,{"disambiguationData":[TD([[makeQuery(id+"F0.imprint","IMPRINT",EDGE,{"derivedFrom":subQ0}),1.0]])]});}
            var Q14;
            Q14=makeQuery(id+"F0.imprint","IMPRINT",FACE,{"disambiguationData":[TD([[makeQuery(id+"F0.imprint","IMPRINT",EDGE,{"derivedFrom":sQuery(id+"F0.wireOp",EDGE,"E10.0.2.35")}),-1.0]])]});
            var Q15;
            {var subQ0=sQuery(id+"F0.wireOp",EDGE,"E50.trimOffspring");Q15=makeQuery(id+"F0.imprint","IMPRINT",FACE,{"disambiguationData":[TD([[makeQuery(id+"F0.imprint","IMPRINT",EDGE,{"derivedFrom":subQ0}),1.0]])]});}
            var Q16;
            Q16=makeQuery(id+"F0.imprint","IMPRINT",FACE,{"disambiguationData":[TD([[makeQuery(id+"F0.imprint","IMPRINT",EDGE,{"derivedFrom":sQuery(id+"F0.wireOp",EDGE,"E10.0.3.96")}),-1.0]])]});
            var Q17;
            {var subQ0=sQuery(id+"F0.wireOp",EDGE,"E39.3.0.11");Q17=makeQuery(id+"F0.imprint","IMPRINT",FACE,{"disambiguationData":[TD([[makeQuery(id+"F0.imprint","IMPRINT",EDGE,{"derivedFrom":subQ0}),1.0]])]});}
            var Q18;
            Q18=makeQuery(id+"F0.imprint","IMPRINT",FACE,{"disambiguationData":[TD([[makeQuery(id+"F0.imprint","IMPRINT",EDGE,{"derivedFrom":sQuery(id+"F0.wireOp",EDGE,"E10.0.2.89")}),-1.0]])]});
            var Q19;
            {var subQ0=sQuery(id+"F0.wireOp",EDGE,"E54.1.0.3");Q19=makeQuery(id+"F0.imprint","IMPRINT",FACE,{"disambiguationData":[TD([[makeQuery(id+"F0.imprint","IMPRINT",EDGE,{"derivedFrom":subQ0}),1.0]])]});}
            var Q20;
            Q20=makeQuery(id+"F0.imprint","IMPRINT",FACE,{"disambiguationData":[TD([[makeQuery(id+"F0.imprint","IMPRINT",EDGE,{"derivedFrom":sQuery(id+"F0.wireOp",EDGE,"E10.0.3.27")}),-1.0]])]});
            var Q21;
            {var subQ0=sQuery(id+"F0.wireOp",EDGE,"E39.4.0.11");Q21=makeQuery(id+"F0.imprint","IMPRINT",FACE,{"disambiguationData":[TD([[makeQuery(id+"F0.imprint","IMPRINT",EDGE,{"derivedFrom":subQ0}),1.0]])]});}
            var Q22;
            Q22=makeQuery(id+"F0.imprint","IMPRINT",FACE,{"disambiguationData":[TD([[makeQuery(id+"F0.imprint","IMPRINT",EDGE,{"derivedFrom":sQuery(id+"F0.wireOp",EDGE,"E10.0.2.19")}),-1.0]])]});
            var Q23;
            {var subQ0=sQuery(id+"F0.wireOp",EDGE,"E54.2.0.3");Q23=makeQuery(id+"F0.imprint","IMPRINT",FACE,{"disambiguationData":[TD([[makeQuery(id+"F0.imprint","IMPRINT",EDGE,{"derivedFrom":subQ0}),1.0]])]});}
            var Q24;
            Q24=makeQuery(id+"F0.imprint","IMPRINT",FACE,{"disambiguationData":[TD([[makeQuery(id+"F0.imprint","IMPRINT",EDGE,{"derivedFrom":sQuery(id+"F0.wireOp",EDGE,"E10.0.3.76")}),-1.0]])]});
            var Q25;
            {var subQ0=sQuery(id+"F0.wireOp",EDGE,"E55.1.0.1");Q25=makeQuery(id+"F0.imprint","IMPRINT",FACE,{"disambiguationData":[TD([[makeQuery(id+"F0.imprint","IMPRINT",EDGE,{"derivedFrom":subQ0}),1.0]])]});}
            var Q26;
            Q26=makeQuery(id+"F0.imprint","IMPRINT",FACE,{"disambiguationData":[TD([[makeQuery(id+"F0.imprint","IMPRINT",EDGE,{"derivedFrom":sQuery(id+"F0.wireOp",EDGE,"E10.0.2.69")}),-1.0]])]});
            var Q27;
            {var subQ0=sQuery(id+"F0.wireOp",EDGE,"E55.1.0.5");Q27=makeQuery(id+"F0.imprint","IMPRINT",FACE,{"disambiguationData":[TD([[makeQuery(id+"F0.imprint","IMPRINT",EDGE,{"derivedFrom":subQ0}),1.0]])]});}
            var Q28;
            Q28=makeQuery(id+"F0.imprint","IMPRINT",FACE,{"disambiguationData":[TD([[makeQuery(id+"F0.imprint","IMPRINT",EDGE,{"derivedFrom":sQuery(id+"F0.wireOp",EDGE,"E10.0.2.10")}),-1.0]])]});
            var Q29;
            {var subQ0=sQuery(id+"F0.wireOp",EDGE,"E55.1.0.4");Q29=makeQuery(id+"F0.imprint","IMPRINT",FACE,{"disambiguationData":[TD([[makeQuery(id+"F0.imprint","IMPRINT",EDGE,{"derivedFrom":subQ0}),1.0]])]});}
            var Q30;
            Q30=makeQuery(id+"F0.imprint","IMPRINT",FACE,{"disambiguationData":[TD([[makeQuery(id+"F0.imprint","IMPRINT",EDGE,{"derivedFrom":sQuery(id+"F0.wireOp",EDGE,"E10.0.1.2")}),-1.0]])]});
            var Q31;
            {var subQ0=sQuery(id+"F0.wireOp",EDGE,"E55.1.0.2");Q31=makeQuery(id+"F0.imprint","IMPRINT",FACE,{"disambiguationData":[TD([[makeQuery(id+"F0.imprint","IMPRINT",EDGE,{"derivedFrom":subQ0}),1.0]])]});}
            var Q32;
            Q32=makeQuery(id+"F0.imprint","IMPRINT",FACE,{"disambiguationData":[TD([[makeQuery(id+"F0.imprint","IMPRINT",EDGE,{"derivedFrom":sQuery(id+"F0.wireOp",EDGE,"E10.0.1.61")}),-1.0]])]});
            var Q33;
            {var subQ0=sQuery(id+"F0.wireOp",EDGE,"E55.1.0.0");Q33=makeQuery(id+"F0.imprint","IMPRINT",FACE,{"disambiguationData":[TD([[makeQuery(id+"F0.imprint","IMPRINT",EDGE,{"derivedFrom":subQ0}),1.0]])]});}
            var Q34;
            Q34=makeQuery(id+"F0.imprint","IMPRINT",FACE,{"disambiguationData":[TD([[makeQuery(id+"F0.imprint","IMPRINT",EDGE,{"derivedFrom":sQuery(id+"F0.wireOp",EDGE,"E9.8.0.6")}),-1.0]])]});
            var Q35;
            {var subQ0=sQuery(id+"F0.wireOp",EDGE,"E60.1.0.0");Q35=makeQuery(id+"F0.imprint","IMPRINT",FACE,{"disambiguationData":[TD([[makeQuery(id+"F0.imprint","IMPRINT",EDGE,{"derivedFrom":subQ0}),1.0]])]});}
            var Q36;
            Q36=makeQuery(id+"F0.imprint","IMPRINT",FACE,{"disambiguationData":[TD([[makeQuery(id+"F0.imprint","IMPRINT",EDGE,{"derivedFrom":sQuery(id+"F0.wireOp",EDGE,"E9.7.0.0")}),-1.0]])]});
            var Q37;
            {var subQ0=sQuery(id+"F0.wireOp",EDGE,"E38.7.0.2");Q37=makeQuery(id+"F0.imprint","IMPRINT",FACE,{"disambiguationData":[TD([[makeQuery(id+"F0.imprint","IMPRINT",EDGE,{"derivedFrom":subQ0}),1.0]])]});}
            var Q38;
            {var subQ0=sQuery(id+"F0.wireOp",EDGE,"E35.trimOffspring");Q38=makeQuery(id+"F0.imprint","IMPRINT",FACE,{"disambiguationData":[TD([[makeQuery(id+"F0.imprint","IMPRINT",EDGE,{"derivedFrom":subQ0}),1.0]])]});}
            var Q39;
            {var subQ0=sQuery(id+"F0.wireOp",EDGE,"E40");Q39=makeQuery(id+"F0.imprint","IMPRINT",FACE,{"disambiguationData":[TD([[makeQuery(id+"F0.imprint","IMPRINT",EDGE,{"derivedFrom":subQ0}),-1.0]])]});}
            var Q40;
            {var subQ0=sQuery(id+"F0.wireOp",EDGE,"E65.1.0.3");Q40=makeQuery(id+"F0.imprint","IMPRINT",FACE,{"disambiguationData":[TD([[makeQuery(id+"F0.imprint","IMPRINT",EDGE,{"derivedFrom":subQ0}),1.0]])]});}
            var Q41;
            {var subQ0=sQuery(id+"F0.wireOp",EDGE,"E31.1.0.4");Q41=makeQuery(id+"F0.imprint","IMPRINT",FACE,{"disambiguationData":[TD([[makeQuery(id+"F0.imprint","IMPRINT",EDGE,{"derivedFrom":subQ0}),-1.0]])]});}
            var Q42;
            {var subQ0=sQuery(id+"F0.wireOp",EDGE,"E64.1.0.2");Q42=makeQuery(id+"F0.imprint","IMPRINT",FACE,{"disambiguationData":[TD([[makeQuery(id+"F0.imprint","IMPRINT",EDGE,{"derivedFrom":subQ0}),1.0]])]});}
            var Q43;
            {var subQ0=sQuery(id+"F0.wireOp",EDGE,"E38.1.0.0");Q43=makeQuery(id+"F0.imprint","IMPRINT",FACE,{"disambiguationData":[TD([[makeQuery(id+"F0.imprint","IMPRINT",EDGE,{"derivedFrom":subQ0}),-1.0]])]});}
            var Q44;
            {var subQ0=sQuery(id+"F0.wireOp",EDGE,"E24.trimOffspring");Q44=makeQuery(id+"F0.imprint","IMPRINT",FACE,{"disambiguationData":[TD([[makeQuery(id+"F0.imprint","IMPRINT",EDGE,{"derivedFrom":subQ0}),1.0]])]});}
            var Q45;
            {var subQ0=sQuery(id+"F0.wireOp",EDGE,"E31.2.0.2");Q45=makeQuery(id+"F0.imprint","IMPRINT",FACE,{"disambiguationData":[TD([[makeQuery(id+"F0.imprint","IMPRINT",EDGE,{"derivedFrom":subQ0}),-1.0]])]});}
            var Q46;
            {var subQ0=sQuery(id+"F0.wireOp",EDGE,"E39.1.0.2");Q46=makeQuery(id+"F0.imprint","IMPRINT",FACE,{"disambiguationData":[TD([[makeQuery(id+"F0.imprint","IMPRINT",EDGE,{"derivedFrom":subQ0}),1.0]])]});}
            var Q47;
            {var subQ0=sQuery(id+"F0.wireOp",EDGE,"E38.2.0.1");Q47=makeQuery(id+"F0.imprint","IMPRINT",FACE,{"disambiguationData":[TD([[makeQuery(id+"F0.imprint","IMPRINT",EDGE,{"derivedFrom":subQ0}),1.0]])]});}
            var Q48;
            {var subQ0=sQuery(id+"F0.wireOp",EDGE,"E48.trimOffspring");Q48=makeQuery(id+"F0.imprint","IMPRINT",FACE,{"disambiguationData":[TD([[makeQuery(id+"F0.imprint","IMPRINT",EDGE,{"derivedFrom":subQ0}),1.0]])]});}
            var Q49;
            {var subQ0=sQuery(id+"F0.wireOp",EDGE,"E31.3.0.2");Q49=makeQuery(id+"F0.imprint","IMPRINT",FACE,{"disambiguationData":[TD([[makeQuery(id+"F0.imprint","IMPRINT",EDGE,{"derivedFrom":subQ0}),-1.0]])]});}
            var Q50;
            {var subQ0=sQuery(id+"F0.wireOp",EDGE,"E39.2.0.2");Q50=makeQuery(id+"F0.imprint","IMPRINT",FACE,{"disambiguationData":[TD([[makeQuery(id+"F0.imprint","IMPRINT",EDGE,{"derivedFrom":subQ0}),1.0]])]});}
            var Q51;
            {var subQ0=sQuery(id+"F0.wireOp",EDGE,"E38.3.0.1");Q51=makeQuery(id+"F0.imprint","IMPRINT",FACE,{"disambiguationData":[TD([[makeQuery(id+"F0.imprint","IMPRINT",EDGE,{"derivedFrom":subQ0}),1.0]])]});}
            var Q52;
            {var subQ0=sQuery(id+"F0.wireOp",EDGE,"E54.1.0.5");Q52=makeQuery(id+"F0.imprint","IMPRINT",FACE,{"disambiguationData":[TD([[makeQuery(id+"F0.imprint","IMPRINT",EDGE,{"derivedFrom":subQ0}),1.0]])]});}
            var Q53;
            {var subQ0=sQuery(id+"F0.wireOp",EDGE,"E39.3.0.2");Q53=makeQuery(id+"F0.imprint","IMPRINT",FACE,{"disambiguationData":[TD([[makeQuery(id+"F0.imprint","IMPRINT",EDGE,{"derivedFrom":subQ0}),1.0]])]});}
            var Q54;
            {var subQ0=sQuery(id+"F0.wireOp",EDGE,"E38.4.0.1");Q54=makeQuery(id+"F0.imprint","IMPRINT",FACE,{"disambiguationData":[TD([[makeQuery(id+"F0.imprint","IMPRINT",EDGE,{"derivedFrom":subQ0}),1.0]])]});}
            var Q55;
            {var subQ0=sQuery(id+"F0.wireOp",EDGE,"E54.2.0.5");Q55=makeQuery(id+"F0.imprint","IMPRINT",FACE,{"disambiguationData":[TD([[makeQuery(id+"F0.imprint","IMPRINT",EDGE,{"derivedFrom":subQ0}),1.0]])]});}
            var Q56;
            {var subQ0=sQuery(id+"F0.wireOp",EDGE,"E39.4.0.2");Q56=makeQuery(id+"F0.imprint","IMPRINT",FACE,{"disambiguationData":[TD([[makeQuery(id+"F0.imprint","IMPRINT",EDGE,{"derivedFrom":subQ0}),1.0]])]});}
            var Q57;
            {var subQ0=sQuery(id+"F0.wireOp",EDGE,"E38.5.0.1");Q57=makeQuery(id+"F0.imprint","IMPRINT",FACE,{"disambiguationData":[TD([[makeQuery(id+"F0.imprint","IMPRINT",EDGE,{"derivedFrom":subQ0}),1.0]])]});}
            var Q58;
            {var subQ0=sQuery(id+"F0.wireOp",EDGE,"E54.3.0.5");Q58=makeQuery(id+"F0.imprint","IMPRINT",FACE,{"disambiguationData":[TD([[makeQuery(id+"F0.imprint","IMPRINT",EDGE,{"derivedFrom":subQ0}),1.0]])]});}
            var Q59;
            {var subQ0=sQuery(id+"F0.wireOp",EDGE,"E31.6.0.2");Q59=makeQuery(id+"F0.imprint","IMPRINT",FACE,{"disambiguationData":[TD([[makeQuery(id+"F0.imprint","IMPRINT",EDGE,{"derivedFrom":subQ0}),-1.0]])]});}
            var Q60;
            {var subQ0=sQuery(id+"F0.wireOp",EDGE,"E54.4.0.8");Q60=makeQuery(id+"F0.imprint","IMPRINT",FACE,{"disambiguationData":[TD([[makeQuery(id+"F0.imprint","IMPRINT",EDGE,{"derivedFrom":subQ0}),1.0]])]});}
            var Q61;
            {var subQ0=sQuery(id+"F0.wireOp",EDGE,"E38.6.0.0");Q61=makeQuery(id+"F0.imprint","IMPRINT",FACE,{"disambiguationData":[TD([[makeQuery(id+"F0.imprint","IMPRINT",EDGE,{"derivedFrom":subQ0}),-1.0]])]});}
            var Q62;
            {var subQ0=sQuery(id+"F0.wireOp",EDGE,"E58.1.0.3");Q62=makeQuery(id+"F0.imprint","IMPRINT",FACE,{"disambiguationData":[TD([[makeQuery(id+"F0.imprint","IMPRINT",EDGE,{"derivedFrom":subQ0}),-1.0]])]});}
            var Q63;
            {var subQ0=sQuery(id+"F0.wireOp",EDGE,"E31.7.0.4");Q63=makeQuery(id+"F0.imprint","IMPRINT",FACE,{"disambiguationData":[TD([[makeQuery(id+"F0.imprint","IMPRINT",EDGE,{"derivedFrom":subQ0}),-1.0]])]});}
            var Q64;
            {var subQ0=sQuery(id+"F0.wireOp",EDGE,"E59.1.0.2");Q64=makeQuery(id+"F0.imprint","IMPRINT",FACE,{"disambiguationData":[TD([[makeQuery(id+"F0.imprint","IMPRINT",EDGE,{"derivedFrom":subQ0}),1.0]])]});}
            var Q65;
            {var subQ0=sQuery(id+"F0.wireOp",EDGE,"E39.4.0.10");Q65=makeQuery(id+"F0.imprint","IMPRINT",FACE,{"disambiguationData":[TD([[makeQuery(id+"F0.imprint","IMPRINT",EDGE,{"derivedFrom":subQ0}),1.0]])]});}
            var Q66;
            {var subQ0=sQuery(id+"F0.wireOp",EDGE,"E34.trimOffspring");Q66=makeQuery(id+"F0.imprint","IMPRINT",FACE,{"disambiguationData":[TD([[makeQuery(id+"F0.imprint","IMPRINT",EDGE,{"derivedFrom":subQ0}),1.0]])]});}
            var Q67;
            {var subQ0=sQuery(id+"F0.wireOp",EDGE,"E64.1.0.1");Q67=makeQuery(id+"F0.imprint","IMPRINT",FACE,{"disambiguationData":[TD([[makeQuery(id+"F0.imprint","IMPRINT",EDGE,{"derivedFrom":subQ0}),1.0]])]});}
            var Q68;
            {var subQ0=sQuery(id+"F0.wireOp",EDGE,"E31.1.0.2");Q68=makeQuery(id+"F0.imprint","IMPRINT",FACE,{"disambiguationData":[TD([[makeQuery(id+"F0.imprint","IMPRINT",EDGE,{"derivedFrom":subQ0}),-1.0]])]});}
            var Q69;
            {var subQ0=sQuery(id+"F0.wireOp",EDGE,"E22.trimOffspring");Q69=makeQuery(id+"F0.imprint","IMPRINT",FACE,{"disambiguationData":[TD([[makeQuery(id+"F0.imprint","IMPRINT",EDGE,{"derivedFrom":subQ0}),1.0]])]});}
            var Q70;
            {var subQ0=sQuery(id+"F0.wireOp",EDGE,"E38.1.0.1");Q70=makeQuery(id+"F0.imprint","IMPRINT",FACE,{"disambiguationData":[TD([[makeQuery(id+"F0.imprint","IMPRINT",EDGE,{"derivedFrom":subQ0}),1.0]])]});}
            var Q71;
            {var subQ0=sQuery(id+"F0.wireOp",EDGE,"E39.1.0.11");Q71=makeQuery(id+"F0.imprint","IMPRINT",FACE,{"disambiguationData":[TD([[makeQuery(id+"F0.imprint","IMPRINT",EDGE,{"derivedFrom":subQ0}),1.0]])]});}
            var Q72;
            {var subQ0=sQuery(id+"F0.wireOp",EDGE,"E54.3.0.3");Q72=makeQuery(id+"F0.imprint","IMPRINT",FACE,{"disambiguationData":[TD([[makeQuery(id+"F0.imprint","IMPRINT",EDGE,{"derivedFrom":subQ0}),1.0]])]});}
            var Q73;
            {var subQ0=sQuery(id+"F0.wireOp",EDGE,"E38.6.0.1");Q73=makeQuery(id+"F0.imprint","IMPRINT",FACE,{"disambiguationData":[TD([[makeQuery(id+"F0.imprint","IMPRINT",EDGE,{"derivedFrom":subQ0}),1.0]])]});}
            var Q74;
            {var subQ0=sQuery(id+"F0.wireOp",EDGE,"E54.4.0.5");Q74=makeQuery(id+"F0.imprint","IMPRINT",FACE,{"disambiguationData":[TD([[makeQuery(id+"F0.imprint","IMPRINT",EDGE,{"derivedFrom":subQ0}),1.0]])]});}
            var Q75;
            {var subQ0=sQuery(id+"F0.wireOp",EDGE,"E31.7.0.2");Q75=makeQuery(id+"F0.imprint","IMPRINT",FACE,{"disambiguationData":[TD([[makeQuery(id+"F0.imprint","IMPRINT",EDGE,{"derivedFrom":subQ0}),-1.0]])]});}
            var Q76;
            {var subQ0=sQuery(id+"F0.wireOp",EDGE,"E58.1.0.4");Q76=makeQuery(id+"F0.imprint","IMPRINT",FACE,{"disambiguationData":[TD([[makeQuery(id+"F0.imprint","IMPRINT",EDGE,{"derivedFrom":subQ0}),1.0]])]});}
            var Q77;
            {var subQ0=sQuery(id+"F0.wireOp",EDGE,"E38.7.0.0");Q77=makeQuery(id+"F0.imprint","IMPRINT",FACE,{"disambiguationData":[TD([[makeQuery(id+"F0.imprint","IMPRINT",EDGE,{"derivedFrom":subQ0}),-1.0]])]});}
            var Q78;
            {var subQ0=sQuery(id+"F0.wireOp",EDGE,"E59.1.0.1");Q78=makeQuery(id+"F0.imprint","IMPRINT",FACE,{"disambiguationData":[TD([[makeQuery(id+"F0.imprint","IMPRINT",EDGE,{"derivedFrom":subQ0}),1.0]])]});}
            var Q79;
            {var subQ0=sQuery(id+"F0.wireOp",EDGE,"E31.8.0.4");Q79=makeQuery(id+"F0.imprint","IMPRINT",FACE,{"disambiguationData":[TD([[makeQuery(id+"F0.imprint","IMPRINT",EDGE,{"derivedFrom":subQ0}),-1.0]])]});}
            var Q80;
            {var subQ0=sQuery(id+"F0.wireOp",EDGE,"E65.1.0.2");Q80=makeQuery(id+"F0.imprint","IMPRINT",FACE,{"disambiguationData":[TD([[makeQuery(id+"F0.imprint","IMPRINT",EDGE,{"derivedFrom":subQ0}),1.0]])]});}
            var Q81;
            {var subQ0=sQuery(id+"F0.wireOp",EDGE,"E11");Q81=makeQuery(id+"F0.imprint","IMPRINT",FACE,{"disambiguationData":[TD([[makeQuery(id+"F0.imprint","IMPRINT",EDGE,{"derivedFrom":subQ0}),-1.0]])]});}
            var Q82;
            {var subQ0=sQuery(id+"F0.wireOp",EDGE,"E31.5.0.2");Q82=makeQuery(id+"F0.imprint","IMPRINT",FACE,{"disambiguationData":[TD([[makeQuery(id+"F0.imprint","IMPRINT",EDGE,{"derivedFrom":subQ0}),-1.0]])]});}
            var Q83;
            {var subQ0=sQuery(id+"F0.wireOp",EDGE,"E31.4.0.2");Q83=makeQuery(id+"F0.imprint","IMPRINT",FACE,{"disambiguationData":[TD([[makeQuery(id+"F0.imprint","IMPRINT",EDGE,{"derivedFrom":subQ0}),-1.0]])]});}
            extrude(context, id + "F3", {"entities" : qUnion([Q0, Q1, Q2, Q3, Q4, Q5, Q6, Q7, Q8, Q9, Q10, Q11, Q12, Q13, Q14, Q15, Q16, Q17, Q18, Q19, Q20, Q21, Q22, Q23, Q24, Q25, Q26, Q27, Q28, Q29, Q30, Q31, Q32, Q33, Q34, Q35, Q36, Q37, Q38, Q39, Q40, Q41, Q42, Q43, Q44, Q45, Q46, Q47, Q48, Q49, Q50, Q51, Q52, Q53, Q54, Q55, Q56, Q57, Q58, Q59, Q60, Q61, Q62, Q63, Q64, Q65, Q66, Q67, Q68, Q69, Q70, Q71, Q72, Q73, Q74, Q75, Q76, Q77, Q78, Q79, Q80, Q81, Q82, Q83]), "depth" : 53.97 * mm, "offsetDistance" : 25.4 * mm, "hasSecondDirection" : true, "secondDirectionOppositeDirection" : false, "secondDirectionDepth" : 50.8 * mm});
        }
        {
            var Q0;
            Q0=makeQuery(id+"F0.imprint","IMPRINT",FACE,{"disambiguationData":[TD([[makeQuery(id+"F0.imprint","IMPRINT",EDGE,{"derivedFrom":sQuery(id+"F0.wireOp",EDGE,"E10.0.2.15")}),-1.0]])]});
            var Q1;
            {var subQ0=sQuery(id+"F0.wireOp",EDGE,"E62.1.0.3");Q1=makeQuery(id+"F0.imprint","IMPRINT",FACE,{"disambiguationData":[TD([[makeQuery(id+"F0.imprint","IMPRINT",EDGE,{"derivedFrom":subQ0}),-1.0]])]});}
            var Q2;
            Q2=makeQuery(id+"F0.imprint","IMPRINT",FACE,{"disambiguationData":[TD([[makeQuery(id+"F0.imprint","IMPRINT",EDGE,{"derivedFrom":sQuery(id+"F0.wireOp",EDGE,"E10.0.2.49")}),-1.0]])]});
            var Q3;
            {var subQ0=sQuery(id+"F0.wireOp",EDGE,"E62.1.0.0");Q3=makeQuery(id+"F0.imprint","IMPRINT",FACE,{"disambiguationData":[TD([[makeQuery(id+"F0.imprint","IMPRINT",EDGE,{"derivedFrom":subQ0}),1.0]])]});}
            var Q4;
            {var subQ11=sQuery(id+"F0.wireOp",EDGE,"E10.0.3.12");Q4=makeQuery(id+"F0.imprint","IMPRINT",FACE,{"disambiguationData":[TD([[makeQuery(id+"F0.imprint","IMPRINT",EDGE,{"derivedFrom":subQ11}),-1.0]])]});}
            var Q5;
            Q5=makeQuery(id+"F0.imprint","IMPRINT",FACE,{"disambiguationData":[TD([[makeQuery(id+"F0.imprint","IMPRINT",EDGE,{"derivedFrom":sQuery(id+"F0.wireOp",EDGE,"E10.0.3.10")}),-1.0]])]});
            var Q6;
            {var subQ0=sQuery(id+"F0.wireOp",EDGE,"E56.1.0.2");Q6=makeQuery(id+"F0.imprint","IMPRINT",FACE,{"disambiguationData":[TD([[makeQuery(id+"F0.imprint","IMPRINT",EDGE,{"derivedFrom":subQ0}),1.0]])]});}
            var Q7;
            Q7=makeQuery(id+"F0.imprint","IMPRINT",FACE,{"disambiguationData":[TD([[makeQuery(id+"F0.imprint","IMPRINT",EDGE,{"derivedFrom":sQuery(id+"F0.wireOp",EDGE,"E10.0.2.2")}),-1.0]])]});
            var Q8;
            {var subQ0=sQuery(id+"F0.wireOp",EDGE,"E56.1.0.1");Q8=makeQuery(id+"F0.imprint","IMPRINT",FACE,{"disambiguationData":[TD([[makeQuery(id+"F0.imprint","IMPRINT",EDGE,{"derivedFrom":subQ0}),1.0]])]});}
            var Q9;
            Q9=makeQuery(id+"F0.imprint","IMPRINT",FACE,{"disambiguationData":[TD([[makeQuery(id+"F0.imprint","IMPRINT",EDGE,{"derivedFrom":sQuery(id+"F0.wireOp",EDGE,"E10.0.2.61")}),-1.0]])]});
            var Q10;
            {var subQ0=sQuery(id+"F0.wireOp",EDGE,"E38.7.0.0");Q10=makeQuery(id+"F0.imprint","IMPRINT",FACE,{"disambiguationData":[TD([[makeQuery(id+"F0.imprint","IMPRINT",EDGE,{"derivedFrom":subQ0}),-1.0]])]});}
            var Q11;
            {var subQ0=sQuery(id+"F0.wireOp",EDGE,"E58.1.0.4");Q11=makeQuery(id+"F0.imprint","IMPRINT",FACE,{"disambiguationData":[TD([[makeQuery(id+"F0.imprint","IMPRINT",EDGE,{"derivedFrom":subQ0}),1.0]])]});}
            var Q12;
            {var subQ0=sQuery(id+"F0.wireOp",EDGE,"E31.7.0.2");Q12=makeQuery(id+"F0.imprint","IMPRINT",FACE,{"disambiguationData":[TD([[makeQuery(id+"F0.imprint","IMPRINT",EDGE,{"derivedFrom":subQ0}),-1.0]])]});}
            var Q13;
            {var subQ0=sQuery(id+"F0.wireOp",EDGE,"E54.4.0.5");Q13=makeQuery(id+"F0.imprint","IMPRINT",FACE,{"disambiguationData":[TD([[makeQuery(id+"F0.imprint","IMPRINT",EDGE,{"derivedFrom":subQ0}),1.0]])]});}
            var Q14;
            {var subQ0=sQuery(id+"F0.wireOp",EDGE,"E38.6.0.1");Q14=makeQuery(id+"F0.imprint","IMPRINT",FACE,{"disambiguationData":[TD([[makeQuery(id+"F0.imprint","IMPRINT",EDGE,{"derivedFrom":subQ0}),1.0]])]});}
            var Q15;
            {var subQ0=sQuery(id+"F0.wireOp",EDGE,"E54.3.0.3");Q15=makeQuery(id+"F0.imprint","IMPRINT",FACE,{"disambiguationData":[TD([[makeQuery(id+"F0.imprint","IMPRINT",EDGE,{"derivedFrom":subQ0}),1.0]])]});}
            var Q16;
            {var subQ0=sQuery(id+"F0.wireOp",EDGE,"E39.1.0.11");Q16=makeQuery(id+"F0.imprint","IMPRINT",FACE,{"disambiguationData":[TD([[makeQuery(id+"F0.imprint","IMPRINT",EDGE,{"derivedFrom":subQ0}),1.0]])]});}
            var Q17;
            {var subQ0=sQuery(id+"F0.wireOp",EDGE,"E38.1.0.1");Q17=makeQuery(id+"F0.imprint","IMPRINT",FACE,{"disambiguationData":[TD([[makeQuery(id+"F0.imprint","IMPRINT",EDGE,{"derivedFrom":subQ0}),1.0]])]});}
            var Q18;
            {var subQ0=sQuery(id+"F0.wireOp",EDGE,"E22.trimOffspring");Q18=makeQuery(id+"F0.imprint","IMPRINT",FACE,{"disambiguationData":[TD([[makeQuery(id+"F0.imprint","IMPRINT",EDGE,{"derivedFrom":subQ0}),1.0]])]});}
            var Q19;
            {var subQ0=sQuery(id+"F0.wireOp",EDGE,"E31.1.0.2");Q19=makeQuery(id+"F0.imprint","IMPRINT",FACE,{"disambiguationData":[TD([[makeQuery(id+"F0.imprint","IMPRINT",EDGE,{"derivedFrom":subQ0}),-1.0]])]});}
            var Q20;
            {var subQ0=sQuery(id+"F0.wireOp",EDGE,"E64.1.0.1");Q20=makeQuery(id+"F0.imprint","IMPRINT",FACE,{"disambiguationData":[TD([[makeQuery(id+"F0.imprint","IMPRINT",EDGE,{"derivedFrom":subQ0}),1.0]])]});}
            var Q21;
            {var subQ0=sQuery(id+"F0.wireOp",EDGE,"E34.trimOffspring");Q21=makeQuery(id+"F0.imprint","IMPRINT",FACE,{"disambiguationData":[TD([[makeQuery(id+"F0.imprint","IMPRINT",EDGE,{"derivedFrom":subQ0}),1.0]])]});}
            var Q22;
            {var subQ0=sQuery(id+"F0.wireOp",EDGE,"E62.1.0.4");Q22=makeQuery(id+"F0.imprint","IMPRINT",FACE,{"disambiguationData":[TD([[makeQuery(id+"F0.imprint","IMPRINT",EDGE,{"derivedFrom":subQ0}),1.0]])]});}
            var Q23;
            {var subQ13=sQuery(id+"F0.wireOp",EDGE,"E10.0.1.23");Q23=makeQuery(id+"F0.imprint","IMPRINT",FACE,{"disambiguationData":[TD([[makeQuery(id+"F0.imprint","IMPRINT",EDGE,{"derivedFrom":subQ13}),-1.0]])]});}
            var Q24;
            {var subQ0=sQuery(id+"F0.wireOp",EDGE,"E65.1.0.2");Q24=makeQuery(id+"F0.imprint","IMPRINT",FACE,{"disambiguationData":[TD([[makeQuery(id+"F0.imprint","IMPRINT",EDGE,{"derivedFrom":subQ0}),1.0]])]});}
            var Q25;
            {var subQ0=sQuery(id+"F0.wireOp",EDGE,"E11");Q25=makeQuery(id+"F0.imprint","IMPRINT",FACE,{"disambiguationData":[TD([[makeQuery(id+"F0.imprint","IMPRINT",EDGE,{"derivedFrom":subQ0}),-1.0]])]});}
            var Q26;
            {var subQ0=sQuery(id+"F0.wireOp",EDGE,"E56.1.0.4");Q26=makeQuery(id+"F0.imprint","IMPRINT",FACE,{"disambiguationData":[TD([[makeQuery(id+"F0.imprint","IMPRINT",EDGE,{"derivedFrom":subQ0}),1.0]])]});}
            var Q27;
            {var subQ12=sQuery(id+"F0.wireOp",EDGE,"E10.0.1.8");Q27=makeQuery(id+"F0.imprint","IMPRINT",FACE,{"disambiguationData":[TD([[makeQuery(id+"F0.imprint","IMPRINT",EDGE,{"derivedFrom":subQ12}),-1.0]])]});}
            var Q28;
            {var subQ0=sQuery(id+"F0.wireOp",EDGE,"E59.1.0.1");Q28=makeQuery(id+"F0.imprint","IMPRINT",FACE,{"disambiguationData":[TD([[makeQuery(id+"F0.imprint","IMPRINT",EDGE,{"derivedFrom":subQ0}),1.0]])]});}
            var Q29;
            {var subQ0=sQuery(id+"F0.wireOp",EDGE,"E31.8.0.4");Q29=makeQuery(id+"F0.imprint","IMPRINT",FACE,{"disambiguationData":[TD([[makeQuery(id+"F0.imprint","IMPRINT",EDGE,{"derivedFrom":subQ0}),-1.0]])]});}
            extrude(context, id + "F4", {"entities" : qUnion([Q0, Q1, Q2, Q3, Q4, Q5, Q6, Q7, Q8, Q9, Q10, Q11, Q12, Q13, Q14, Q15, Q16, Q17, Q18, Q19, Q20, Q21, Q22, Q23, Q24, Q25, Q26, Q27, Q28, Q29]), "depth" : 28.57 * mm, "offsetDistance" : 25.4 * mm, "hasSecondDirection" : true, "secondDirectionOppositeDirection" : false, "secondDirectionDepth" : 25.4 * mm});
        }
        {
            var Q0;
            {var subQ0=sQuery(id+"F0.wireOp",EDGE,"E31.8.0.4");Q0=makeQuery(id+"F0.imprint","IMPRINT",FACE,{"disambiguationData":[TD([[makeQuery(id+"F0.imprint","IMPRINT",EDGE,{"derivedFrom":subQ0}),-1.0]])]});}
            var Q1;
            {var subQ0=sQuery(id+"F0.wireOp",EDGE,"E59.1.0.1");Q1=makeQuery(id+"F0.imprint","IMPRINT",FACE,{"disambiguationData":[TD([[makeQuery(id+"F0.imprint","IMPRINT",EDGE,{"derivedFrom":subQ0}),1.0]])]});}
            var Q2;
            {var subQ0=sQuery(id+"F0.wireOp",EDGE,"E38.7.0.0");Q2=makeQuery(id+"F0.imprint","IMPRINT",FACE,{"disambiguationData":[TD([[makeQuery(id+"F0.imprint","IMPRINT",EDGE,{"derivedFrom":subQ0}),-1.0]])]});}
            var Q3;
            {var subQ0=sQuery(id+"F0.wireOp",EDGE,"E58.1.0.4");Q3=makeQuery(id+"F0.imprint","IMPRINT",FACE,{"disambiguationData":[TD([[makeQuery(id+"F0.imprint","IMPRINT",EDGE,{"derivedFrom":subQ0}),1.0]])]});}
            var Q4;
            {var subQ0=sQuery(id+"F0.wireOp",EDGE,"E31.7.0.2");Q4=makeQuery(id+"F0.imprint","IMPRINT",FACE,{"disambiguationData":[TD([[makeQuery(id+"F0.imprint","IMPRINT",EDGE,{"derivedFrom":subQ0}),-1.0]])]});}
            var Q5;
            {var subQ0=sQuery(id+"F0.wireOp",EDGE,"E54.4.0.5");Q5=makeQuery(id+"F0.imprint","IMPRINT",FACE,{"disambiguationData":[TD([[makeQuery(id+"F0.imprint","IMPRINT",EDGE,{"derivedFrom":subQ0}),1.0]])]});}
            var Q6;
            {var subQ0=sQuery(id+"F0.wireOp",EDGE,"E38.6.0.1");Q6=makeQuery(id+"F0.imprint","IMPRINT",FACE,{"disambiguationData":[TD([[makeQuery(id+"F0.imprint","IMPRINT",EDGE,{"derivedFrom":subQ0}),1.0]])]});}
            var Q7;
            {var subQ0=sQuery(id+"F0.wireOp",EDGE,"E54.3.0.3");Q7=makeQuery(id+"F0.imprint","IMPRINT",FACE,{"disambiguationData":[TD([[makeQuery(id+"F0.imprint","IMPRINT",EDGE,{"derivedFrom":subQ0}),1.0]])]});}
            var Q8;
            {var subQ0=sQuery(id+"F0.wireOp",EDGE,"E39.1.0.11");Q8=makeQuery(id+"F0.imprint","IMPRINT",FACE,{"disambiguationData":[TD([[makeQuery(id+"F0.imprint","IMPRINT",EDGE,{"derivedFrom":subQ0}),1.0]])]});}
            var Q9;
            {var subQ0=sQuery(id+"F0.wireOp",EDGE,"E38.1.0.1");Q9=makeQuery(id+"F0.imprint","IMPRINT",FACE,{"disambiguationData":[TD([[makeQuery(id+"F0.imprint","IMPRINT",EDGE,{"derivedFrom":subQ0}),1.0]])]});}
            var Q10;
            {var subQ0=sQuery(id+"F0.wireOp",EDGE,"E22.trimOffspring");Q10=makeQuery(id+"F0.imprint","IMPRINT",FACE,{"disambiguationData":[TD([[makeQuery(id+"F0.imprint","IMPRINT",EDGE,{"derivedFrom":subQ0}),1.0]])]});}
            var Q11;
            {var subQ0=sQuery(id+"F0.wireOp",EDGE,"E31.1.0.2");Q11=makeQuery(id+"F0.imprint","IMPRINT",FACE,{"disambiguationData":[TD([[makeQuery(id+"F0.imprint","IMPRINT",EDGE,{"derivedFrom":subQ0}),-1.0]])]});}
            var Q12;
            {var subQ0=sQuery(id+"F0.wireOp",EDGE,"E64.1.0.1");Q12=makeQuery(id+"F0.imprint","IMPRINT",FACE,{"disambiguationData":[TD([[makeQuery(id+"F0.imprint","IMPRINT",EDGE,{"derivedFrom":subQ0}),1.0]])]});}
            var Q13;
            {var subQ0=sQuery(id+"F0.wireOp",EDGE,"E34.trimOffspring");Q13=makeQuery(id+"F0.imprint","IMPRINT",FACE,{"disambiguationData":[TD([[makeQuery(id+"F0.imprint","IMPRINT",EDGE,{"derivedFrom":subQ0}),1.0]])]});}
            var Q14;
            {var subQ0=sQuery(id+"F0.wireOp",EDGE,"E65.1.0.2");Q14=makeQuery(id+"F0.imprint","IMPRINT",FACE,{"disambiguationData":[TD([[makeQuery(id+"F0.imprint","IMPRINT",EDGE,{"derivedFrom":subQ0}),1.0]])]});}
            var Q15;
            {var subQ0=sQuery(id+"F0.wireOp",EDGE,"E11");Q15=makeQuery(id+"F0.imprint","IMPRINT",FACE,{"disambiguationData":[TD([[makeQuery(id+"F0.imprint","IMPRINT",EDGE,{"derivedFrom":subQ0}),-1.0]])]});}
            extrude(context, id + "F5", {"entities" : qUnion([Q0, Q1, Q2, Q3, Q4, Q5, Q6, Q7, Q8, Q9, Q10, Q11, Q12, Q13, Q14, Q15]), "operationType" : NewBodyOperationType.ADD, "depth" : 53.97 * mm, "offsetDistance" : 25.4 * mm, "hasSecondDirection" : true, "secondDirectionOppositeDirection" : false, "secondDirectionDepth" : 25.4 * mm});
        }
        {
            var Q0;
            {var subQ0=sQuery(id+"F0.wireOp",EDGE,"E38.3.0.1");Q0=makeQuery(id+"F0.imprint","IMPRINT",FACE,{"disambiguationData":[TD([[makeQuery(id+"F0.imprint","IMPRINT",EDGE,{"derivedFrom":subQ0}),1.0]])]});}
            var Q1;
            {var subQ0=sQuery(id+"F0.wireOp",EDGE,"E39.2.0.2");Q1=makeQuery(id+"F0.imprint","IMPRINT",FACE,{"disambiguationData":[TD([[makeQuery(id+"F0.imprint","IMPRINT",EDGE,{"derivedFrom":subQ0}),1.0]])]});}
            var Q2;
            {var subQ0=sQuery(id+"F0.wireOp",EDGE,"E31.3.0.2");Q2=makeQuery(id+"F0.imprint","IMPRINT",FACE,{"disambiguationData":[TD([[makeQuery(id+"F0.imprint","IMPRINT",EDGE,{"derivedFrom":subQ0}),-1.0]])]});}
            var Q3;
            {var subQ0=sQuery(id+"F0.wireOp",EDGE,"E48.trimOffspring");Q3=makeQuery(id+"F0.imprint","IMPRINT",FACE,{"disambiguationData":[TD([[makeQuery(id+"F0.imprint","IMPRINT",EDGE,{"derivedFrom":subQ0}),1.0]])]});}
            var Q4;
            {var subQ0=sQuery(id+"F0.wireOp",EDGE,"E38.2.0.1");Q4=makeQuery(id+"F0.imprint","IMPRINT",FACE,{"disambiguationData":[TD([[makeQuery(id+"F0.imprint","IMPRINT",EDGE,{"derivedFrom":subQ0}),1.0]])]});}
            var Q5;
            {var subQ0=sQuery(id+"F0.wireOp",EDGE,"E39.1.0.2");Q5=makeQuery(id+"F0.imprint","IMPRINT",FACE,{"disambiguationData":[TD([[makeQuery(id+"F0.imprint","IMPRINT",EDGE,{"derivedFrom":subQ0}),1.0]])]});}
            var Q6;
            {var subQ0=sQuery(id+"F0.wireOp",EDGE,"E31.2.0.2");Q6=makeQuery(id+"F0.imprint","IMPRINT",FACE,{"disambiguationData":[TD([[makeQuery(id+"F0.imprint","IMPRINT",EDGE,{"derivedFrom":subQ0}),-1.0]])]});}
            var Q7;
            {var subQ0=sQuery(id+"F0.wireOp",EDGE,"E54.2.0.5");Q7=makeQuery(id+"F0.imprint","IMPRINT",FACE,{"disambiguationData":[TD([[makeQuery(id+"F0.imprint","IMPRINT",EDGE,{"derivedFrom":subQ0}),1.0]])]});}
            var Q8;
            {var subQ0=sQuery(id+"F0.wireOp",EDGE,"E38.4.0.1");Q8=makeQuery(id+"F0.imprint","IMPRINT",FACE,{"disambiguationData":[TD([[makeQuery(id+"F0.imprint","IMPRINT",EDGE,{"derivedFrom":subQ0}),1.0]])]});}
            var Q9;
            {var subQ0=sQuery(id+"F0.wireOp",EDGE,"E39.3.0.2");Q9=makeQuery(id+"F0.imprint","IMPRINT",FACE,{"disambiguationData":[TD([[makeQuery(id+"F0.imprint","IMPRINT",EDGE,{"derivedFrom":subQ0}),1.0]])]});}
            var Q10;
            {var subQ0=sQuery(id+"F0.wireOp",EDGE,"E54.1.0.5");Q10=makeQuery(id+"F0.imprint","IMPRINT",FACE,{"disambiguationData":[TD([[makeQuery(id+"F0.imprint","IMPRINT",EDGE,{"derivedFrom":subQ0}),1.0]])]});}
            var Q11;
            {var subQ0=sQuery(id+"F0.wireOp",EDGE,"E24.trimOffspring");Q11=makeQuery(id+"F0.imprint","IMPRINT",FACE,{"disambiguationData":[TD([[makeQuery(id+"F0.imprint","IMPRINT",EDGE,{"derivedFrom":subQ0}),1.0]])]});}
            var Q12;
            {var subQ0=sQuery(id+"F0.wireOp",EDGE,"E38.1.0.0");Q12=makeQuery(id+"F0.imprint","IMPRINT",FACE,{"disambiguationData":[TD([[makeQuery(id+"F0.imprint","IMPRINT",EDGE,{"derivedFrom":subQ0}),-1.0]])]});}
            var Q13;
            {var subQ0=sQuery(id+"F0.wireOp",EDGE,"E64.1.0.2");Q13=makeQuery(id+"F0.imprint","IMPRINT",FACE,{"disambiguationData":[TD([[makeQuery(id+"F0.imprint","IMPRINT",EDGE,{"derivedFrom":subQ0}),1.0]])]});}
            var Q14;
            {var subQ0=sQuery(id+"F0.wireOp",EDGE,"E31.1.0.4");Q14=makeQuery(id+"F0.imprint","IMPRINT",FACE,{"disambiguationData":[TD([[makeQuery(id+"F0.imprint","IMPRINT",EDGE,{"derivedFrom":subQ0}),-1.0]])]});}
            var Q15;
            {var subQ0=sQuery(id+"F0.wireOp",EDGE,"E65.1.0.3");Q15=makeQuery(id+"F0.imprint","IMPRINT",FACE,{"disambiguationData":[TD([[makeQuery(id+"F0.imprint","IMPRINT",EDGE,{"derivedFrom":subQ0}),1.0]])]});}
            var Q16;
            {var subQ0=sQuery(id+"F0.wireOp",EDGE,"E40");Q16=makeQuery(id+"F0.imprint","IMPRINT",FACE,{"disambiguationData":[TD([[makeQuery(id+"F0.imprint","IMPRINT",EDGE,{"derivedFrom":subQ0}),-1.0]])]});}
            var Q17;
            {var subQ0=sQuery(id+"F0.wireOp",EDGE,"E39.4.0.2");Q17=makeQuery(id+"F0.imprint","IMPRINT",FACE,{"disambiguationData":[TD([[makeQuery(id+"F0.imprint","IMPRINT",EDGE,{"derivedFrom":subQ0}),1.0]])]});}
            var Q18;
            {var subQ0=sQuery(id+"F0.wireOp",EDGE,"E38.5.0.1");Q18=makeQuery(id+"F0.imprint","IMPRINT",FACE,{"disambiguationData":[TD([[makeQuery(id+"F0.imprint","IMPRINT",EDGE,{"derivedFrom":subQ0}),1.0]])]});}
            var Q19;
            {var subQ0=sQuery(id+"F0.wireOp",EDGE,"E54.3.0.5");Q19=makeQuery(id+"F0.imprint","IMPRINT",FACE,{"disambiguationData":[TD([[makeQuery(id+"F0.imprint","IMPRINT",EDGE,{"derivedFrom":subQ0}),1.0]])]});}
            var Q20;
            {var subQ0=sQuery(id+"F0.wireOp",EDGE,"E31.6.0.2");Q20=makeQuery(id+"F0.imprint","IMPRINT",FACE,{"disambiguationData":[TD([[makeQuery(id+"F0.imprint","IMPRINT",EDGE,{"derivedFrom":subQ0}),-1.0]])]});}
            var Q21;
            {var subQ0=sQuery(id+"F0.wireOp",EDGE,"E54.4.0.8");Q21=makeQuery(id+"F0.imprint","IMPRINT",FACE,{"disambiguationData":[TD([[makeQuery(id+"F0.imprint","IMPRINT",EDGE,{"derivedFrom":subQ0}),1.0]])]});}
            var Q22;
            {var subQ0=sQuery(id+"F0.wireOp",EDGE,"E38.6.0.0");Q22=makeQuery(id+"F0.imprint","IMPRINT",FACE,{"disambiguationData":[TD([[makeQuery(id+"F0.imprint","IMPRINT",EDGE,{"derivedFrom":subQ0}),-1.0]])]});}
            var Q23;
            {var subQ0=sQuery(id+"F0.wireOp",EDGE,"E58.1.0.3");Q23=makeQuery(id+"F0.imprint","IMPRINT",FACE,{"disambiguationData":[TD([[makeQuery(id+"F0.imprint","IMPRINT",EDGE,{"derivedFrom":subQ0}),-1.0]])]});}
            var Q24;
            {var subQ0=sQuery(id+"F0.wireOp",EDGE,"E31.7.0.4");Q24=makeQuery(id+"F0.imprint","IMPRINT",FACE,{"disambiguationData":[TD([[makeQuery(id+"F0.imprint","IMPRINT",EDGE,{"derivedFrom":subQ0}),-1.0]])]});}
            var Q25;
            {var subQ0=sQuery(id+"F0.wireOp",EDGE,"E59.1.0.2");Q25=makeQuery(id+"F0.imprint","IMPRINT",FACE,{"disambiguationData":[TD([[makeQuery(id+"F0.imprint","IMPRINT",EDGE,{"derivedFrom":subQ0}),1.0]])]});}
            var Q26;
            {var subQ0=sQuery(id+"F0.wireOp",EDGE,"E39.4.0.10");Q26=makeQuery(id+"F0.imprint","IMPRINT",FACE,{"disambiguationData":[TD([[makeQuery(id+"F0.imprint","IMPRINT",EDGE,{"derivedFrom":subQ0}),1.0]])]});}
            var Q27;
            {var subQ0=sQuery(id+"F0.wireOp",EDGE,"E31.5.0.2");Q27=makeQuery(id+"F0.imprint","IMPRINT",FACE,{"disambiguationData":[TD([[makeQuery(id+"F0.imprint","IMPRINT",EDGE,{"derivedFrom":subQ0}),-1.0]])]});}
            var Q28;
            {var subQ0=sQuery(id+"F0.wireOp",EDGE,"E31.4.0.2");Q28=makeQuery(id+"F0.imprint","IMPRINT",FACE,{"disambiguationData":[TD([[makeQuery(id+"F0.imprint","IMPRINT",EDGE,{"derivedFrom":subQ0}),-1.0]])]});}
            extrude(context, id + "F6", {"entities" : qUnion([Q0, Q1, Q2, Q3, Q4, Q5, Q6, Q7, Q8, Q9, Q10, Q11, Q12, Q13, Q14, Q15, Q16, Q17, Q18, Q19, Q20, Q21, Q22, Q23, Q24, Q25, Q26, Q27, Q28]), "operationType" : NewBodyOperationType.ADD, "depth" : 79.38 * mm, "offsetDistance" : 25.4 * mm, "hasSecondDirection" : true, "secondDirectionOppositeDirection" : false, "secondDirectionDepth" : 50.8 * mm});
        }
        {
            var Q0;
            {var subQ0=sQuery(id+"F0.wireOp",EDGE,"E54.1.0.6");Q0=makeQuery(id+"F0.imprint","IMPRINT",FACE,{"disambiguationData":[TD([[makeQuery(id+"F0.imprint","IMPRINT",EDGE,{"derivedFrom":subQ0}),1.0]])]});}
            var Q1;
            {var subQ0=sQuery(id+"F0.wireOp",EDGE,"E64.1.0.7");Q1=makeQuery(id+"F0.imprint","IMPRINT",FACE,{"disambiguationData":[TD([[makeQuery(id+"F0.imprint","IMPRINT",EDGE,{"derivedFrom":subQ0}),1.0]])]});}
            var Q2;
            {var subQ0=sQuery(id+"F0.wireOp",EDGE,"E31.2.0.4");Q2=makeQuery(id+"F0.imprint","IMPRINT",FACE,{"disambiguationData":[TD([[makeQuery(id+"F0.imprint","IMPRINT",EDGE,{"derivedFrom":subQ0}),-1.0]])]});}
            var Q3;
            {var subQ0=sQuery(id+"F0.wireOp",EDGE,"E26.trimOffspring");Q3=makeQuery(id+"F0.imprint","IMPRINT",FACE,{"disambiguationData":[TD([[makeQuery(id+"F0.imprint","IMPRINT",EDGE,{"derivedFrom":subQ0}),1.0]])]});}
            var Q4;
            {var subQ0=sQuery(id+"F0.wireOp",EDGE,"E38.2.0.0");Q4=makeQuery(id+"F0.imprint","IMPRINT",FACE,{"disambiguationData":[TD([[makeQuery(id+"F0.imprint","IMPRINT",EDGE,{"derivedFrom":subQ0}),-1.0]])]});}
            var Q5;
            {var subQ0=sQuery(id+"F0.wireOp",EDGE,"E54.1.0.0");Q5=makeQuery(id+"F0.imprint","IMPRINT",FACE,{"disambiguationData":[TD([[makeQuery(id+"F0.imprint","IMPRINT",EDGE,{"derivedFrom":subQ0}),1.0]])]});}
            var Q6;
            {var subQ0=sQuery(id+"F0.wireOp",EDGE,"E31.3.0.4");Q6=makeQuery(id+"F0.imprint","IMPRINT",FACE,{"disambiguationData":[TD([[makeQuery(id+"F0.imprint","IMPRINT",EDGE,{"derivedFrom":subQ0}),-1.0]])]});}
            var Q7;
            {var subQ0=sQuery(id+"F0.wireOp",EDGE,"E39.1.0.3");Q7=makeQuery(id+"F0.imprint","IMPRINT",FACE,{"disambiguationData":[TD([[makeQuery(id+"F0.imprint","IMPRINT",EDGE,{"derivedFrom":subQ0}),1.0]])]});}
            var Q8;
            {var subQ0=sQuery(id+"F0.wireOp",EDGE,"E38.3.0.0");Q8=makeQuery(id+"F0.imprint","IMPRINT",FACE,{"disambiguationData":[TD([[makeQuery(id+"F0.imprint","IMPRINT",EDGE,{"derivedFrom":subQ0}),-1.0]])]});}
            var Q9;
            {var subQ0=sQuery(id+"F0.wireOp",EDGE,"E54.2.0.0");Q9=makeQuery(id+"F0.imprint","IMPRINT",FACE,{"disambiguationData":[TD([[makeQuery(id+"F0.imprint","IMPRINT",EDGE,{"derivedFrom":subQ0}),1.0]])]});}
            var Q10;
            {var subQ0=sQuery(id+"F0.wireOp",EDGE,"E31.4.0.4");Q10=makeQuery(id+"F0.imprint","IMPRINT",FACE,{"disambiguationData":[TD([[makeQuery(id+"F0.imprint","IMPRINT",EDGE,{"derivedFrom":subQ0}),-1.0]])]});}
            var Q11;
            {var subQ0=sQuery(id+"F0.wireOp",EDGE,"E39.2.0.3");Q11=makeQuery(id+"F0.imprint","IMPRINT",FACE,{"disambiguationData":[TD([[makeQuery(id+"F0.imprint","IMPRINT",EDGE,{"derivedFrom":subQ0}),1.0]])]});}
            var Q12;
            {var subQ0=sQuery(id+"F0.wireOp",EDGE,"E38.4.0.0");Q12=makeQuery(id+"F0.imprint","IMPRINT",FACE,{"disambiguationData":[TD([[makeQuery(id+"F0.imprint","IMPRINT",EDGE,{"derivedFrom":subQ0}),-1.0]])]});}
            var Q13;
            {var subQ0=sQuery(id+"F0.wireOp",EDGE,"E54.3.0.0");Q13=makeQuery(id+"F0.imprint","IMPRINT",FACE,{"disambiguationData":[TD([[makeQuery(id+"F0.imprint","IMPRINT",EDGE,{"derivedFrom":subQ0}),1.0]])]});}
            var Q14;
            {var subQ0=sQuery(id+"F0.wireOp",EDGE,"E31.5.0.4");Q14=makeQuery(id+"F0.imprint","IMPRINT",FACE,{"disambiguationData":[TD([[makeQuery(id+"F0.imprint","IMPRINT",EDGE,{"derivedFrom":subQ0}),-1.0]])]});}
            var Q15;
            {var subQ0=sQuery(id+"F0.wireOp",EDGE,"E39.3.0.3");Q15=makeQuery(id+"F0.imprint","IMPRINT",FACE,{"disambiguationData":[TD([[makeQuery(id+"F0.imprint","IMPRINT",EDGE,{"derivedFrom":subQ0}),1.0]])]});}
            var Q16;
            {var subQ0=sQuery(id+"F0.wireOp",EDGE,"E38.5.0.0");Q16=makeQuery(id+"F0.imprint","IMPRINT",FACE,{"disambiguationData":[TD([[makeQuery(id+"F0.imprint","IMPRINT",EDGE,{"derivedFrom":subQ0}),-1.0]])]});}
            var Q17;
            {var subQ0=sQuery(id+"F0.wireOp",EDGE,"E54.4.0.0");Q17=makeQuery(id+"F0.imprint","IMPRINT",FACE,{"disambiguationData":[TD([[makeQuery(id+"F0.imprint","IMPRINT",EDGE,{"derivedFrom":subQ0}),1.0]])]});}
            var Q18;
            {var subQ0=sQuery(id+"F0.wireOp",EDGE,"E31.6.0.4");Q18=makeQuery(id+"F0.imprint","IMPRINT",FACE,{"disambiguationData":[TD([[makeQuery(id+"F0.imprint","IMPRINT",EDGE,{"derivedFrom":subQ0}),-1.0]])]});}
            var Q19;
            {var subQ0=sQuery(id+"F0.wireOp",EDGE,"E58.1.0.5");Q19=makeQuery(id+"F0.imprint","IMPRINT",FACE,{"disambiguationData":[TD([[makeQuery(id+"F0.imprint","IMPRINT",EDGE,{"derivedFrom":subQ0}),1.0]])]});}
            var Q20;
            {var subQ0=sQuery(id+"F0.wireOp",EDGE,"E39.3.0.10");Q20=makeQuery(id+"F0.imprint","IMPRINT",FACE,{"disambiguationData":[TD([[makeQuery(id+"F0.imprint","IMPRINT",EDGE,{"derivedFrom":subQ0}),1.0]])]});}
            extrude(context, id + "F7", {"entities" : qUnion([Q0, Q1, Q2, Q3, Q4, Q5, Q6, Q7, Q8, Q9, Q10, Q11, Q12, Q13, Q14, Q15, Q16, Q17, Q18, Q19, Q20]), "operationType" : NewBodyOperationType.ADD, "depth" : 104.77 * mm, "offsetDistance" : 25.4 * mm, "hasSecondDirection" : true, "secondDirectionOppositeDirection" : false, "secondDirectionDepth" : 76.2 * mm});
        }
    });
